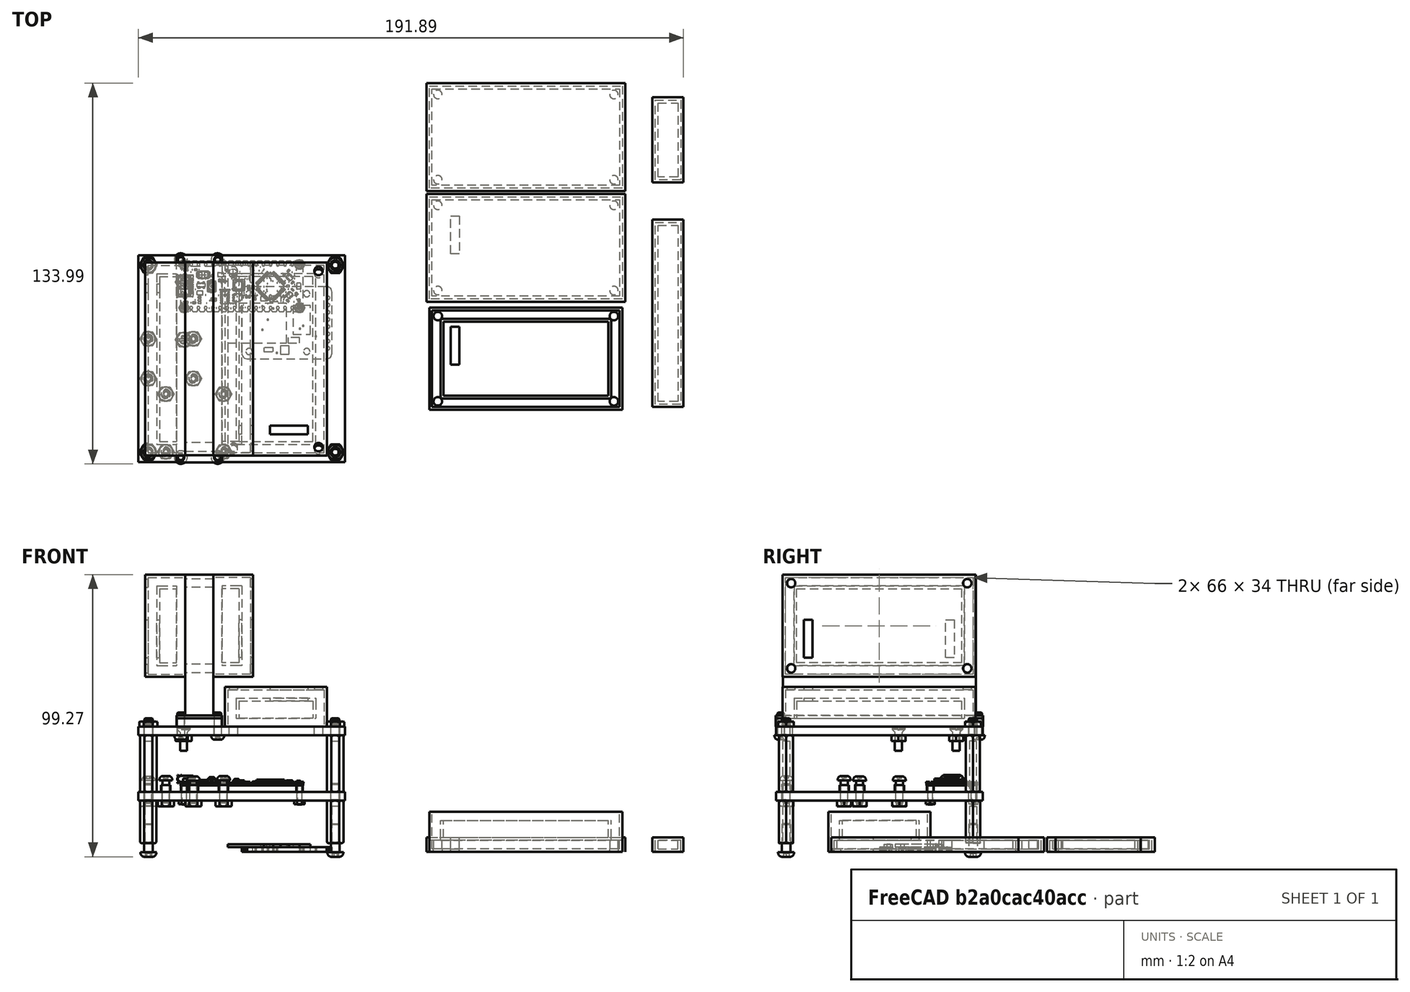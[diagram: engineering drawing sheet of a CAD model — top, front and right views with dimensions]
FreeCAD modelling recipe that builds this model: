
FCSTD DOCUMENT  (FreeCAD 0.20R29410 (Git))
Label: GeigerSat2
Comment: <copyright redacted>
License: All rights reserved
LicenseURL: http://en.wikipedia.org/wiki/All_rights_reserved
objects: Sketcher::SketchObject×62, Part::Feature×60, PartDesign::Pad×47, PartDesign::Body×22, App::DocumentObjectGroup×17, Part::Compound×17, PartDesign::Pocket×15, TechDraw::DrawViewAnnotation×6, Mesh::Feature×4, Part::Box×4, Part::Cut×4, TechDraw::DrawLeaderLine×4, Spreadsheet::Sheet×2, Part::Compound2×1, TechDraw::DrawSVGTemplate×1, TechDraw::DrawViewPart×1, TechDraw::DrawPage×1
note: 293 computed .brp shape members not serialized (recipe doc carries the construction recipe); baked Part::Feature solids carry a one-line shape summary decoded from their .brp

FEATURE [Mesh::Feature] Cubesat_Bottom_Frame
  Placement = pos=(0,0,98) rot=(0,1,0;3.14159rad)
FEATURE [Mesh::Feature] Cubesat_Side_Frame_Plain
  Placement = pos=(50.0625,-8.1e-15,49) rot=(-0.57735,0.57735,0.57735;4.18879rad)
FEATURE [Mesh::Feature] Cubesat_Side_Frame_Plain001
  Placement = pos=(-41.5,-6.6e-15,49) rot=(-0.57735,0.57735,0.57735;4.18879rad)
FEATURE [Mesh::Feature] Cubesat_Bottom_Frame001
FEATURE [App::DocumentObjectGroup] Group001  label="Frame"
  Group = -> [Cubesat_Bottom_Frame,Cubesat_Side_Frame_Plain,Cubesat_Side_Frame_Plain001,Cubesat_Bottom_Frame001]
FEATURE [Part::Feature] Solid018  label="M3x1.8mm Hex Nut"
  Placement = pos=(-32.9375,-32.875,-1.8125) rot=(0,0,1;0rad)
  shape: bbox 6.351 x 6.351 x 1.932 mm, 35 faces (baked)
FEATURE [Part::Feature] Solid019  label="M3x1.8mm Hex Nut001"
  Placement = pos=(32.9375,-32.875,-1.8125) rot=(0,0,1;0rad)
  shape: bbox 6.351 x 6.351 x 1.932 mm, 35 faces (baked)
FEATURE [Part::Feature] Solid020  label="M3x1.8mm Hex Nut002"
  Placement = pos=(32.9375,32.9375,-1.8125) rot=(0,0,1;0rad)
  shape: bbox 6.351 x 6.351 x 1.932 mm, 35 faces (baked)
FEATURE [Part::Feature] Solid021  label="M3x1.8mm Hex Nut003"
  Placement = pos=(-32.94,32.94,-1.81) rot=(0,0,1;0rad)
  shape: bbox 6.351 x 6.351 x 1.932 mm, 35 faces (baked)
FEATURE [Sketcher::SketchObject] Sketch
  FullyConstrained = true
  MapMode = 5
  Support = -> [XY_Plane]
  expr: Constraints[19] = 17.11 - 2.5 - 1
  sketch-geometry (10):
    g0: LineSegment StartX=-36.39 StartY=36.39 StartZ=0 EndX=36.39 EndY=36.39 EndZ=0
    g1: LineSegment StartX=36.39 StartY=36.39 StartZ=0 EndX=36.39 EndY=-36.39 EndZ=0
    g2: LineSegment StartX=36.39 StartY=-36.39 StartZ=0 EndX=-36.39 EndY=-36.39 EndZ=0
    g3: LineSegment StartX=-36.39 StartY=-36.39 StartZ=0 EndX=-36.39 EndY=36.39 EndZ=0
    g4: GeomPoint X=0 Y=0 Z=0
    g5: GeomPoint X=-50 Y=50 Z=0
    g6: GeomPoint X=50 Y=-50 Z=0
    g7: GeomPoint X=50 Y=50 Z=0
    g8: GeomPoint X=-50 Y=-50 Z=0
    g9: GeomPoint X=0 Y=0 Z=0
  constraints (20):
    c: Coincident(g0,g1)
    c: Coincident(g1,g2)
    c: Coincident(g2,g3)
    c: Coincident(g3,g0)
    c: Horizontal(g0)
    c: Horizontal(g2)
    c: Vertical(g1)
    c: Vertical(g3)
    c: Symmetric(g0,g1,g4)
    c: Coincident(g4,g-1)
    c: Equal(g0,g3)
    c: Symmetric(g5,g6,g9)
    c: Horizontal(g8,g6)
    c: Horizontal(g7,g5)
    c: Vertical(g5,g8)
    c: Vertical(g7,g6)
    c: Coincident(g9,g4)
    c: DistanceX(g5,g7) = 100
    c: DistanceY(g8,g5) = 100
    c: DistanceX(g5,g0) = 13.61
FEATURE [PartDesign::Pad] Pad
  Direction = (0,0,1)
  Length = 3
  Length2 = 10
  Profile = -> Sketch
  ReferenceAxis = -> Sketch [N_Axis]
  Type = 0
FEATURE [Part::Feature] Solid014  label="M3x10HexButtonHead"
  Placement = pos=(-32.93,-32.88,63.06) rot=(0,0,1;0rad)
  shape: bbox 5.7 x 5.7 x 11.65 mm, 13 faces (baked)
FEATURE [Part::Feature] Solid015  label="M3x10HexButtonHead003"
  Placement = pos=(-32.93,32.93,63.06) rot=(0,0,1;0rad)
  shape: bbox 5.7 x 5.7 x 11.65 mm, 13 faces (baked)
FEATURE [Part::Feature] Solid016  label="M3x10HexButtonHead002"
  Placement = pos=(32.88,32.93,63.06) rot=(0,0,1;0rad)
  shape: bbox 5.7 x 5.7 x 11.65 mm, 13 faces (baked)
FEATURE [Part::Feature] Solid017  label="M3x10HexButtonHead001"
  Placement = pos=(32.88,-32.88,63.06) rot=(0,0,1;0rad)
  shape: bbox 5.7 x 5.7 x 11.65 mm, 13 faces (baked)
FEATURE [Part::Compound] Compound  label="Stack Screws"
  Links = -> [Solid015,Solid016,Solid017,Solid014]
  Placement = pos=(-8e-15,0,62.9375) rot=(0,1,0;3.14159rad)
FEATURE [Part::Compound] Compound002  label="Stack Nuts"
  Links = -> [Solid021,Solid018,Solid019,Solid020]
  Placement = pos=(0,0,45.8125) rot=(0,0,1;0rad)
FEATURE [Sketcher::SketchObject] Sketch002
  FullyConstrained = true
  MapMode = 5
  Placement = pos=(0,0,3) rot=(0,0,1;0rad)
  Support = -> [Pad]
  expr: Constraints[31] = 17.11 - 2.5 - 1
  expr: Constraints[34] = 17.11 - 2.5 - 1
  expr: Constraints[35] = 2
  expr: Constraints[6] = 43.16
  expr: Constraints[7] = 17.76
  sketch-geometry (18):
    g0: GeomPoint X=-21.58 Y=34.39 Z=0
    g1: GeomPoint X=21.58 Y=34.39 Z=0
    g2: GeomPoint X=-21.58 Y=16.63 Z=0
    g3: GeomPoint X=21.58 Y=16.63 Z=0
    g4: GeomPoint X=0 Y=25.51 Z=0
    g5: Circle CenterX=-20.32 CenterY=33.13 CenterZ=0 NormalX=0 NormalY=0 NormalZ=1 AngleXU=0 Radius=0.825
    g6: Circle CenterX=20.32 CenterY=17.89 CenterZ=0 NormalX=0 NormalY=0 NormalZ=1 AngleXU=0 Radius=0.825
    g7: Circle CenterX=-20.32 CenterY=17.89 CenterZ=0 NormalX=0 NormalY=0 NormalZ=1 AngleXU=0 Radius=0.825
    g8: Circle CenterX=20.32 CenterY=33.13 CenterZ=0 NormalX=0 NormalY=0 NormalZ=1 AngleXU=0 Radius=0.825
    g9: GeomPoint X=-50 Y=50 Z=0
    g10: GeomPoint X=50 Y=50 Z=0
    g11: GeomPoint X=-50 Y=-50 Z=0
    g12: GeomPoint X=50 Y=-50 Z=0
    g13: GeomPoint X=0 Y=0 Z=0
    g14: GeomPoint X=36.39 Y=-36.39 Z=0
    g15: GeomPoint X=36.39 Y=36.39 Z=0
    g16: GeomPoint X=-36.39 Y=36.39 Z=0
    g17: GeomPoint X=-36.39 Y=-36.39 Z=0
  constraints (36):
    c: Symmetric(g0,g3,g4)
    c: Horizontal(g0,g1)
    c: Horizontal(g3,g2)
    c: Vertical(g2,g0)
    c: Vertical(g3,g1)
    c: Vertical(g4,g-1)
    c: DistanceX(g0,g1) = 43.16
    c: DistanceY(g3,g1) = 17.76
    c: DistanceX(g0,g5) = 1.26
    c: DistanceY(g5,g0) = 1.26
    c: DistanceX(g6,g3) = 1.26
    c: DistanceY(g3,g6) = 1.26
    c: Horizontal(g8,g5)
    c: Vertical(g8,g6)
    c: Vertical(g5,g7)
    c: Horizontal(g7,g6)
    c: Diameter(g7) = 1.65
    c: Diameter(g5) = 1.65
    c: Diameter(g8) = 1.65
    c: Diameter(g6) = 1.65
    c: Horizontal(g9,g10)
    c: Horizontal(g12,g11)
    c: Symmetric(g9,g12,g13)
    c: Horizontal(g17,g14)
    c: Horizontal(g15,g16)
    c: Vertical(g17,g16)
    c: Vertical(g15,g14)
    c: Symmetric(g15,g17,g13)
    c: Vertical(g9,g11)
    c: Vertical(g12,g10)
    c: DistanceX(g9,g10) = 100
    c: DistanceX(g9,g17) = 13.61
    c: Coincident(g13,g-1)
    c: DistanceY(g11,g9) = 100
    c: DistanceY(g16,g9) = 13.61
    c: DistanceY(g1,g15) = 2
FEATURE [Sketcher::SketchObject] Sketch004
  FullyConstrained = true
  MapMode = 5
  Placement = pos=(0,0,3) rot=(0,0,1;0rad)
  expr: Constraints[31] = 17.11 - 2.5 - 1
  expr: Constraints[34] = 17.11 - 2.5 - 1
  expr: Constraints[35] = 2
  expr: Constraints[37] = 1.65 + 0.75
  expr: Constraints[38] = 1.65 + 0.75
  expr: Constraints[39] = 1.65 + 0.75
  expr: Constraints[40] = 1.65 + 0.75
  expr: Constraints[6] = 43.16
  expr: Constraints[7] = 17.76
  sketch-geometry (22):
    g0: GeomPoint X=-21.58 Y=34.39 Z=0
    g1: GeomPoint X=21.58 Y=34.39 Z=0
    g2: GeomPoint X=-21.58 Y=16.63 Z=0
    g3: GeomPoint X=21.58 Y=16.63 Z=0
    g4: GeomPoint X=0 Y=25.51 Z=0
    g5: Circle CenterX=-20.32 CenterY=33.13 CenterZ=0 NormalX=0 NormalY=0 NormalZ=1 AngleXU=0 Radius=0.825
    g6: Circle CenterX=20.32 CenterY=17.89 CenterZ=0 NormalX=0 NormalY=0 NormalZ=1 AngleXU=0 Radius=0.825
    g7: Circle CenterX=-20.32 CenterY=17.89 CenterZ=0 NormalX=0 NormalY=0 NormalZ=1 AngleXU=0 Radius=0.825
    g8: Circle CenterX=20.32 CenterY=33.13 CenterZ=0 NormalX=0 NormalY=0 NormalZ=1 AngleXU=0 Radius=0.825
    g9: GeomPoint X=-50 Y=50 Z=0
    g10: GeomPoint X=50 Y=50 Z=0
    g11: GeomPoint X=-50 Y=-50 Z=0
    g12: GeomPoint X=50 Y=-50 Z=0
    g13: GeomPoint X=0 Y=0 Z=0
    g14: GeomPoint X=36.39 Y=-36.39 Z=0
    g15: GeomPoint X=36.39 Y=36.39 Z=0
    g16: GeomPoint X=-36.39 Y=36.39 Z=0
    g17: GeomPoint X=-36.39 Y=-36.39 Z=0
    g18: Circle CenterX=-20.32 CenterY=33.13 CenterZ=0 NormalX=0 NormalY=0 NormalZ=1 AngleXU=0 Radius=1.2
    g19: Circle CenterX=20.32 CenterY=17.89 CenterZ=0 NormalX=0 NormalY=0 NormalZ=1 AngleXU=0 Radius=1.2
    g20: Circle CenterX=20.32 CenterY=33.13 CenterZ=0 NormalX=0 NormalY=0 NormalZ=1 AngleXU=0 Radius=1.2
    g21: Circle CenterX=-20.32 CenterY=17.89 CenterZ=0 NormalX=0 NormalY=0 NormalZ=1 AngleXU=0 Radius=1.2
  constraints (44):
    c: Symmetric(g0,g3,g4)
    c: Horizontal(g0,g1)
    c: Horizontal(g3,g2)
    c: Vertical(g2,g0)
    c: Vertical(g3,g1)
    c: Vertical(g4,g-1)
    c: DistanceX(g0,g1) = 43.16
    c: DistanceY(g3,g1) = 17.76
    c: DistanceX(g0,g5) = 1.26
    c: DistanceY(g5,g0) = 1.26
    c: DistanceX(g6,g3) = 1.26
    c: DistanceY(g3,g6) = 1.26
    c: Horizontal(g8,g5)
    c: Vertical(g8,g6)
    c: Vertical(g5,g7)
    c: Horizontal(g7,g6)
    c: Diameter(g7) = 1.65
    c: Diameter(g5) = 1.65
    c: Diameter(g8) = 1.65
    c: Diameter(g6) = 1.65
    c: Horizontal(g9,g10)
    c: Horizontal(g12,g11)
    c: Symmetric(g9,g12,g13)
    c: Horizontal(g17,g14)
    c: Horizontal(g15,g16)
    c: Vertical(g17,g16)
    c: Vertical(g15,g14)
    c: Symmetric(g15,g17,g13)
    c: Vertical(g9,g11)
    c: Vertical(g12,g10)
    c: DistanceX(g9,g10) = 100
    c: DistanceX(g9,g17) = 13.61
    c: Coincident(g13,g-1)
    c: DistanceY(g11,g9) = 100
    c: DistanceY(g16,g9) = 13.61
    c: DistanceY(g1,g15) = 2
    c: Coincident(g18,g5)
    c: Diameter(g18) = 2.4
    c: Diameter(g19) = 2.4
    c: Diameter(g20) = 2.4
    c: Diameter(g21) = 2.4
    c: Coincident(g20,g8)
    c: Coincident(g19,g6)
    c: Coincident(g21,g7)
FEATURE [PartDesign::Pocket] Pocket
  BaseFeature = -> Pad
  Direction = (0,0,-1)
  Length = 5
  Length2 = 5
  Profile = -> Sketch002
  ReferenceAxis = -> Sketch002 [N_Axis]
  Type = 1
FEATURE [PartDesign::Pad] Pad003
  BaseFeature = -> Pocket
  Direction = (0,0,1)
  Length = 2.5
  Length2 = 10
  Profile = -> Sketch004
  ReferenceAxis = -> Sketch004 [N_Axis]
  Type = 0
FEATURE [Sketcher::SketchObject] Sketch005
  FullyConstrained = true
  MapMode = 5
  Placement = pos=(0,0,3) rot=(0,0,1;0rad)
  Support = -> [Pad003]
  expr: Constraints[10] = 0.55in
  expr: Constraints[5] = 0.8in
  expr: Constraints[6] = 0.75in
  sketch-geometry (11):
    g0: Circle CenterX=-32.9375 CenterY=6.985 CenterZ=0 NormalX=0 NormalY=0 NormalZ=1 AngleXU=0 Radius=1.27
    g1: GeomPoint X=-35.16 Y=9.525 Z=0
    g2: GeomPoint X=-14.84 Y=9.525 Z=0
    g3: GeomPoint X=-14.84 Y=-9.525 Z=0
    g4: GeomPoint X=-35.16 Y=-9.525 Z=0
    g5: GeomPoint X=-25 Y=0 Z=0
    g6: Circle CenterX=-32.9375 CenterY=-6.985 CenterZ=0 NormalX=0 NormalY=0 NormalZ=1 AngleXU=0 Radius=1.27
    g7: GeomPoint X=-32.9375 Y=0 Z=0
    g8: Circle CenterX=-17.0625 CenterY=6.985 CenterZ=0 NormalX=0 NormalY=0 NormalZ=1 AngleXU=0 Radius=1.27
    g9: Circle CenterX=-17.0625 CenterY=-6.985 CenterZ=0 NormalX=0 NormalY=0 NormalZ=1 AngleXU=0 Radius=1.27
    g10: GeomPoint X=-17.0625 Y=0 Z=0
  constraints (22):
    c: Symmetric(g1,g3,g5)
    c: Vertical(g1,g4)
    c: Vertical(g3,g2)
    c: Horizontal(g1,g2)
    c: Horizontal(g3,g4)
    c: DistanceX(g1,g2) = 20.32
    c: DistanceY(g3,g2) = 19.05
    c: Diameter(g0) = 2.54
    c: Vertical(g7,g0)
    c: Horizontal(g7,g5)
    c: DistanceY(g6,g0) = 13.97
    c: Diameter(g6) = 2.54
    c: Symmetric(g0,g6,g7)
    c: Horizontal(g5,g-1)
    c: Diameter(g9) = 2.54
    c: Diameter(g8) = 2.54
    c: Vertical(g8,g10)
    c: Symmetric(g9,g8,g10)
    c: Horizontal(g0,g8)
    c: DistanceX(g0,g8) = 15.875
    c: Symmetric(g7,g10,g5)
    c: DistanceX(g5,g-1) = 25
FEATURE [Part::Feature] Adafruit_Micro_Lipo_wMicroUSB_Jack___USB_LiIonLiPoly_charger
  shape: bbox 21 x 19 x 1.905 mm, 18 faces, 0 solids (baked)
FEATURE [Part::Feature] Adafruit_Micro_Lipo_wMicroUSB_Jack___USB_LiIonLiPoly_charger003
  Placement = pos=(10.1254,0.344843,1.5875) rot=(0.57735,0.57735,0.57735;2.0944rad)
  shape: bbox 8.6 x 7.9 x 4.803 mm, 126 faces, 0 solids (baked)
FEATURE [Sketcher::SketchObject] Sketch009
  FullyConstrained = true
  MapMode = 5
  Placement = pos=(0,0,3) rot=(0,0,1;0rad)
  expr: Constraints[10] = 0.55in
  expr: Constraints[19] = 0.625in
  expr: Constraints[26] = 2.54 + 0.75
  expr: Constraints[5] = 0.8in
  expr: Constraints[6] = 0.75in
  sketch-geometry (15):
    g0: Circle CenterX=-32.9375 CenterY=6.985 CenterZ=0 NormalX=0 NormalY=0 NormalZ=1 AngleXU=0 Radius=1.27
    g1: GeomPoint X=-35.16 Y=9.525 Z=0
    g2: GeomPoint X=-14.84 Y=9.525 Z=0
    g3: GeomPoint X=-14.84 Y=-9.525 Z=0
    g4: GeomPoint X=-35.16 Y=-9.525 Z=0
    g5: GeomPoint X=-25 Y=0 Z=0
    g6: Circle CenterX=-32.9375 CenterY=-6.985 CenterZ=0 NormalX=0 NormalY=0 NormalZ=1 AngleXU=0 Radius=1.27
    g7: GeomPoint X=-32.9375 Y=0 Z=0
    g8: Circle CenterX=-17.0625 CenterY=6.985 CenterZ=0 NormalX=0 NormalY=0 NormalZ=1 AngleXU=0 Radius=1.27
    g9: Circle CenterX=-17.0625 CenterY=-6.985 CenterZ=0 NormalX=0 NormalY=0 NormalZ=1 AngleXU=0 Radius=1.27
    g10: GeomPoint X=-17.0625 Y=0 Z=0
    g11: Circle CenterX=-32.9375 CenterY=-6.985 CenterZ=0 NormalX=0 NormalY=0 NormalZ=1 AngleXU=0 Radius=1.645
    g12: Circle CenterX=-17.0625 CenterY=-6.985 CenterZ=0 NormalX=0 NormalY=0 NormalZ=1 AngleXU=0 Radius=1.645
    g13: Circle CenterX=-17.0625 CenterY=6.985 CenterZ=0 NormalX=0 NormalY=0 NormalZ=1 AngleXU=0 Radius=1.645
    g14: Circle CenterX=-32.9375 CenterY=6.985 CenterZ=0 NormalX=0 NormalY=0 NormalZ=1 AngleXU=0 Radius=1.645
  constraints (30):
    c: Symmetric(g1,g3,g5)
    c: Vertical(g1,g4)
    c: Vertical(g3,g2)
    c: Horizontal(g1,g2)
    c: Horizontal(g3,g4)
    c: DistanceX(g1,g2) = 20.32
    c: DistanceY(g3,g2) = 19.05
    c: Diameter(g0) = 2.54
    c: Vertical(g7,g0)
    c: Horizontal(g7,g5)
    c: DistanceY(g6,g0) = 13.97
    c: Diameter(g6) = 2.54
    c: Symmetric(g0,g6,g7)
    c: Horizontal(g5,g-1)
    c: Diameter(g9) = 2.54
    c: Diameter(g8) = 2.54
    c: Vertical(g8,g10)
    c: Symmetric(g9,g8,g10)
    c: Horizontal(g0,g8)
    c: DistanceX(g0,g8) = 15.875
    c: Symmetric(g7,g10,g5)
    c: DistanceX(g5,g-1) = 25
    c: Coincident(g11,g6)
    c: Coincident(g12,g9)
    c: Coincident(g13,g8)
    c: Coincident(g14,g0)
    c: Diameter(g14) = 3.29
    c: Diameter(g11) = 3.29
    c: Diameter(g12) = 3.29
    c: Diameter(g13) = 3.29
FEATURE [PartDesign::Pocket] Pocket002
  BaseFeature = -> Pad003
  Direction = (0,0,-1)
  Length = 5
  Length2 = 5
  Profile = -> Sketch005
  ReferenceAxis = -> Sketch005 [N_Axis]
  Type = 1
FEATURE [PartDesign::Pad] Pad006
  BaseFeature = -> Pocket002
  Direction = (0,0,1)
  Length = 2.5
  Length2 = 10
  Profile = -> Sketch009
  ReferenceAxis = -> Sketch009 [N_Axis]
  Type = 0
FEATURE [Part::Feature] Solid  label="M2.5x08HexButttonHead"
  Placement = pos=(-17.0625,-7,24.3125) rot=(0,0,1;0rad)
  shape: bbox 4.6 x 4.6 x 9.5 mm, 13 faces (baked)
FEATURE [Part::Feature] Solid026  label="M2.5x08HexButttonHead001"
  Placement = pos=(-32.9375,7,24.3125) rot=(0,0,1;0rad)
  shape: bbox 4.6 x 4.6 x 9.5 mm, 13 faces (baked)
FEATURE [Part::Feature] Solid027  label="M2.5x08HexButttonHead002"
  Placement = pos=(-17.0625,7,24.3125) rot=(0,0,1;0rad)
  shape: bbox 4.6 x 4.6 x 9.5 mm, 13 faces (baked)
FEATURE [Part::Feature] Solid028  label="M2.5x08HexButttonHead003"
  Placement = pos=(-32.9375,-7,24.3125) rot=(0,0,1;0rad)
  shape: bbox 4.6 x 4.6 x 9.5 mm, 13 faces (baked)
FEATURE [Part::Compound] Compound005  label="Battery Charger Screws"
  Links = -> [Solid,Solid026,Solid027,Solid028]
  Placement = pos=(0,0,0.6875) rot=(0,0,1;0rad)
FEATURE [Part::Feature] Feature  label="Arduino Nano Every"
  Placement = pos=(-21.625,16.625,23.375) rot=(0,0,1;0rad)
  shape: bbox 44.3 x 17.79 x 3.633 mm, 4603 faces, 115 solids (baked)
FEATURE [Part::Feature] Part__Feature001  label="ISO2009-M1.6x8_"
  Placement = pos=(20.3125,17.875,23.9375) rot=(0,0,1;0rad)
  shape: bbox 2.8 x 2.8 x 8 mm, 12 faces (baked)
FEATURE [Part::Feature] Part__Feature002  label="ISO2009-M1.6x8_001"
  Placement = pos=(20.3125,33.125,23.9375) rot=(0,0,1;0rad)
  shape: bbox 2.8 x 2.8 x 8 mm, 12 faces (baked)
FEATURE [Part::Feature] Part__Feature003  label="ISO2009-M1.6x8_002"
  Placement = pos=(-20.3125,33.125,23.9375) rot=(0,0,1;0rad)
  shape: bbox 2.8 x 2.8 x 8 mm, 12 faces (baked)
FEATURE [Part::Feature] Part__Feature004  label="ISO2009-M1.6x8_003"
  Placement = pos=(-20.3125,17.875,23.9375) rot=(0,0,1;0rad)
  shape: bbox 2.8 x 2.8 x 8 mm, 12 faces (baked)
FEATURE [Part::Compound] Compound006  label="Arduino Screws"
  Links = -> [Part__Feature001,Part__Feature002,Part__Feature003,Part__Feature004]
  Placement = pos=(0,0,0.625) rot=(0,0,1;0rad)
FEATURE [Part::Feature] Solid029
  shape: bbox 31.75 x 25.4 x 1.6 mm, 74 faces (baked)
FEATURE [Part::Feature] Solid030
  shape: bbox 2.1 x 1.351 x 1 mm, 6 faces (baked)
FEATURE [Part::Feature] Solid031
  shape: bbox 3.2 x 1.276 x 1 mm, 6 faces (baked)
FEATURE [Part::Feature] Solid032
  shape: bbox 4 x 2 x 1 mm, 6 faces (baked)
FEATURE [Part::Feature] Solid033
  shape: bbox 6.198 x 10.16 x 1 mm, 6 faces (baked)
FEATURE [Part::Feature] Solid034
  shape: bbox 3 x 2.92 x 1 mm, 6 faces (baked)
FEATURE [Part::Feature] Solid035
  shape: bbox 3.946 x 1.966 x 1 mm, 6 faces (baked)
FEATURE [Part::Feature] Solid036
  shape: bbox 20.63 x 14.06 x 1 mm, 6 faces (baked)
FEATURE [Part::Compound2] Compound007  label="Adafruit SD Reader"
  Links = -> [Solid029,Solid030,Solid031,Solid032,Solid033,Solid034,Solid035,Solid036]
  Placement = pos=(-29.3125,-35.25,23.5) rot=(0,0,1;0rad)
FEATURE [Sketcher::SketchObject] Sketch010
  FullyConstrained = true
  MapMode = 5
  Placement = pos=(0,0,3) rot=(0,0,1;0rad)
  Support = -> [Pad006]
  expr: Constraints[5] = 0.1in
  sketch-geometry (9):
    g0: GeomPoint X=-29.305 Y=-9.87 Z=0
    g1: GeomPoint X=2.445 Y=-9.87 Z=0
    g2: GeomPoint X=2.445 Y=-35.27 Z=0
    g3: GeomPoint X=-29.305 Y=-35.27 Z=0
    g4: GeomPoint X=-13.43 Y=-22.57 Z=0
    g5: Circle CenterX=-26.765 CenterY=-12.41 CenterZ=0 NormalX=0 NormalY=0 NormalZ=1 AngleXU=0 Radius=1.225
    g6: Circle CenterX=-6.445 CenterY=-12.41 CenterZ=0 NormalX=0 NormalY=0 NormalZ=1 AngleXU=0 Radius=1.27
    g7: Circle CenterX=-6.445 CenterY=-32.73 CenterZ=0 NormalX=0 NormalY=0 NormalZ=1 AngleXU=0 Radius=1.27
    g8: Circle CenterX=-26.765 CenterY=-32.73 CenterZ=0 NormalX=0 NormalY=0 NormalZ=1 AngleXU=0 Radius=1.27
  constraints (21):
    c: Symmetric(g0,g2,g4)
    c: Horizontal(g3,g2)
    c: Horizontal(g0,g1)
    c: Vertical(g0,g3)
    c: Vertical(g1,g2)
    c: Diameter(g8) = 2.54
    c: Diameter(g7) = 2.54
    c: Diameter(g6) = 2.54
    c: Diameter(g5) = 2.45
    c: DistanceX(g0,g1) = 31.75
    c: DistanceY(g3,g0) = 25.4
    c: DistanceX(g5,g0) = -2.54
    c: DistanceY(g5,g0) = 2.54
    c: DistanceY(g3,g8) = 2.54
    c: DistanceX(g3,g8) = 2.54
    c: Horizontal(g8,g7)
    c: Horizontal(g6,g5)
    c: Vertical(g6,g7)
    c: DistanceX(g0,g6) = 22.86
    c: DistanceX(g4) = -13.43
    c: DistanceY(g4,g-1) = 22.57
FEATURE [Sketcher::SketchObject] Sketch016
  FullyConstrained = true
  MapMode = 5
  Placement = pos=(0,0,3) rot=(0,0,1;0rad)
  expr: Constraints[5] = 0.1in
  sketch-geometry (13):
    g0: GeomPoint X=-29.305 Y=-9.87 Z=0
    g1: GeomPoint X=2.445 Y=-9.87 Z=0
    g2: GeomPoint X=2.445 Y=-35.27 Z=0
    g3: GeomPoint X=-29.305 Y=-35.27 Z=0
    g4: GeomPoint X=-13.43 Y=-22.57 Z=0
    g5: Circle CenterX=-26.765 CenterY=-12.41 CenterZ=0 NormalX=0 NormalY=0 NormalZ=1 AngleXU=0 Radius=1.27
    g6: Circle CenterX=-6.445 CenterY=-12.41 CenterZ=0 NormalX=0 NormalY=0 NormalZ=1 AngleXU=0 Radius=1.27
    g7: Circle CenterX=-6.445 CenterY=-32.73 CenterZ=0 NormalX=0 NormalY=0 NormalZ=1 AngleXU=0 Radius=1.27
    g8: Circle CenterX=-26.765 CenterY=-32.73 CenterZ=0 NormalX=0 NormalY=0 NormalZ=1 AngleXU=0 Radius=1.27
    g9: Circle CenterX=-6.445 CenterY=-12.41 CenterZ=0 NormalX=0 NormalY=0 NormalZ=1 AngleXU=0 Radius=1.645
    g10: Circle CenterX=-26.765 CenterY=-12.41 CenterZ=0 NormalX=0 NormalY=0 NormalZ=1 AngleXU=0 Radius=1.645
    g11: Circle CenterX=-26.765 CenterY=-32.73 CenterZ=0 NormalX=0 NormalY=0 NormalZ=1 AngleXU=0 Radius=1.645
    g12: Circle CenterX=-6.445 CenterY=-32.73 CenterZ=0 NormalX=0 NormalY=0 NormalZ=1 AngleXU=0 Radius=1.645
  constraints (29):
    c: Symmetric(g0,g2,g4)
    c: Horizontal(g3,g2)
    c: Horizontal(g0,g1)
    c: Vertical(g0,g3)
    c: Vertical(g1,g2)
    c: Diameter(g8) = 2.54
    c: Diameter(g7) = 2.54
    c: Diameter(g6) = 2.54
    c: Diameter(g5) = 2.54
    c: DistanceX(g0,g1) = 31.75
    c: DistanceY(g3,g0) = 25.4
    c: DistanceX(g5,g0) = -2.54
    c: DistanceY(g5,g0) = 2.54
    c: DistanceY(g3,g8) = 2.54
    c: DistanceX(g3,g8) = 2.54
    c: Horizontal(g8,g7)
    c: Horizontal(g6,g5)
    c: Vertical(g6,g7)
    c: DistanceX(g0,g6) = 22.86
    c: DistanceX(g4) = -13.43
    c: DistanceY(g4,g-1) = 22.57
    c: Coincident(g9,g6)
    c: Coincident(g10,g5)
    c: Coincident(g11,g8)
    c: Coincident(g12,g7)
    c: Diameter(g12) = 3.29
    c: Diameter(g11) = 3.29
    c: Diameter(g9) = 3.29
    c: Diameter(g10) = 3.29
FEATURE [PartDesign::Pocket] Pocket003
  BaseFeature = -> Pad006
  Direction = (0,0,-1)
  Length = 5
  Length2 = 5
  Profile = -> Sketch010
  ReferenceAxis = -> Sketch010 [N_Axis]
  Type = 1
FEATURE [PartDesign::Pad] Pad007
  BaseFeature = -> Pocket003
  Direction = (0,0,1)
  Length = 2.5
  Length2 = 10
  Profile = -> Sketch016
  ReferenceAxis = -> Sketch016 [N_Axis]
  Type = 0
FEATURE [Part::Feature] Solid037  label="M2.5x08HexButttonHead004"
  Placement = pos=(-26.75,-32.75,24.3125) rot=(0,0,1;0rad)
  shape: bbox 4.6 x 4.6 x 9.5 mm, 13 faces (baked)
FEATURE [Part::Feature] Part__Feature  label="ISO4032-M2.5_"
  Placement = pos=(-26.75,-32.75,0) rot=(0,0,1;0rad)
  shape: bbox 5.774 x 5.774 x 2 mm, 25 faces (baked)
FEATURE [Part::Feature] Solid038  label="M2.5x08HexButttonHead005"
  Placement = pos=(-6.4375,-32.75,24.3125) rot=(0,0,1;0rad)
  shape: bbox 4.6 x 4.6 x 9.5 mm, 13 faces (baked)
FEATURE [Part::Feature] Part__Feature005  label="ISO4032-M2.5_001"
  Placement = pos=(-6.4375,-32.75,0) rot=(0,0,1;0rad)
  shape: bbox 5.774 x 5.774 x 2 mm, 25 faces (baked)
FEATURE [Part::Feature] Solid039  label="M2.5x08HexButttonHead006"
  Placement = pos=(-6.4375,-12.4375,24.3125) rot=(0,0,1;0rad)
  shape: bbox 4.6 x 4.6 x 9.5 mm, 13 faces (baked)
FEATURE [Part::Feature] Part__Feature006  label="ISO4032-M2.5_002"
  Placement = pos=(-6.4375,-12.4375,0) rot=(0,0,1;0rad)
  shape: bbox 5.774 x 5.774 x 2 mm, 25 faces (baked)
FEATURE [Part::Feature] Solid040  label="M2.5x08HexButttonHead007"
  Placement = pos=(-26.75,-12.4375,24.3125) rot=(0,0,1;0rad)
  shape: bbox 4.6 x 4.6 x 9.5 mm, 13 faces (baked)
FEATURE [Part::Feature] Part__Feature007  label="ISO4032-M2.5_003"
  Placement = pos=(-26.75,-12.4375,0) rot=(0,0,1;0rad)
  shape: bbox 5.774 x 5.774 x 2 mm, 25 faces (baked)
FEATURE [Part::Compound] Compound008  label="SD Reader Nuts"
  Links = -> [Part__Feature006,Part__Feature007,Part__Feature005,Part__Feature]
  Placement = pos=(0,0,16) rot=(0,0,1;0rad)
FEATURE [Part::Compound] Compound009  label="SD Reader Screws"
  Links = -> [Solid040,Solid037,Solid038,Solid039]
  Placement = pos=(0,0,0.8125) rot=(0,0,1;0rad)
FEATURE [Part::Feature] Part__Feature008  label="ISO4032-M2.5_004"
  Placement = pos=(-32.9375,-7,0) rot=(0,0,1;0rad)
  shape: bbox 5.774 x 5.774 x 2 mm, 25 faces (baked)
FEATURE [Part::Feature] Part__Feature009  label="ISO4032-M2.5_005"
  Placement = pos=(-17.0625,-7,0) rot=(0,0,1;0rad)
  shape: bbox 5.774 x 5.774 x 2 mm, 25 faces (baked)
FEATURE [Part::Feature] Part__Feature010  label="ISO4032-M2.5_006"
  Placement = pos=(-17.0625,7,0) rot=(0,0,1;0rad)
  shape: bbox 5.774 x 5.774 x 2 mm, 25 faces (baked)
FEATURE [Part::Feature] Part__Feature011  label="ISO4032-M2.5_007"
  Placement = pos=(-32.9375,7,0) rot=(0,0,1;0rad)
  shape: bbox 5.774 x 5.774 x 2 mm, 25 faces (baked)
FEATURE [Part::Compound] Compound010  label="Battery Charger Nuts"
  Links = -> [Part__Feature011,Part__Feature008,Part__Feature009,Part__Feature010]
  Placement = pos=(0,0,16) rot=(0,0,1;0rad)
FEATURE [Part::Feature] Part__Feature012  label="ISO4032-M1.6_"
  Placement = pos=(20.3125,17.875,16.6875) rot=(0,0,1;0rad)
  shape: bbox 3.695 x 3.695 x 1.3 mm, 25 faces (baked)
FEATURE [Part::Feature] Part__Feature013  label="ISO4032-M1.6_001"
  Placement = pos=(20.3125,33.125,16.6875) rot=(0,0,1;0rad)
  shape: bbox 3.695 x 3.695 x 1.3 mm, 25 faces (baked)
FEATURE [Part::Feature] Part__Feature014  label="ISO4032-M1.6_002"
  Placement = pos=(-20.3125,33.125,16.6875) rot=(0,0,1;0rad)
  shape: bbox 3.695 x 3.695 x 1.3 mm, 25 faces (baked)
FEATURE [Part::Feature] Part__Feature015  label="ISO4032-M1.6_003"
  Placement = pos=(-20.3125,17.875,16.6875) rot=(0,0,1;0rad)
  shape: bbox 3.695 x 3.695 x 1.3 mm, 25 faces (baked)
FEATURE [Part::Compound] Compound011  label="Arduino Nuts"
  Links = -> [Part__Feature012,Part__Feature013,Part__Feature014,Part__Feature015]
FEATURE [App::DocumentObjectGroup] Group015  label="Headers"
FEATURE [Sketcher::SketchObject] Sketch019
  FullyConstrained = true
  MapMode = 5
  Support = -> [XY_Plane002]
  expr: Constraints[19] = 17.11 - 2.5 - 1
  sketch-geometry (10):
    g0: LineSegment StartX=-36.39 StartY=36.39 StartZ=0 EndX=36.39 EndY=36.39 EndZ=0
    g1: LineSegment StartX=36.39 StartY=36.39 StartZ=0 EndX=36.39 EndY=-36.39 EndZ=0
    g2: LineSegment StartX=36.39 StartY=-36.39 StartZ=0 EndX=-36.39 EndY=-36.39 EndZ=0
    g3: LineSegment StartX=-36.39 StartY=-36.39 StartZ=0 EndX=-36.39 EndY=36.39 EndZ=0
    g4: GeomPoint X=0 Y=0 Z=0
    g5: GeomPoint X=-50 Y=50 Z=0
    g6: GeomPoint X=50 Y=-50 Z=0
    g7: GeomPoint X=50 Y=50 Z=0
    g8: GeomPoint X=-50 Y=-50 Z=0
    g9: GeomPoint X=0 Y=0 Z=0
  constraints (20):
    c: Coincident(g0,g1)
    c: Coincident(g1,g2)
    c: Coincident(g2,g3)
    c: Coincident(g3,g0)
    c: Horizontal(g0)
    c: Horizontal(g2)
    c: Vertical(g1)
    c: Vertical(g3)
    c: Symmetric(g0,g1,g4)
    c: Coincident(g4,g-1)
    c: Equal(g0,g3)
    c: Symmetric(g5,g6,g9)
    c: Horizontal(g8,g6)
    c: Horizontal(g7,g5)
    c: Vertical(g5,g8)
    c: Vertical(g7,g6)
    c: Coincident(g9,g4)
    c: DistanceX(g5,g7) = 100
    c: DistanceY(g8,g5) = 100
    c: DistanceX(g5,g0) = 13.61
FEATURE [PartDesign::Pad] Pad009
  Direction = (0,0,1)
  Length = 3
  Length2 = 10
  Profile = -> Sketch019
  ReferenceAxis = -> Sketch019 [N_Axis]
  Type = 0
FEATURE [Part::Feature] Solid004  label="M3_M_TO_F_15MM_STANDOFF002"
  Placement = pos=(32.875,-32.875,10.5) rot=(0,1,0;3.14159rad)
  shape: bbox 5.774 x 5.774 x 21 mm, 24 faces (baked)
FEATURE [Part::Feature] Solid011  label="M3_M_TO_F_15MM_STANDOFF009"
  Placement = pos=(-32.93,-32.88,10.5) rot=(0,1,0;3.14159rad)
  shape: bbox 5.774 x 5.774 x 21 mm, 24 faces (baked)
FEATURE [Part::Feature] Solid012  label="M3_M_TO_F_15MM_STANDOFF010"
  Placement = pos=(-32.93,32.93,10.5) rot=(0,1,0;3.14159rad)
  shape: bbox 5.774 x 5.774 x 21 mm, 24 faces (baked)
FEATURE [Part::Feature] Solid013  label="M3_M_TO_F_15MM_STANDOFF011"
  Placement = pos=(32.88,32.93,10.5) rot=(0,1,0;3.14159rad)
  shape: bbox 5.774 x 5.774 x 21 mm, 24 faces (baked)
FEATURE [Part::Compound] Compound001  label="Stack Layer 1 Standoffs"
  Links = -> [Solid004,Solid011,Solid012,Solid013]
FEATURE [Part::Feature] Part__Feature016  label="ISO2009-M2.5x8_"
  Placement = pos=(-20.5,6.6875,43.5) rot=(0,0,1;0rad)
  shape: bbox 4.5 x 4.5 x 8 mm, 12 faces (baked)
FEATURE [Part::Feature] Part__Feature017  label="ISO2009-M2.5x8_001"
  Placement = pos=(-20.5,27,43.5) rot=(0,0,1;0rad)
  shape: bbox 4.5 x 4.5 x 8 mm, 12 faces (baked)
FEATURE [Part::Feature] Part__Feature018  label="ISO4032-M2.5_008"
  Placement = pos=(-20.5,27,34) rot=(0,0,1;0rad)
  shape: bbox 5.774 x 5.774 x 2 mm, 25 faces (baked)
FEATURE [Part::Feature] Part__Feature019  label="ISO4032-M2.5_009"
  Placement = pos=(-20.5,6.69,34) rot=(0,0,1;0rad)
  shape: bbox 5.774 x 5.774 x 2 mm, 25 faces (baked)
FEATURE [Part::Compound] Compound014  label="BMP388 Nuts"
  Links = -> [Part__Feature019,Part__Feature018]
  Placement = pos=(0,0,4.9375) rot=(0,0,1;0rad)
FEATURE [App::DocumentObjectGroup] Group012  label="Nuts"
  Group = -> [Compound002,Compound008,Compound011,Compound010,Compound014]
FEATURE [Part::Feature] Solid048  label="M3_M_TO_F_20MM_STANDOFF"
  Placement = pos=(32.88,-32.88,31) rot=(1,0,0;3.14159rad)
  shape: bbox 5.774 x 5.774 x 26 mm, 24 faces (baked)
FEATURE [Part::Feature] Solid049  label="M3_M_TO_F_20MM_STANDOFF001"
  Placement = pos=(32.88,32.88,31) rot=(1,0,0;3.14159rad)
  shape: bbox 5.774 x 5.774 x 26 mm, 24 faces (baked)
FEATURE [Part::Feature] Solid050  label="M3_M_TO_F_20MM_STANDOFF002"
  Placement = pos=(-32.88,32.88,31) rot=(1,0,0;3.14159rad)
  shape: bbox 5.774 x 5.774 x 26 mm, 24 faces (baked)
FEATURE [Part::Feature] Solid051  label="M3_M_TO_F_20MM_STANDOFF003"
  Placement = pos=(-32.88,-32.88,31) rot=(1,0,0;3.14159rad)
  shape: bbox 5.774 x 5.774 x 26 mm, 24 faces (baked)
FEATURE [Part::Compound] Compound015  label="Stack Layer 2 Standoffs"
  Links = -> [Solid048,Solid049,Solid050,Solid051]
FEATURE [App::DocumentObjectGroup] Group007  label="Standoffs"
  Group = -> [Compound001,Compound015]
FEATURE [Sketcher::SketchObject] Sketch027
  FullyConstrained = true
  MapMode = 5
  Support = -> [XY_Plane005]
  sketch-geometry (12):
    g0: LineSegment StartX=-34 StartY=18 StartZ=0 EndX=34 EndY=18 EndZ=0
    g1: LineSegment StartX=34 StartY=18 StartZ=0 EndX=34 EndY=-18 EndZ=0
    g2: LineSegment StartX=34 StartY=-18 StartZ=0 EndX=-34 EndY=-18 EndZ=0
    g3: LineSegment StartX=-34 StartY=-18 StartZ=0 EndX=-34 EndY=18 EndZ=0
    g4: GeomPoint X=-34 Y=18 Z=0
    g5: GeomPoint X=-29 Y=13 Z=0
    g6: GeomPoint X=29 Y=13 Z=0
    g7: GeomPoint X=34 Y=18 Z=0
    g8: GeomPoint X=34 Y=-18 Z=0
    g9: GeomPoint X=29 Y=-13 Z=0
    g10: GeomPoint X=-29 Y=-13 Z=0
    g11: GeomPoint X=-34 Y=-18 Z=0
  constraints (25):
    c: Coincident(g0,g1)
    c: Coincident(g1,g2)
    c: Coincident(g2,g3)
    c: Coincident(g3,g0)
    c: Horizontal(g0)
    c: Horizontal(g2)
    c: Vertical(g1)
    c: Vertical(g3)
    c: Vertical(g4,g11)
    c: Vertical(g5,g10)
    c: Vertical(g9,g6)
    c: Vertical(g7,g8)
    c: Horizontal(g4,g7)
    c: Horizontal(g6,g5)
    c: Horizontal(g9,g10)
    c: Horizontal(g11,g8)
    c: DistanceX(g5,g6) = 58
    c: DistanceY(g10,g5) = 26
    c: Symmetric(g5,g9,g-1)
    c: Symmetric(g4,g8,g-1)
    c: DistanceY(g5,g4) = 5
    c: DistanceX(g10,g11) = -5
    c: Symmetric(g0,g1,g-1)
    c: DistanceX(g4,g0) = 0
    c: DistanceY(g0,g7) = 0
FEATURE [PartDesign::Pad] Pad015
  Direction = (0,0,1)
  Length = 1
  Length2 = 10
  Profile = -> Sketch027
  ReferenceAxis = -> Sketch027 [N_Axis]
  Type = 0
FEATURE [Sketcher::SketchObject] Sketch028
  FullyConstrained = true
  MapMode = 5
  Placement = pos=(0,0,1) rot=(0,0,1;0rad)
  Support = -> [Pad015]
  sketch-geometry (12):
    g0: GeomPoint X=-29 Y=13 Z=0
    g1: GeomPoint X=29 Y=13 Z=0
    g2: GeomPoint X=29 Y=-13 Z=0
    g3: GeomPoint X=-29 Y=-13 Z=0
    g4: LineSegment StartX=-34 StartY=18 StartZ=0 EndX=34 EndY=18 EndZ=0
    g5: LineSegment StartX=34 StartY=18 StartZ=0 EndX=34 EndY=-18 EndZ=0
    g6: LineSegment StartX=34 StartY=-18 StartZ=0 EndX=-34 EndY=-18 EndZ=0
    g7: LineSegment StartX=-34 StartY=-18 StartZ=0 EndX=-34 EndY=18 EndZ=0
    g8: LineSegment StartX=33 StartY=-17 StartZ=0 EndX=-33 EndY=-17 EndZ=0
    g9: LineSegment StartX=-33 StartY=-17 StartZ=0 EndX=-33 EndY=17 EndZ=0
    g10: LineSegment StartX=-33 StartY=17 StartZ=0 EndX=33 EndY=17 EndZ=0
    g11: LineSegment StartX=33 StartY=17 StartZ=0 EndX=33 EndY=-17 EndZ=0
  constraints (29):
    c: Symmetric(g2,g0,g-1)
    c: Vertical(g3,g0)
    c: Vertical(g2,g1)
    c: Horizontal(g0,g1)
    c: Horizontal(g2,g3)
    c: DistanceX(g0,g1) = 58
    c: DistanceY(g3,g0) = 26
    c: Coincident(g4,g5)
    c: Coincident(g5,g6)
    c: Coincident(g6,g7)
    c: Coincident(g7,g4)
    c: Horizontal(g4)
    c: Horizontal(g6)
    c: Vertical(g5)
    c: Vertical(g7)
    c: Coincident(g8,g9)
    c: Coincident(g9,g10)
    c: Coincident(g10,g11)
    c: Coincident(g11,g8)
    c: Horizontal(g8)
    c: Horizontal(g10)
    c: Vertical(g9)
    c: Vertical(g11)
    c: Symmetric(g9,g8,g-1)
    c: Symmetric(g4,g5,g-1)
    c: DistanceX(g4,g9) = 1
    c: DistanceY(g10,g4) = 1
    c: DistanceX(g4,g0) = 5
    c: DistanceY(g6,g3) = 5
FEATURE [PartDesign::Pad] Pad016
  BaseFeature = -> Pad015
  Direction = (0,0,1)
  Length = 3
  Length2 = 10
  Profile = -> Sketch028
  ReferenceAxis = -> Sketch028 [N_Axis]
  Type = 0
FEATURE [Sketcher::SketchObject] Sketch029
  FullyConstrained = true
  MapMode = 5
  Placement = pos=(0,0,1) rot=(0,0,1;0rad)
  Support = -> [Pad016]
  expr: Constraints[15] = Spreadsheet.C2
  expr: Constraints[16] = Spreadsheet.B2
  sketch-geometry (9):
    g0: GeomPoint X=-29 Y=13 Z=0
    g1: GeomPoint X=29 Y=13 Z=0
    g2: GeomPoint X=29 Y=-13 Z=0
    g3: GeomPoint X=-29 Y=-13 Z=0
    g4: LineSegment StartX=-26.46 StartY=11.23 StartZ=0 EndX=-23.42 EndY=11.23 EndZ=0
    g5: LineSegment StartX=-23.42 StartY=11.23 StartZ=0 EndX=-23.42 EndY=-2.105 EndZ=0
    g6: LineSegment StartX=-23.42 StartY=-2.105 StartZ=0 EndX=-26.46 EndY=-2.105 EndZ=0
    g7: LineSegment StartX=-26.46 StartY=-2.105 StartZ=0 EndX=-26.46 EndY=11.23 EndZ=0
    g8: GeomPoint X=-24.94 Y=-2.105 Z=0
  constraints (20):
    c: Symmetric(g0,g2,g-1)
    c: Horizontal(g0,g1)
    c: Horizontal(g2,g3)
    c: Vertical(g0,g3)
    c: Vertical(g2,g1)
    c: DistanceX(g0,g1) = 58
    c: DistanceY(g3,g0) = 26
    c: Coincident(g4,g5)
    c: Coincident(g5,g6)
    c: Coincident(g6,g7)
    c: Coincident(g7,g4)
    c: Horizontal(g4)
    c: Horizontal(g6)
    c: Vertical(g5)
    c: Vertical(g7)
    c: DistanceX(g4,g4) = 3.04
    c: DistanceY(g7,g7) = 13.335
    c: Symmetric(g6,g5,g8)
    c: DistanceY(g4,g0) = 1.77
    c: DistanceX(g3,g6) = 2.54
FEATURE [PartDesign::Pad] Pad017
  BaseFeature = -> Pad016
  Direction = (0,0,1)
  Length = 3
  Length2 = 10
  Profile = -> Sketch029
  ReferenceAxis = -> Sketch029 [N_Axis]
  Type = 0
FEATURE [Sketcher::SketchObject] Sketch032
  FullyConstrained = true
  MapMode = 5
  Placement = pos=(0,0,1) rot=(0,0,1;0rad)
  Support = -> [Pad017]
  sketch-geometry (12):
    g0: Circle CenterX=-31 CenterY=15 CenterZ=0 NormalX=0 NormalY=0 NormalZ=1 AngleXU=0 Radius=1.5
    g1: Circle CenterX=31 CenterY=15 CenterZ=0 NormalX=0 NormalY=0 NormalZ=1 AngleXU=0 Radius=1.5
    g2: Circle CenterX=-31 CenterY=-15 CenterZ=0 NormalX=0 NormalY=0 NormalZ=1 AngleXU=0 Radius=1.5
    g3: Circle CenterX=31 CenterY=-15 CenterZ=0 NormalX=0 NormalY=0 NormalZ=1 AngleXU=0 Radius=1.5
    g4: GeomPoint X=-29 Y=-13 Z=0
    g5: GeomPoint X=29 Y=-13 Z=0
    g6: GeomPoint X=29 Y=13 Z=0
    g7: GeomPoint X=-29 Y=13 Z=0
    g8: GeomPoint X=-33 Y=-17 Z=0
    g9: GeomPoint X=33 Y=-17 Z=0
    g10: GeomPoint X=33 Y=17 Z=0
    g11: GeomPoint X=-33 Y=17 Z=0
  constraints (24):
    c: Diameter(g0) = 3
    c: Diameter(g1) = 3
    c: Diameter(g2) = 3
    c: Diameter(g3) = 3
    c: Horizontal(g0,g1)
    c: Horizontal(g3,g2)
    c: Vertical(g0,g2)
    c: Vertical(g3,g1)
    c: Horizontal(g4,g5)
    c: Horizontal(g6,g7)
    c: Vertical(g4,g7)
    c: Vertical(g6,g5)
    c: Symmetric(g4,g6,g-1)
    c: Symmetric(g0,g3,g-1)
    c: DistanceX(g7,g6) = 58
    c: DistanceY(g4,g7) = 26
    c: Horizontal(g8,g9)
    c: Horizontal(g10,g11)
    c: Vertical(g8,g11)
    c: Vertical(g10,g9)
    c: Symmetric(g8,g10,g-1)
    c: DistanceX(g11,g7) = 4
    c: DistanceY(g6,g10) = 4
    c: Symmetric(g7,g11,g0)
FEATURE [PartDesign::Pad] Pad020
  BaseFeature = -> Pad017
  Direction = (0,0,1)
  Length = 3
  Length2 = 10
  Profile = -> Sketch032
  ReferenceAxis = -> Sketch032 [N_Axis]
  Type = 0
FEATURE [PartDesign::Body] Body005  label="TopMold"
  Group = -> [Sketch027,Pad015,Sketch028,Pad016,Sketch029,Pad017,Sketch032,Pad020]
  Origin = -> Origin005
  Placement = pos=(100,39,0) rot=(0,0,1;0rad)
  Tip = -> Pad020
FEATURE [Sketcher::SketchObject] Sketch033
  FullyConstrained = true
  MapMode = 5
  Support = -> [XY_Plane007]
  sketch-geometry (12):
    g0: LineSegment StartX=-34 StartY=18 StartZ=0 EndX=34 EndY=18 EndZ=0
    g1: LineSegment StartX=34 StartY=18 StartZ=0 EndX=34 EndY=-18 EndZ=0
    g2: LineSegment StartX=34 StartY=-18 StartZ=0 EndX=-34 EndY=-18 EndZ=0
    g3: LineSegment StartX=-34 StartY=-18 StartZ=0 EndX=-34 EndY=18 EndZ=0
    g4: GeomPoint X=-34 Y=18 Z=0
    g5: GeomPoint X=-29 Y=13 Z=0
    g6: GeomPoint X=29 Y=13 Z=0
    g7: GeomPoint X=34 Y=18 Z=0
    g8: GeomPoint X=34 Y=-18 Z=0
    g9: GeomPoint X=29 Y=-13 Z=0
    g10: GeomPoint X=-29 Y=-13 Z=0
    g11: GeomPoint X=-34 Y=-18 Z=0
  constraints (25):
    c: Coincident(g0,g1)
    c: Coincident(g1,g2)
    c: Coincident(g2,g3)
    c: Coincident(g3,g0)
    c: Horizontal(g0)
    c: Horizontal(g2)
    c: Vertical(g1)
    c: Vertical(g3)
    c: Vertical(g4,g11)
    c: Vertical(g5,g10)
    c: Vertical(g9,g6)
    c: Vertical(g7,g8)
    c: Horizontal(g4,g7)
    c: Horizontal(g6,g5)
    c: Horizontal(g9,g10)
    c: Horizontal(g11,g8)
    c: DistanceX(g5,g6) = 58
    c: DistanceY(g10,g5) = 26
    c: Symmetric(g5,g9,g-1)
    c: Symmetric(g4,g8,g-1)
    c: DistanceY(g5,g4) = 5
    c: DistanceX(g10,g11) = -5
    c: Symmetric(g0,g1,g-1)
    c: DistanceX(g4,g0) = 0
    c: DistanceY(g0,g7) = 0
FEATURE [PartDesign::Pad] Pad021
  Direction = (0,0,1)
  Length = 1
  Length2 = 10
  Profile = -> Sketch033
  ReferenceAxis = -> Sketch033 [N_Axis]
  Type = 0
FEATURE [Sketcher::SketchObject] Sketch034
  FullyConstrained = true
  MapMode = 5
  Placement = pos=(0,0,1) rot=(0,0,1;0rad)
  Support = -> [Pad021]
  sketch-geometry (12):
    g0: GeomPoint X=-29 Y=13 Z=0
    g1: GeomPoint X=29 Y=13 Z=0
    g2: GeomPoint X=29 Y=-13 Z=0
    g3: GeomPoint X=-29 Y=-13 Z=0
    g4: LineSegment StartX=-34 StartY=18 StartZ=0 EndX=34 EndY=18 EndZ=0
    g5: LineSegment StartX=34 StartY=18 StartZ=0 EndX=34 EndY=-18 EndZ=0
    g6: LineSegment StartX=34 StartY=-18 StartZ=0 EndX=-34 EndY=-18 EndZ=0
    g7: LineSegment StartX=-34 StartY=-18 StartZ=0 EndX=-34 EndY=18 EndZ=0
    g8: LineSegment StartX=33 StartY=-17 StartZ=0 EndX=-33 EndY=-17 EndZ=0
    g9: LineSegment StartX=-33 StartY=-17 StartZ=0 EndX=-33 EndY=17 EndZ=0
    g10: LineSegment StartX=-33 StartY=17 StartZ=0 EndX=33 EndY=17 EndZ=0
    g11: LineSegment StartX=33 StartY=17 StartZ=0 EndX=33 EndY=-17 EndZ=0
  constraints (29):
    c: Symmetric(g2,g0,g-1)
    c: Vertical(g3,g0)
    c: Vertical(g2,g1)
    c: Horizontal(g0,g1)
    c: Horizontal(g2,g3)
    c: DistanceX(g0,g1) = 58
    c: DistanceY(g3,g0) = 26
    c: Coincident(g4,g5)
    c: Coincident(g5,g6)
    c: Coincident(g6,g7)
    c: Coincident(g7,g4)
    c: Horizontal(g4)
    c: Horizontal(g6)
    c: Vertical(g5)
    c: Vertical(g7)
    c: Coincident(g8,g9)
    c: Coincident(g9,g10)
    c: Coincident(g10,g11)
    c: Coincident(g11,g8)
    c: Horizontal(g8)
    c: Horizontal(g10)
    c: Vertical(g9)
    c: Vertical(g11)
    c: Symmetric(g9,g8,g-1)
    c: Symmetric(g4,g5,g-1)
    c: DistanceX(g4,g9) = 1
    c: DistanceY(g10,g4) = 1
    c: DistanceX(g4,g0) = 5
    c: DistanceY(g6,g3) = 5
FEATURE [PartDesign::Pad] Pad022
  BaseFeature = -> Pad021
  Direction = (0,0,1)
  Length = 3
  Length2 = 10
  Profile = -> Sketch034
  ReferenceAxis = -> Sketch034 [N_Axis]
  Type = 0
FEATURE [Sketcher::SketchObject] Sketch036
  FullyConstrained = true
  MapMode = 5
  Placement = pos=(0,0,1) rot=(0,0,1;0rad)
  sketch-geometry (12):
    g0: Circle CenterX=-31 CenterY=15 CenterZ=0 NormalX=0 NormalY=0 NormalZ=1 AngleXU=0 Radius=1.5
    g1: Circle CenterX=31 CenterY=15 CenterZ=0 NormalX=0 NormalY=0 NormalZ=1 AngleXU=0 Radius=1.5
    g2: Circle CenterX=-31 CenterY=-15 CenterZ=0 NormalX=0 NormalY=0 NormalZ=1 AngleXU=0 Radius=1.5
    g3: Circle CenterX=31 CenterY=-15 CenterZ=0 NormalX=0 NormalY=0 NormalZ=1 AngleXU=0 Radius=1.5
    g4: GeomPoint X=-29 Y=-13 Z=0
    g5: GeomPoint X=29 Y=-13 Z=0
    g6: GeomPoint X=29 Y=13 Z=0
    g7: GeomPoint X=-29 Y=13 Z=0
    g8: GeomPoint X=-33 Y=-17 Z=0
    g9: GeomPoint X=33 Y=-17 Z=0
    g10: GeomPoint X=33 Y=17 Z=0
    g11: GeomPoint X=-33 Y=17 Z=0
  constraints (24):
    c: Diameter(g0) = 3
    c: Diameter(g1) = 3
    c: Diameter(g2) = 3
    c: Diameter(g3) = 3
    c: Horizontal(g0,g1)
    c: Horizontal(g3,g2)
    c: Vertical(g0,g2)
    c: Vertical(g3,g1)
    c: Horizontal(g4,g5)
    c: Horizontal(g6,g7)
    c: Vertical(g4,g7)
    c: Vertical(g6,g5)
    c: Symmetric(g4,g6,g-1)
    c: Symmetric(g0,g3,g-1)
    c: DistanceX(g7,g6) = 58
    c: DistanceY(g4,g7) = 26
    c: Horizontal(g8,g9)
    c: Horizontal(g10,g11)
    c: Vertical(g8,g11)
    c: Vertical(g10,g9)
    c: Symmetric(g8,g10,g-1)
    c: DistanceX(g11,g7) = 4
    c: DistanceY(g6,g10) = 4
    c: Symmetric(g7,g11,g0)
FEATURE [PartDesign::Pad] Pad024
  BaseFeature = -> Pad022
  Direction = (0,0,1)
  Length = 3
  Length2 = 10
  Profile = -> Sketch036
  ReferenceAxis = -> Sketch036 [N_Axis]
  Type = 0
FEATURE [PartDesign::Body] Body007  label="BottomMold"
  Group = -> [Sketch033,Pad021,Sketch034,Pad022,Sketch036,Pad024]
  Origin = -> Origin007
  Placement = pos=(100,78,0) rot=(0,0,1;0rad)
  Tip = -> Pad024
FEATURE [Sketcher::SketchObject] Sketch040
  FullyConstrained = true
  MapMode = 5
  Placement = pos=(0,0,3) rot=(0,0,1;0rad)
  expr: Constraints[16] = 17.11
  sketch-geometry (8):
    g0: Circle CenterX=-32.89 CenterY=32.89 CenterZ=0 NormalX=0 NormalY=0 NormalZ=1 AngleXU=0 Radius=1.5
    g1: Circle CenterX=32.89 CenterY=32.89 CenterZ=0 NormalX=0 NormalY=0 NormalZ=1 AngleXU=0 Radius=1.5
    g2: Circle CenterX=-32.89 CenterY=-32.89 CenterZ=0 NormalX=0 NormalY=0 NormalZ=1 AngleXU=0 Radius=1.5
    g3: Circle CenterX=32.89 CenterY=-32.89 CenterZ=0 NormalX=0 NormalY=0 NormalZ=1 AngleXU=0 Radius=1.5
    g4: GeomPoint X=-50 Y=50 Z=0
    g5: GeomPoint X=50 Y=50 Z=0
    g6: GeomPoint X=50 Y=-50 Z=0
    g7: GeomPoint X=-50 Y=-50 Z=0
  constraints (18):
    c: Diameter(g0) = 3
    c: Diameter(g1) = 3
    c: Horizontal(g0,g1)
    c: Diameter(g2) = 3
    c: Diameter(g3) = 3
    c: Vertical(g2,g0)
    c: Vertical(g3,g1)
    c: Horizontal(g2,g3)
    c: Symmetric(g0,g3,g-1)
    c: Horizontal(g5,g4)
    c: Horizontal(g7,g6)
    c: Vertical(g4,g7)
    c: Vertical(g6,g5)
    c: DistanceX(g4,g5) = 100
    c: DistanceY(g7,g4) = 100
    c: Symmetric(g4,g6,g-1)
    c: DistanceX(g4,g0) = 17.11
    c: DistanceY(g0,g4) = 17.11
FEATURE [Sketcher::SketchObject] Sketch041
  FullyConstrained = true
  MapMode = 5
  Placement = pos=(0,0,3) rot=(0,0,1;0rad)
  expr: Constraints[16] = 17.11
  sketch-geometry (8):
    g0: Circle CenterX=-32.89 CenterY=32.89 CenterZ=0 NormalX=0 NormalY=0 NormalZ=1 AngleXU=0 Radius=1.5
    g1: Circle CenterX=32.89 CenterY=32.89 CenterZ=0 NormalX=0 NormalY=0 NormalZ=1 AngleXU=0 Radius=1.5
    g2: Circle CenterX=-32.89 CenterY=-32.89 CenterZ=0 NormalX=0 NormalY=0 NormalZ=1 AngleXU=0 Radius=1.5
    g3: Circle CenterX=32.89 CenterY=-32.89 CenterZ=0 NormalX=0 NormalY=0 NormalZ=1 AngleXU=0 Radius=1.5
    g4: GeomPoint X=-50 Y=50 Z=0
    g5: GeomPoint X=50 Y=50 Z=0
    g6: GeomPoint X=50 Y=-50 Z=0
    g7: GeomPoint X=-50 Y=-50 Z=0
  constraints (18):
    c: Diameter(g0) = 3
    c: Diameter(g1) = 3
    c: Horizontal(g0,g1)
    c: Diameter(g2) = 3
    c: Diameter(g3) = 3
    c: Vertical(g2,g0)
    c: Vertical(g3,g1)
    c: Horizontal(g2,g3)
    c: Symmetric(g0,g3,g-1)
    c: Horizontal(g5,g4)
    c: Horizontal(g7,g6)
    c: Vertical(g4,g7)
    c: Vertical(g6,g5)
    c: DistanceX(g4,g5) = 100
    c: DistanceY(g7,g4) = 100
    c: Symmetric(g4,g6,g-1)
    c: DistanceX(g4,g0) = 17.11
    c: DistanceY(g0,g4) = 17.11
FEATURE [PartDesign::Pocket] Pocket006
  BaseFeature = -> Pad007
  Direction = (0,0,-1)
  Length = 5
  Length2 = 5
  Profile = -> Sketch041
  ReferenceAxis = -> Sketch041 [N_Axis]
  Type = 1
FEATURE [PartDesign::Body] Body  label="Microcontroller & Power Stack Plate"
  Group = -> [Sketch,Pad,Sketch002,Sketch004,Pocket,Pad003,Sketch005,Sketch009,Pocket002,Pad006,Sketch010,Sketch016,Pocket003,Pad007,Sketch041,Pocket006]
  Origin = -> Origin
  Placement = pos=(0,0,18) rot=(0,0,1;0rad)
  Tip = -> Pocket006
FEATURE [App::DocumentObjectGroup] Group013  label="Microcontroller & Power"
  Group = -> [Body]
FEATURE [PartDesign::Pocket] Pocket007
  BaseFeature = -> Pad009
  Direction = (0,0,-1)
  Length = 5
  Length2 = 5
  Profile = -> Sketch040
  ReferenceAxis = -> Sketch040 [N_Axis]
  Type = 1
FEATURE [Sketcher::SketchObject] Sketch023
  FullyConstrained = true
  MapMode = 5
  Support = -> [XY_Plane003]
  expr: Constraints[17] = <<GeigerVariables>>.C2
  expr: Constraints[18] = <<GeigerVariables>>.B2
  sketch-geometry (13):
    g0: LineSegment StartX=-34 StartY=18 StartZ=0 EndX=34 EndY=18 EndZ=0
    g1: LineSegment StartX=34 StartY=18 StartZ=0 EndX=34 EndY=-18 EndZ=0
    g2: LineSegment StartX=34 StartY=-18 StartZ=0 EndX=-34 EndY=-18 EndZ=0
    g3: LineSegment StartX=-34 StartY=-18 StartZ=0 EndX=-34 EndY=18 EndZ=0
    g4: LineSegment StartX=-26.46 StartY=11.23 StartZ=0 EndX=-23.42 EndY=11.23 EndZ=0
    g5: LineSegment StartX=-23.42 StartY=11.23 StartZ=0 EndX=-23.42 EndY=-2.105 EndZ=0
    g6: LineSegment StartX=-23.42 StartY=-2.105 StartZ=0 EndX=-26.46 EndY=-2.105 EndZ=0
    g7: LineSegment StartX=-26.46 StartY=-2.105 StartZ=0 EndX=-26.46 EndY=11.23 EndZ=0
    g8: GeomPoint X=-29 Y=13 Z=0
    g9: GeomPoint X=29 Y=13 Z=0
    g10: GeomPoint X=29 Y=-13 Z=0
    g11: GeomPoint X=-29 Y=-13 Z=0
    g12: GeomPoint X=-24.94 Y=-2.105 Z=0
  constraints (32):
    c: Coincident(g0,g1)
    c: Coincident(g1,g2)
    c: Coincident(g2,g3)
    c: Coincident(g3,g0)
    c: Horizontal(g0)
    c: Horizontal(g2)
    c: Vertical(g1)
    c: Vertical(g3)
    c: Symmetric(g0,g1,g-1)
    c: Coincident(g4,g5)
    c: Coincident(g5,g6)
    c: Coincident(g6,g7)
    c: Coincident(g7,g4)
    c: Horizontal(g4)
    c: Horizontal(g6)
    c: Vertical(g5)
    c: Vertical(g7)
    c: DistanceX(g4,g4) = 3.04
    c: DistanceY(g7,g7) = 13.335
    c: Horizontal(g8,g9)
    c: Horizontal(g10,g11)
    c: Vertical(g11,g8)
    c: Vertical(g10,g9)
    c: DistanceX(g8,g9) = 58
    c: DistanceY(g11,g8) = 26
    c: Symmetric(g5,g6,g12)
    c: DistanceX(g0,g8) = 5
    c: DistanceX(g0,g9) = -5
    c: DistanceY(g8,g0) = 5
    c: DistanceY(g1,g10) = 5
    c: DistanceY(g4,g8) = 1.77
    c: DistanceX(g11,g6) = 2.54
FEATURE [PartDesign::Pad] Pad011
  Direction = (0,0,1)
  Length = 1
  Length2 = 10
  Profile = -> Sketch023
  ReferenceAxis = -> Sketch023 [N_Axis]
  Type = 0
FEATURE [Sketcher::SketchObject] Sketch024
  FullyConstrained = true
  MapMode = 5
  Placement = pos=(0,0,1) rot=(0,0,1;0rad)
  Support = -> [Pad011]
  sketch-geometry (12):
    g0: GeomPoint X=-29 Y=13 Z=0
    g1: GeomPoint X=29 Y=13 Z=0
    g2: GeomPoint X=29 Y=-13 Z=0
    g3: GeomPoint X=-29 Y=-13 Z=0
    g4: LineSegment StartX=-34 StartY=18 StartZ=0 EndX=34 EndY=18 EndZ=0
    g5: LineSegment StartX=34 StartY=18 StartZ=0 EndX=34 EndY=-18 EndZ=0
    g6: LineSegment StartX=34 StartY=-18 StartZ=0 EndX=-34 EndY=-18 EndZ=0
    g7: LineSegment StartX=-34 StartY=-18 StartZ=0 EndX=-34 EndY=18 EndZ=0
    g8: LineSegment StartX=-33 StartY=17 StartZ=0 EndX=33 EndY=17 EndZ=0
    g9: LineSegment StartX=33 StartY=17 StartZ=0 EndX=33 EndY=-17 EndZ=0
    g10: LineSegment StartX=33 StartY=-17 StartZ=0 EndX=-33 EndY=-17 EndZ=0
    g11: LineSegment StartX=-33 StartY=-17 StartZ=0 EndX=-33 EndY=17 EndZ=0
  constraints (31):
    c: Horizontal(g0,g1)
    c: Horizontal(g2,g3)
    c: Vertical(g0,g3)
    c: Vertical(g2,g1)
    c: DistanceX(g0,g1) = 58
    c: DistanceY(g3,g0) = 26
    c: Symmetric(g0,g2,g-1)
    c: Coincident(g4,g5)
    c: Coincident(g5,g6)
    c: Coincident(g6,g7)
    c: Coincident(g7,g4)
    c: Horizontal(g4)
    c: Horizontal(g6)
    c: Vertical(g5)
    c: Vertical(g7)
    c: DistanceX(g4,g3) = 5
    c: DistanceX(g1,g4) = 5
    c: DistanceY(g1,g4) = 5
    c: DistanceY(g5,g2) = 5
    c: Coincident(g8,g9)
    c: Coincident(g9,g10)
    c: Coincident(g10,g11)
    c: Coincident(g11,g8)
    c: Horizontal(g8)
    c: Horizontal(g10)
    c: Vertical(g9)
    c: Vertical(g11)
    c: DistanceX(g8,g4) = 1
    c: DistanceX(g4,g8) = 1
    c: DistanceY(g8,g4) = 1
    c: DistanceY(g6,g10) = 1
FEATURE [PartDesign::Pad] Pad012
  BaseFeature = -> Pad011
  Direction = (0,0,1)
  Length = 13
  Length2 = 10
  Profile = -> Sketch024
  ReferenceAxis = -> Sketch024 [N_Axis]
  Type = 0
FEATURE [Sketcher::SketchObject] Sketch039
  FullyConstrained = true
  MapMode = 5
  Placement = pos=(0,0,1) rot=(0,0,1;0rad)
  Support = -> [Pad012]
  sketch-geometry (12):
    g0: Circle CenterX=-31 CenterY=15 CenterZ=0 NormalX=0 NormalY=0 NormalZ=1 AngleXU=0 Radius=1.5
    g1: Circle CenterX=31 CenterY=15 CenterZ=0 NormalX=0 NormalY=0 NormalZ=1 AngleXU=0 Radius=1.5
    g2: Circle CenterX=31 CenterY=-15 CenterZ=0 NormalX=0 NormalY=0 NormalZ=1 AngleXU=0 Radius=1.5
    g3: Circle CenterX=-31 CenterY=-15 CenterZ=0 NormalX=0 NormalY=0 NormalZ=1 AngleXU=0 Radius=1.5
    g4: GeomPoint X=-29 Y=13 Z=0
    g5: GeomPoint X=29 Y=13 Z=0
    g6: GeomPoint X=29 Y=-13 Z=0
    g7: GeomPoint X=-29 Y=-13 Z=0
    g8: GeomPoint X=-33 Y=17 Z=0
    g9: GeomPoint X=33 Y=17 Z=0
    g10: GeomPoint X=33 Y=-17 Z=0
    g11: GeomPoint X=-33 Y=-17 Z=0
  constraints (24):
    c: Symmetric(g0,g2,g-1)
    c: Horizontal(g0,g1)
    c: Horizontal(g2,g3)
    c: Vertical(g0,g3)
    c: Vertical(g2,g1)
    c: Symmetric(g4,g6,g-1)
    c: Horizontal(g4,g5)
    c: Horizontal(g6,g7)
    c: Vertical(g4,g7)
    c: Vertical(g6,g5)
    c: DistanceX(g4,g5) = 58
    c: DistanceY(g7,g4) = 26
    c: Symmetric(g8,g10,g-1)
    c: Vertical(g8,g11)
    c: Vertical(g10,g9)
    c: Horizontal(g8,g9)
    c: Horizontal(g10,g11)
    c: DistanceX(g8,g4) = 4
    c: Diameter(g0) = 3
    c: Diameter(g1) = 3
    c: Diameter(g2) = 3
    c: Diameter(g3) = 3
    c: DistanceY(g11,g7) = 4
    c: Symmetric(g4,g8,g0)
FEATURE [PartDesign::Pocket] Pocket005
  BaseFeature = -> Pad012
  Direction = (0,0,-1)
  Length = 5
  Length2 = 5
  Profile = -> Sketch039
  ReferenceAxis = -> Sketch039 [N_Axis]
  Type = 1
FEATURE [PartDesign::Body] Body003  label="Geiger Cover Outer"
  Group = -> [Sketch023,Pad011,Sketch024,Pad012,Sketch039,Pocket005]
  Origin = -> Origin003
  Placement = pos=(100,0,0) rot=(0,0,1;0rad)
  Tip = -> Pocket005
FEATURE [Sketcher::SketchObject] Sketch025
  FullyConstrained = true
  MapMode = 5
  Support = -> [XY_Plane004]
  expr: Constraints[26] = Spreadsheet.B2
  expr: Constraints[27] = Spreadsheet.C2
  sketch-geometry (13):
    g0: GeomPoint X=-29 Y=13 Z=0
    g1: GeomPoint X=29 Y=13 Z=0
    g2: GeomPoint X=29 Y=-13 Z=0
    g3: GeomPoint X=-29 Y=-13 Z=0
    g4: LineSegment StartX=-30 StartY=14 StartZ=0 EndX=30 EndY=14 EndZ=0
    g5: LineSegment StartX=30 StartY=14 StartZ=0 EndX=30 EndY=-14 EndZ=0
    g6: LineSegment StartX=30 StartY=-14 StartZ=0 EndX=-30 EndY=-14 EndZ=0
    g7: LineSegment StartX=-30 StartY=-14 StartZ=0 EndX=-30 EndY=14 EndZ=0
    g8: LineSegment StartX=-26.46 StartY=11.23 StartZ=0 EndX=-23.42 EndY=11.23 EndZ=0
    g9: LineSegment StartX=-23.42 StartY=11.23 StartZ=0 EndX=-23.42 EndY=-2.105 EndZ=0
    g10: LineSegment StartX=-23.42 StartY=-2.105 StartZ=0 EndX=-26.46 EndY=-2.105 EndZ=0
    g11: LineSegment StartX=-26.46 StartY=-2.105 StartZ=0 EndX=-26.46 EndY=11.23 EndZ=0
    g12: GeomPoint X=-24.94 Y=-2.105 Z=0
  constraints (31):
    c: Horizontal(g0,g1)
    c: Horizontal(g2,g3)
    c: Vertical(g0,g3)
    c: Vertical(g2,g1)
    c: DistanceX(g0,g1) = 58
    c: DistanceY(g3,g0) = 26
    c: Symmetric(g0,g2,g-1)
    c: Coincident(g4,g5)
    c: Coincident(g5,g6)
    c: Coincident(g6,g7)
    c: Coincident(g7,g4)
    c: Horizontal(g4)
    c: Horizontal(g6)
    c: Vertical(g5)
    c: Vertical(g7)
    c: Symmetric(g4,g5,g-1)
    c: DistanceX(g4,g0) = 1
    c: DistanceY(g1,g4) = 1
    c: Coincident(g8,g9)
    c: Coincident(g9,g10)
    c: Coincident(g10,g11)
    c: Coincident(g11,g8)
    c: Horizontal(g8)
    c: Horizontal(g10)
    c: Vertical(g9)
    c: Vertical(g11)
    c: DistanceY(g11,g11) = 13.335
    c: DistanceX(g8,g8) = 3.04
    c: Symmetric(g10,g9,g12)
    c: DistanceY(g8,g0) = 1.77
    c: DistanceX(g3,g10) = 2.54
FEATURE [PartDesign::Pad] Pad013
  Direction = (0,0,1)
  Length = 1
  Length2 = 10
  Profile = -> Sketch025
  ReferenceAxis = -> Sketch025 [N_Axis]
  Type = 0
FEATURE [Sketcher::SketchObject] Sketch026
  FullyConstrained = true
  MapMode = 5
  Placement = pos=(0,0,1) rot=(0,0,1;0rad)
  Support = -> [Pad013]
  sketch-geometry (8):
    g0: LineSegment StartX=-29 StartY=13 StartZ=0 EndX=29 EndY=13 EndZ=0
    g1: LineSegment StartX=29 StartY=13 StartZ=0 EndX=29 EndY=-13 EndZ=0
    g2: LineSegment StartX=29 StartY=-13 StartZ=0 EndX=-29 EndY=-13 EndZ=0
    g3: LineSegment StartX=-29 StartY=-13 StartZ=0 EndX=-29 EndY=13 EndZ=0
    g4: LineSegment StartX=-30 StartY=14 StartZ=0 EndX=30 EndY=14 EndZ=0
    g5: LineSegment StartX=30 StartY=14 StartZ=0 EndX=30 EndY=-14 EndZ=0
    g6: LineSegment StartX=30 StartY=-14 StartZ=0 EndX=-30 EndY=-14 EndZ=0
    g7: LineSegment StartX=-30 StartY=-14 StartZ=0 EndX=-30 EndY=14 EndZ=0
  constraints (22):
    c: Coincident(g0,g1)
    c: Coincident(g1,g2)
    c: Coincident(g2,g3)
    c: Coincident(g3,g0)
    c: Horizontal(g0)
    c: Horizontal(g2)
    c: Vertical(g1)
    c: Vertical(g3)
    c: Symmetric(g0,g1,g-1)
    c: DistanceX(g0,g0) = 58
    c: DistanceY(g3,g3) = 26
    c: Coincident(g4,g5)
    c: Coincident(g5,g6)
    c: Coincident(g6,g7)
    c: Coincident(g7,g4)
    c: Horizontal(g4)
    c: Horizontal(g6)
    c: Vertical(g5)
    c: Vertical(g7)
    c: DistanceX(g1,g5) = 1
    c: DistanceY(g0,g4) = 1
    c: Symmetric(g4,g5,g-1)
FEATURE [PartDesign::Pad] Pad014
  BaseFeature = -> Pad013
  Direction = (0,0,1)
  Length = 6
  Length2 = 10
  Profile = -> Sketch026
  ReferenceAxis = -> Sketch026 [N_Axis]
  Type = 0
FEATURE [PartDesign::Body] Body004  label="Geiger Cover Inner"
  Group = -> [Sketch025,Pad013,Sketch026,Pad014]
  Origin = -> Origin004
  Placement = pos=(100,0,4) rot=(0,0,1;0rad)
  Tip = -> Pad014
FEATURE [Spreadsheet::Sheet] Spreadsheet  label="GeigerVariables"
  cells = B1=Length; C1=Width; A2=Header Hole; B2=13.335; C2=3.04
FEATURE [Sketcher::SketchObject] Sketch042
  FullyConstrained = true
  MapMode = 5
  Support = -> [XY_Plane009]
  sketch-geometry (8):
    g0: LineSegment StartX=-4.5 StartY=14 StartZ=0 EndX=4.5 EndY=14 EndZ=0
    g1: LineSegment StartX=4.5 StartY=14 StartZ=0 EndX=4.5 EndY=-14 EndZ=0
    g2: LineSegment StartX=4.5 StartY=-14 StartZ=0 EndX=-4.5 EndY=-14 EndZ=0
    g3: LineSegment StartX=-4.5 StartY=-14 StartZ=0 EndX=-4.5 EndY=14 EndZ=0
    g4: GeomPoint X=-3.5 Y=13 Z=0
    g5: GeomPoint X=3.5 Y=13 Z=0
    g6: GeomPoint X=3.5 Y=-13 Z=0
    g7: GeomPoint X=-3.5 Y=-13 Z=0
  constraints (18):
    c: Coincident(g0,g1)
    c: Coincident(g1,g2)
    c: Coincident(g2,g3)
    c: Coincident(g3,g0)
    c: Horizontal(g0)
    c: Horizontal(g2)
    c: Vertical(g1)
    c: Vertical(g3)
    c: Symmetric(g0,g1,g-1)
    c: Horizontal(g7,g6)
    c: Horizontal(g5,g4)
    c: Vertical(g4,g7)
    c: Vertical(g6,g5)
    c: DistanceX(g4,g5) = 7
    c: DistanceY(g7,g4) = 26
    c: Symmetric(g4,g6,g-1)
    c: DistanceX(g0,g4) = 1
    c: DistanceY(g4,g0) = 1
FEATURE [PartDesign::Pad] Pad027
  Direction = (0,0,1)
  Length = 1
  Length2 = 10
  Profile = -> Sketch042
  ReferenceAxis = -> Sketch042 [N_Axis]
  Type = 0
FEATURE [Sketcher::SketchObject] Sketch043
  FullyConstrained = true
  MapMode = 5
  Placement = pos=(0,0,1) rot=(0,0,1;0rad)
  Support = -> [Pad027]
  sketch-geometry (8):
    g0: LineSegment StartX=-4.5 StartY=14 StartZ=0 EndX=4.5 EndY=14 EndZ=0
    g1: LineSegment StartX=4.5 StartY=14 StartZ=0 EndX=4.5 EndY=-14 EndZ=0
    g2: LineSegment StartX=4.5 StartY=-14 StartZ=0 EndX=-4.5 EndY=-14 EndZ=0
    g3: LineSegment StartX=-4.5 StartY=-14 StartZ=0 EndX=-4.5 EndY=14 EndZ=0
    g4: LineSegment StartX=-3.5 StartY=13 StartZ=0 EndX=3.5 EndY=13 EndZ=0
    g5: LineSegment StartX=3.5 StartY=13 StartZ=0 EndX=3.5 EndY=-13 EndZ=0
    g6: LineSegment StartX=3.5 StartY=-13 StartZ=0 EndX=-3.5 EndY=-13 EndZ=0
    g7: LineSegment StartX=-3.5 StartY=-13 StartZ=0 EndX=-3.5 EndY=13 EndZ=0
  constraints (22):
    c: Coincident(g0,g1)
    c: Coincident(g1,g2)
    c: Coincident(g2,g3)
    c: Coincident(g3,g0)
    c: Horizontal(g0)
    c: Horizontal(g2)
    c: Vertical(g1)
    c: Vertical(g3)
    c: Symmetric(g0,g1,g-1)
    c: Coincident(g4,g5)
    c: Coincident(g5,g6)
    c: Coincident(g6,g7)
    c: Coincident(g7,g4)
    c: Horizontal(g4)
    c: Horizontal(g6)
    c: Vertical(g5)
    c: Vertical(g7)
    c: DistanceX(g0,g4) = 1
    c: DistanceY(g4,g0) = 1
    c: Symmetric(g4,g5,g-1)
    c: DistanceX(g4,g4) = 7
    c: DistanceY(g7,g7) = 26
FEATURE [PartDesign::Pad] Pad028
  BaseFeature = -> Pad027
  Direction = (0,0,1)
  Length = 3
  Length2 = 10
  Profile = -> Sketch043
  ReferenceAxis = -> Sketch043 [N_Axis]
  Type = 0
FEATURE [PartDesign::Body] Body009  label="SideMold"
  Group = -> [Sketch042,Pad027,Sketch043,Pad028]
  Origin = -> Origin009
  Placement = pos=(150,35,0) rot=(0,0,1;0rad)
  Tip = -> Pad028
FEATURE [Sketcher::SketchObject] Sketch046
  FullyConstrained = true
  MapMode = 5
  Placement = pos=(0,0,3) rot=(0,0,1;0rad)
  Support = -> [Pocket007]
  sketch-geometry (13):
    g0: GeomPoint X=-1 Y=28 Z=0
    g1: GeomPoint X=25 Y=28 Z=0
    g2: GeomPoint X=25 Y=-30 Z=0
    g3: GeomPoint X=-1 Y=-30 Z=0
    g4: GeomPoint X=-5 Y=32 Z=0
    g5: GeomPoint X=29 Y=32 Z=0
    g6: GeomPoint X=29 Y=-34 Z=0
    g7: GeomPoint X=-5 Y=-34 Z=0
    g8: GeomPoint X=-1 Y=-1 Z=0
    g9: Circle CenterX=-3 CenterY=30 CenterZ=0 NormalX=0 NormalY=0 NormalZ=1 AngleXU=0 Radius=1.5
    g10: Circle CenterX=27 CenterY=30 CenterZ=0 NormalX=0 NormalY=0 NormalZ=1 AngleXU=0 Radius=1.5
    g11: Circle CenterX=-3 CenterY=-32 CenterZ=0 NormalX=0 NormalY=0 NormalZ=1 AngleXU=0 Radius=1.5
    g12: Circle CenterX=27 CenterY=-32 CenterZ=0 NormalX=0 NormalY=0 NormalZ=1 AngleXU=0 Radius=1.5
  constraints (25):
    c: Horizontal(g0,g1)
    c: Horizontal(g3,g2)
    c: Horizontal(g6,g7)
    c: Horizontal(g5,g4)
    c: Vertical(g4,g7)
    c: Vertical(g6,g5)
    c: Vertical(g1,g2)
    c: Vertical(g3,g0)
    c: DistanceX(g4,g0) = 4
    c: DistanceY(g1,g5) = 4
    c: DistanceY(g6,g2) = 4
    c: DistanceX(g2,g6) = 4
    c: DistanceX(g0,g1) = 26
    c: DistanceY(g3,g0) = 58
    c: Diameter(g9) = 3
    c: Symmetric(g3,g7,g11)
    c: Symmetric(g2,g6,g12)
    c: Symmetric(g5,g1,g10)
    c: Symmetric(g4,g0,g9)
    c: Diameter(g12) = 3
    c: Diameter(g11) = 3
    c: Diameter(g10) = 3
    c: DistanceX(g8,g-1) = 1
    c: DistanceY(g8,g-1) = 1
    c: Symmetric(g0,g3,g8)
FEATURE [PartDesign::Pocket] Pocket008
  BaseFeature = -> Pocket007
  Direction = (0,0,-1)
  Length = 5
  Length2 = 5
  Profile = -> Sketch046
  ReferenceAxis = -> Sketch046 [N_Axis]
  Type = 1
FEATURE [Sketcher::SketchObject] Sketch049
  FullyConstrained = true
  MapMode = 5
  Support = -> [XY_Plane013]
  expr: Constraints[17] = <<GeigerVariables001>>.C2
  expr: Constraints[18] = <<GeigerVariables001>>.B2
  sketch-geometry (13):
    g0: LineSegment StartX=-34 StartY=18 StartZ=0 EndX=34 EndY=18 EndZ=0
    g1: LineSegment StartX=34 StartY=18 StartZ=0 EndX=34 EndY=-18 EndZ=0
    g2: LineSegment StartX=34 StartY=-18 StartZ=0 EndX=-34 EndY=-18 EndZ=0
    g3: LineSegment StartX=-34 StartY=-18 StartZ=0 EndX=-34 EndY=18 EndZ=0
    g4: LineSegment StartX=-26.46 StartY=11.23 StartZ=0 EndX=-23.42 EndY=11.23 EndZ=0
    g5: LineSegment StartX=-23.42 StartY=11.23 StartZ=0 EndX=-23.42 EndY=-2.105 EndZ=0
    g6: LineSegment StartX=-23.42 StartY=-2.105 StartZ=0 EndX=-26.46 EndY=-2.105 EndZ=0
    g7: LineSegment StartX=-26.46 StartY=-2.105 StartZ=0 EndX=-26.46 EndY=11.23 EndZ=0
    g8: GeomPoint X=-29 Y=13 Z=0
    g9: GeomPoint X=29 Y=13 Z=0
    g10: GeomPoint X=29 Y=-13 Z=0
    g11: GeomPoint X=-29 Y=-13 Z=0
    g12: GeomPoint X=-24.94 Y=-2.105 Z=0
  constraints (32):
    c: Coincident(g0,g1)
    c: Coincident(g1,g2)
    c: Coincident(g2,g3)
    c: Coincident(g3,g0)
    c: Horizontal(g0)
    c: Horizontal(g2)
    c: Vertical(g1)
    c: Vertical(g3)
    c: Symmetric(g0,g1,g-1)
    c: Coincident(g4,g5)
    c: Coincident(g5,g6)
    c: Coincident(g6,g7)
    c: Coincident(g7,g4)
    c: Horizontal(g4)
    c: Horizontal(g6)
    c: Vertical(g5)
    c: Vertical(g7)
    c: DistanceX(g4,g4) = 3.04
    c: DistanceY(g7,g7) = 13.335
    c: Horizontal(g8,g9)
    c: Horizontal(g10,g11)
    c: Vertical(g11,g8)
    c: Vertical(g10,g9)
    c: DistanceX(g8,g9) = 58
    c: DistanceY(g11,g8) = 26
    c: Symmetric(g5,g6,g12)
    c: DistanceX(g0,g8) = 5
    c: DistanceX(g0,g9) = -5
    c: DistanceY(g8,g0) = 5
    c: DistanceY(g1,g10) = 5
    c: DistanceY(g4,g8) = 1.77
    c: DistanceX(g11,g6) = 2.54
FEATURE [PartDesign::Pad] Pad032
  Direction = (0,0,1)
  Length = 1
  Length2 = 10
  Profile = -> Sketch049
  ReferenceAxis = -> Sketch049 [N_Axis]
  Type = 0
FEATURE [Sketcher::SketchObject] Sketch050
  FullyConstrained = true
  MapMode = 5
  Placement = pos=(0,0,1) rot=(0,0,1;0rad)
  Support = -> [Pad032]
  sketch-geometry (12):
    g0: GeomPoint X=-29 Y=13 Z=0
    g1: GeomPoint X=29 Y=13 Z=0
    g2: GeomPoint X=29 Y=-13 Z=0
    g3: GeomPoint X=-29 Y=-13 Z=0
    g4: LineSegment StartX=-34 StartY=18 StartZ=0 EndX=34 EndY=18 EndZ=0
    g5: LineSegment StartX=34 StartY=18 StartZ=0 EndX=34 EndY=-18 EndZ=0
    g6: LineSegment StartX=34 StartY=-18 StartZ=0 EndX=-34 EndY=-18 EndZ=0
    g7: LineSegment StartX=-34 StartY=-18 StartZ=0 EndX=-34 EndY=18 EndZ=0
    g8: LineSegment StartX=-33 StartY=17 StartZ=0 EndX=33 EndY=17 EndZ=0
    g9: LineSegment StartX=33 StartY=17 StartZ=0 EndX=33 EndY=-17 EndZ=0
    g10: LineSegment StartX=33 StartY=-17 StartZ=0 EndX=-33 EndY=-17 EndZ=0
    g11: LineSegment StartX=-33 StartY=-17 StartZ=0 EndX=-33 EndY=17 EndZ=0
  constraints (31):
    c: Horizontal(g0,g1)
    c: Horizontal(g2,g3)
    c: Vertical(g0,g3)
    c: Vertical(g2,g1)
    c: DistanceX(g0,g1) = 58
    c: DistanceY(g3,g0) = 26
    c: Symmetric(g0,g2,g-1)
    c: Coincident(g4,g5)
    c: Coincident(g5,g6)
    c: Coincident(g6,g7)
    c: Coincident(g7,g4)
    c: Horizontal(g4)
    c: Horizontal(g6)
    c: Vertical(g5)
    c: Vertical(g7)
    c: DistanceX(g4,g3) = 5
    c: DistanceX(g1,g4) = 5
    c: DistanceY(g1,g4) = 5
    c: DistanceY(g5,g2) = 5
    c: Coincident(g8,g9)
    c: Coincident(g9,g10)
    c: Coincident(g10,g11)
    c: Coincident(g11,g8)
    c: Horizontal(g8)
    c: Horizontal(g10)
    c: Vertical(g9)
    c: Vertical(g11)
    c: DistanceX(g8,g4) = 1
    c: DistanceX(g4,g8) = 1
    c: DistanceY(g8,g4) = 1
    c: DistanceY(g6,g10) = 1
FEATURE [PartDesign::Pad] Pad033
  BaseFeature = -> Pad032
  Direction = (0,0,1)
  Length = 13
  Length2 = 10
  Profile = -> Sketch050
  ReferenceAxis = -> Sketch050 [N_Axis]
  Type = 0
FEATURE [Sketcher::SketchObject] Sketch051
  FullyConstrained = true
  MapMode = 5
  Support = -> [XY_Plane014]
  expr: Constraints[26] = Spreadsheet001.B2
  expr: Constraints[27] = Spreadsheet001.C2
  sketch-geometry (13):
    g0: GeomPoint X=-29 Y=13 Z=0
    g1: GeomPoint X=29 Y=13 Z=0
    g2: GeomPoint X=29 Y=-13 Z=0
    g3: GeomPoint X=-29 Y=-13 Z=0
    g4: LineSegment StartX=-30 StartY=14 StartZ=0 EndX=30 EndY=14 EndZ=0
    g5: LineSegment StartX=30 StartY=14 StartZ=0 EndX=30 EndY=-14 EndZ=0
    g6: LineSegment StartX=30 StartY=-14 StartZ=0 EndX=-30 EndY=-14 EndZ=0
    g7: LineSegment StartX=-30 StartY=-14 StartZ=0 EndX=-30 EndY=14 EndZ=0
    g8: LineSegment StartX=-26.46 StartY=11.23 StartZ=0 EndX=-23.42 EndY=11.23 EndZ=0
    g9: LineSegment StartX=-23.42 StartY=11.23 StartZ=0 EndX=-23.42 EndY=-2.105 EndZ=0
    g10: LineSegment StartX=-23.42 StartY=-2.105 StartZ=0 EndX=-26.46 EndY=-2.105 EndZ=0
    g11: LineSegment StartX=-26.46 StartY=-2.105 StartZ=0 EndX=-26.46 EndY=11.23 EndZ=0
    g12: GeomPoint X=-24.94 Y=-2.105 Z=0
  constraints (31):
    c: Horizontal(g0,g1)
    c: Horizontal(g2,g3)
    c: Vertical(g0,g3)
    c: Vertical(g2,g1)
    c: DistanceX(g0,g1) = 58
    c: DistanceY(g3,g0) = 26
    c: Symmetric(g0,g2,g-1)
    c: Coincident(g4,g5)
    c: Coincident(g5,g6)
    c: Coincident(g6,g7)
    c: Coincident(g7,g4)
    c: Horizontal(g4)
    c: Horizontal(g6)
    c: Vertical(g5)
    c: Vertical(g7)
    c: Symmetric(g4,g5,g-1)
    c: DistanceX(g4,g0) = 1
    c: DistanceY(g1,g4) = 1
    c: Coincident(g8,g9)
    c: Coincident(g9,g10)
    c: Coincident(g10,g11)
    c: Coincident(g11,g8)
    c: Horizontal(g8)
    c: Horizontal(g10)
    c: Vertical(g9)
    c: Vertical(g11)
    c: DistanceY(g11,g11) = 13.335
    c: DistanceX(g8,g8) = 3.04
    c: Symmetric(g10,g9,g12)
    c: DistanceY(g8,g0) = 1.77
    c: DistanceX(g3,g10) = 2.54
FEATURE [PartDesign::Pad] Pad034
  Direction = (0,0,1)
  Length = 1
  Length2 = 10
  Profile = -> Sketch051
  ReferenceAxis = -> Sketch051 [N_Axis]
  Type = 0
FEATURE [Sketcher::SketchObject] Sketch052
  FullyConstrained = true
  MapMode = 5
  Placement = pos=(0,0,1) rot=(0,0,1;0rad)
  Support = -> [Pad034]
  sketch-geometry (8):
    g0: LineSegment StartX=-29 StartY=13 StartZ=0 EndX=29 EndY=13 EndZ=0
    g1: LineSegment StartX=29 StartY=13 StartZ=0 EndX=29 EndY=-13 EndZ=0
    g2: LineSegment StartX=29 StartY=-13 StartZ=0 EndX=-29 EndY=-13 EndZ=0
    g3: LineSegment StartX=-29 StartY=-13 StartZ=0 EndX=-29 EndY=13 EndZ=0
    g4: LineSegment StartX=-30 StartY=14 StartZ=0 EndX=30 EndY=14 EndZ=0
    g5: LineSegment StartX=30 StartY=14 StartZ=0 EndX=30 EndY=-14 EndZ=0
    g6: LineSegment StartX=30 StartY=-14 StartZ=0 EndX=-30 EndY=-14 EndZ=0
    g7: LineSegment StartX=-30 StartY=-14 StartZ=0 EndX=-30 EndY=14 EndZ=0
  constraints (22):
    c: Coincident(g0,g1)
    c: Coincident(g1,g2)
    c: Coincident(g2,g3)
    c: Coincident(g3,g0)
    c: Horizontal(g0)
    c: Horizontal(g2)
    c: Vertical(g1)
    c: Vertical(g3)
    c: Symmetric(g0,g1,g-1)
    c: DistanceX(g0,g0) = 58
    c: DistanceY(g3,g3) = 26
    c: Coincident(g4,g5)
    c: Coincident(g5,g6)
    c: Coincident(g6,g7)
    c: Coincident(g7,g4)
    c: Horizontal(g4)
    c: Horizontal(g6)
    c: Vertical(g5)
    c: Vertical(g7)
    c: DistanceX(g1,g5) = 1
    c: DistanceY(g0,g4) = 1
    c: Symmetric(g4,g5,g-1)
FEATURE [PartDesign::Pad] Pad035
  BaseFeature = -> Pad034
  Direction = (0,0,1)
  Length = 6
  Length2 = 10
  Profile = -> Sketch052
  ReferenceAxis = -> Sketch052 [N_Axis]
  Type = 0
FEATURE [PartDesign::Body] Body014  label="Geiger Cover Inner001"
  Group = -> [Sketch051,Pad034,Sketch052,Pad035]
  Origin = -> Origin014
  Placement = pos=(0,0,4) rot=(0,0,1;0rad)
  Tip = -> Pad035
FEATURE [Sketcher::SketchObject] Sketch053
  FullyConstrained = true
  MapMode = 5
  Placement = pos=(0,0,1) rot=(0,0,1;0rad)
  Support = -> [Pad033]
  sketch-geometry (12):
    g0: Circle CenterX=-31 CenterY=15 CenterZ=0 NormalX=0 NormalY=0 NormalZ=1 AngleXU=0 Radius=1.5
    g1: Circle CenterX=31 CenterY=15 CenterZ=0 NormalX=0 NormalY=0 NormalZ=1 AngleXU=0 Radius=1.5
    g2: Circle CenterX=31 CenterY=-15 CenterZ=0 NormalX=0 NormalY=0 NormalZ=1 AngleXU=0 Radius=1.5
    g3: Circle CenterX=-31 CenterY=-15 CenterZ=0 NormalX=0 NormalY=0 NormalZ=1 AngleXU=0 Radius=1.5
    g4: GeomPoint X=-29 Y=13 Z=0
    g5: GeomPoint X=29 Y=13 Z=0
    g6: GeomPoint X=29 Y=-13 Z=0
    g7: GeomPoint X=-29 Y=-13 Z=0
    g8: GeomPoint X=-33 Y=17 Z=0
    g9: GeomPoint X=33 Y=17 Z=0
    g10: GeomPoint X=33 Y=-17 Z=0
    g11: GeomPoint X=-33 Y=-17 Z=0
  constraints (24):
    c: Symmetric(g0,g2,g-1)
    c: Horizontal(g0,g1)
    c: Horizontal(g2,g3)
    c: Vertical(g0,g3)
    c: Vertical(g2,g1)
    c: Symmetric(g4,g6,g-1)
    c: Horizontal(g4,g5)
    c: Horizontal(g6,g7)
    c: Vertical(g4,g7)
    c: Vertical(g6,g5)
    c: DistanceX(g4,g5) = 58
    c: DistanceY(g7,g4) = 26
    c: Symmetric(g8,g10,g-1)
    c: Vertical(g8,g11)
    c: Vertical(g10,g9)
    c: Horizontal(g8,g9)
    c: Horizontal(g10,g11)
    c: DistanceX(g8,g4) = 4
    c: Diameter(g0) = 3
    c: Diameter(g1) = 3
    c: Diameter(g2) = 3
    c: Diameter(g3) = 3
    c: DistanceY(g11,g7) = 4
    c: Symmetric(g4,g8,g0)
FEATURE [PartDesign::Pocket] Pocket009
  BaseFeature = -> Pad033
  Direction = (0,0,-1)
  Length = 5
  Length2 = 5
  Profile = -> Sketch053
  ReferenceAxis = -> Sketch053 [N_Axis]
  Type = 1
FEATURE [PartDesign::Body] Body013  label="Geiger Cover Outer001"
  Group = -> [Sketch049,Pad032,Sketch050,Pad033,Sketch053,Pocket009]
  Origin = -> Origin013
  Tip = -> Pocket009
FEATURE [Spreadsheet::Sheet] Spreadsheet001  label="GeigerVariables001"
  cells = B1=Length; C1=Width; A2=Header Hole; B2=13.335; C2=3.04
FEATURE [TechDraw::DrawSVGTemplate] Template
  Height = 210
  Orientation = 1
  Width = 297
FEATURE [TechDraw::DrawViewAnnotation] Annotation
  Font = osifont
  LineSpace = 80
  LockPosition = false
  MaxWidth = -1
  Rotation = 0
  ScaleType = 0
  Text = Top Mold
  TextSize = 5
  TextStyle = 0
  X = 21.1982
  Y = 168.829
FEATURE [TechDraw::DrawViewAnnotation] Annotation001
  Font = osifont
  LineSpace = 80
  LockPosition = false
  MaxWidth = -1
  Rotation = 0
  ScaleType = 0
  Text = Bottom Mold
  TextSize = 5
  TextStyle = 0
  X = 62.6592
  Y = 183.25
FEATURE [TechDraw::DrawViewAnnotation] Annotation002
  Font = osifont
  LineSpace = 80
  LockPosition = false
  MaxWidth = -1
  Rotation = 0
  ScaleType = 0
  Text = Short Side Mold
  TextSize = 5
  TextStyle = 0
  X = 146.848
  Y = 118.622
FEATURE [Part::Box] Box  label="Cube"
  AttacherType = Attacher::AttachEngine3D
  Height = 5
  Length = 70
  Placement = pos=(65,20,0) rot=(0,0,1;0rad)
  Width = 38
FEATURE [Part::Cut] Cut  label="Top Mold"
  Base = -> Box
  Tool = -> Body005
FEATURE [App::DocumentObjectGroup] Group020  label="Top"
  Group = -> [Cut]
FEATURE [Part::Box] Box001  label="Cube001"
  AttacherType = Attacher::AttachEngine3D
  Height = 5
  Length = 70
  Placement = pos=(65,59,0) rot=(0,0,1;0rad)
  Width = 38
FEATURE [Part::Cut] Cut001  label="Bottom Mold"
  Base = -> Box001
  Tool = -> Body007
FEATURE [App::DocumentObjectGroup] Group021  label="Bottom"
  Group = -> [Cut001]
FEATURE [Part::Box] Box002  label="Cube002"
  AttacherType = Attacher::AttachEngine3D
  Height = 5
  Length = 11
  Placement = pos=(144.5,20,0) rot=(0,0,1;0rad)
  Width = 30
FEATURE [Part::Cut] Cut002  label="Short Side Mold"
  Base = -> Box002
  Placement = pos=(0,42,0) rot=(0,0,1;0rad)
  Tool = -> Body009
FEATURE [TechDraw::DrawViewAnnotation] Annotation003
  Font = osifont
  LineSpace = 80
  LockPosition = false
  MaxWidth = -1
  Rotation = 0
  ScaleType = 0
  Text = These molds will be used to cast | the silicone, and the resulted cast | will be used as a mold for the | epoxy. | Epoxy does not stick to | silicone, and we cannot use the | silicone directly as the sulphur in the  | barium sulfate shielding additive | (BaSO4) causes cure inhibition in | platinum-cured silicone. However, | barium sulfate does not affect epoxy | resin.
  TextSize = 5
  TextStyle = 0
  X = 235.197
  Y = 131.642
FEATURE [TechDraw::DrawViewAnnotation] Annotation004
  Font = osifont
  LineSpace = 80
  LockPosition = false
  MaxWidth = -1
  Rotation = 0
  ScaleType = 0
  Text = Once the epoxy has been cured, the resulting casts can be "sandwiched." One top | mold will go on the top cavity, in-between the inner and outer cover. You can then | place the two short side casts in the short cavities, in-between the screw holes.  | The two long side casts will be placed in the long cavities, in-between the screw  | holes. The bottom cast will be placed in the bottom cavity, in-between the geiger | counter/inner cover and the top face of the stack plate. You can then insert M3x20 | screws into the 4 screw holes, and add M3 nuts if required.
  TextSize = 5
  TextStyle = 0
  X = 184.714
  Y = 42.9053
FEATURE [Sketcher::SketchObject] Sketch054
  FullyConstrained = true
  MapMode = 5
  Support = -> [XY_Plane015]
  expr: Constraints[17] = <<GeigerVariables001>>.C2
  expr: Constraints[18] = <<GeigerVariables001>>.B2
  sketch-geometry (13):
    g0: LineSegment StartX=-34 StartY=18 StartZ=0 EndX=34 EndY=18 EndZ=0
    g1: LineSegment StartX=34 StartY=18 StartZ=0 EndX=34 EndY=-18 EndZ=0
    g2: LineSegment StartX=34 StartY=-18 StartZ=0 EndX=-34 EndY=-18 EndZ=0
    g3: LineSegment StartX=-34 StartY=-18 StartZ=0 EndX=-34 EndY=18 EndZ=0
    g4: LineSegment StartX=-26.46 StartY=11.23 StartZ=0 EndX=-23.42 EndY=11.23 EndZ=0
    g5: LineSegment StartX=-23.42 StartY=11.23 StartZ=0 EndX=-23.42 EndY=-2.105 EndZ=0
    g6: LineSegment StartX=-23.42 StartY=-2.105 StartZ=0 EndX=-26.46 EndY=-2.105 EndZ=0
    g7: LineSegment StartX=-26.46 StartY=-2.105 StartZ=0 EndX=-26.46 EndY=11.23 EndZ=0
    g8: GeomPoint X=-29 Y=13 Z=0
    g9: GeomPoint X=29 Y=13 Z=0
    g10: GeomPoint X=29 Y=-13 Z=0
    g11: GeomPoint X=-29 Y=-13 Z=0
    g12: GeomPoint X=-24.94 Y=-2.105 Z=0
  constraints (32):
    c: Coincident(g0,g1)
    c: Coincident(g1,g2)
    c: Coincident(g2,g3)
    c: Coincident(g3,g0)
    c: Horizontal(g0)
    c: Horizontal(g2)
    c: Vertical(g1)
    c: Vertical(g3)
    c: Symmetric(g0,g1,g-1)
    c: Coincident(g4,g5)
    c: Coincident(g5,g6)
    c: Coincident(g6,g7)
    c: Coincident(g7,g4)
    c: Horizontal(g4)
    c: Horizontal(g6)
    c: Vertical(g5)
    c: Vertical(g7)
    c: DistanceX(g4,g4) = 3.04
    c: DistanceY(g7,g7) = 13.335
    c: Horizontal(g8,g9)
    c: Horizontal(g10,g11)
    c: Vertical(g11,g8)
    c: Vertical(g10,g9)
    c: DistanceX(g8,g9) = 58
    c: DistanceY(g11,g8) = 26
    c: Symmetric(g5,g6,g12)
    c: DistanceX(g0,g8) = 5
    c: DistanceX(g0,g9) = -5
    c: DistanceY(g8,g0) = 5
    c: DistanceY(g1,g10) = 5
    c: DistanceY(g4,g8) = 1.77
    c: DistanceX(g11,g6) = 2.54
FEATURE [PartDesign::Pad] Pad036
  Direction = (0,0,1)
  Length = 1
  Length2 = 10
  Profile = -> Sketch054
  ReferenceAxis = -> Sketch054 [N_Axis]
  Type = 0
FEATURE [Sketcher::SketchObject] Sketch055
  FullyConstrained = true
  MapMode = 5
  Placement = pos=(0,0,1) rot=(0,0,1;0rad)
  Support = -> [Pad036]
  sketch-geometry (12):
    g0: GeomPoint X=-29 Y=13 Z=0
    g1: GeomPoint X=29 Y=13 Z=0
    g2: GeomPoint X=29 Y=-13 Z=0
    g3: GeomPoint X=-29 Y=-13 Z=0
    g4: LineSegment StartX=-34 StartY=18 StartZ=0 EndX=34 EndY=18 EndZ=0
    g5: LineSegment StartX=34 StartY=18 StartZ=0 EndX=34 EndY=-18 EndZ=0
    g6: LineSegment StartX=34 StartY=-18 StartZ=0 EndX=-34 EndY=-18 EndZ=0
    g7: LineSegment StartX=-34 StartY=-18 StartZ=0 EndX=-34 EndY=18 EndZ=0
    g8: LineSegment StartX=-33 StartY=17 StartZ=0 EndX=33 EndY=17 EndZ=0
    g9: LineSegment StartX=33 StartY=17 StartZ=0 EndX=33 EndY=-17 EndZ=0
    g10: LineSegment StartX=33 StartY=-17 StartZ=0 EndX=-33 EndY=-17 EndZ=0
    g11: LineSegment StartX=-33 StartY=-17 StartZ=0 EndX=-33 EndY=17 EndZ=0
  constraints (31):
    c: Horizontal(g0,g1)
    c: Horizontal(g2,g3)
    c: Vertical(g0,g3)
    c: Vertical(g2,g1)
    c: DistanceX(g0,g1) = 58
    c: DistanceY(g3,g0) = 26
    c: Symmetric(g0,g2,g-1)
    c: Coincident(g4,g5)
    c: Coincident(g5,g6)
    c: Coincident(g6,g7)
    c: Coincident(g7,g4)
    c: Horizontal(g4)
    c: Horizontal(g6)
    c: Vertical(g5)
    c: Vertical(g7)
    c: DistanceX(g4,g3) = 5
    c: DistanceX(g1,g4) = 5
    c: DistanceY(g1,g4) = 5
    c: DistanceY(g5,g2) = 5
    c: Coincident(g8,g9)
    c: Coincident(g9,g10)
    c: Coincident(g10,g11)
    c: Coincident(g11,g8)
    c: Horizontal(g8)
    c: Horizontal(g10)
    c: Vertical(g9)
    c: Vertical(g11)
    c: DistanceX(g8,g4) = 1
    c: DistanceX(g4,g8) = 1
    c: DistanceY(g8,g4) = 1
    c: DistanceY(g6,g10) = 1
FEATURE [PartDesign::Pad] Pad037
  BaseFeature = -> Pad036
  Direction = (0,0,1)
  Length = 13
  Length2 = 10
  Profile = -> Sketch055
  ReferenceAxis = -> Sketch055 [N_Axis]
  Type = 0
FEATURE [Sketcher::SketchObject] Sketch056
  FullyConstrained = true
  MapMode = 5
  Support = -> [XY_Plane016]
  expr: Constraints[26] = Spreadsheet001.B2
  expr: Constraints[27] = Spreadsheet001.C2
  sketch-geometry (13):
    g0: GeomPoint X=-29 Y=13 Z=0
    g1: GeomPoint X=29 Y=13 Z=0
    g2: GeomPoint X=29 Y=-13 Z=0
    g3: GeomPoint X=-29 Y=-13 Z=0
    g4: LineSegment StartX=-30 StartY=14 StartZ=0 EndX=30 EndY=14 EndZ=0
    g5: LineSegment StartX=30 StartY=14 StartZ=0 EndX=30 EndY=-14 EndZ=0
    g6: LineSegment StartX=30 StartY=-14 StartZ=0 EndX=-30 EndY=-14 EndZ=0
    g7: LineSegment StartX=-30 StartY=-14 StartZ=0 EndX=-30 EndY=14 EndZ=0
    g8: LineSegment StartX=-26.46 StartY=11.23 StartZ=0 EndX=-23.42 EndY=11.23 EndZ=0
    g9: LineSegment StartX=-23.42 StartY=11.23 StartZ=0 EndX=-23.42 EndY=-2.105 EndZ=0
    g10: LineSegment StartX=-23.42 StartY=-2.105 StartZ=0 EndX=-26.46 EndY=-2.105 EndZ=0
    g11: LineSegment StartX=-26.46 StartY=-2.105 StartZ=0 EndX=-26.46 EndY=11.23 EndZ=0
    g12: GeomPoint X=-24.94 Y=-2.105 Z=0
  constraints (31):
    c: Horizontal(g0,g1)
    c: Horizontal(g2,g3)
    c: Vertical(g0,g3)
    c: Vertical(g2,g1)
    c: DistanceX(g0,g1) = 58
    c: DistanceY(g3,g0) = 26
    c: Symmetric(g0,g2,g-1)
    c: Coincident(g4,g5)
    c: Coincident(g5,g6)
    c: Coincident(g6,g7)
    c: Coincident(g7,g4)
    c: Horizontal(g4)
    c: Horizontal(g6)
    c: Vertical(g5)
    c: Vertical(g7)
    c: Symmetric(g4,g5,g-1)
    c: DistanceX(g4,g0) = 1
    c: DistanceY(g1,g4) = 1
    c: Coincident(g8,g9)
    c: Coincident(g9,g10)
    c: Coincident(g10,g11)
    c: Coincident(g11,g8)
    c: Horizontal(g8)
    c: Horizontal(g10)
    c: Vertical(g9)
    c: Vertical(g11)
    c: DistanceY(g11,g11) = 13.335
    c: DistanceX(g8,g8) = 3.04
    c: Symmetric(g10,g9,g12)
    c: DistanceY(g8,g0) = 1.77
    c: DistanceX(g3,g10) = 2.54
FEATURE [PartDesign::Pad] Pad038
  Direction = (0,0,1)
  Length = 1
  Length2 = 10
  Profile = -> Sketch056
  ReferenceAxis = -> Sketch056 [N_Axis]
  Type = 0
FEATURE [Sketcher::SketchObject] Sketch057
  FullyConstrained = true
  MapMode = 5
  Placement = pos=(0,0,1) rot=(0,0,1;0rad)
  Support = -> [Pad038]
  sketch-geometry (8):
    g0: LineSegment StartX=-29 StartY=13 StartZ=0 EndX=29 EndY=13 EndZ=0
    g1: LineSegment StartX=29 StartY=13 StartZ=0 EndX=29 EndY=-13 EndZ=0
    g2: LineSegment StartX=29 StartY=-13 StartZ=0 EndX=-29 EndY=-13 EndZ=0
    g3: LineSegment StartX=-29 StartY=-13 StartZ=0 EndX=-29 EndY=13 EndZ=0
    g4: LineSegment StartX=-30 StartY=14 StartZ=0 EndX=30 EndY=14 EndZ=0
    g5: LineSegment StartX=30 StartY=14 StartZ=0 EndX=30 EndY=-14 EndZ=0
    g6: LineSegment StartX=30 StartY=-14 StartZ=0 EndX=-30 EndY=-14 EndZ=0
    g7: LineSegment StartX=-30 StartY=-14 StartZ=0 EndX=-30 EndY=14 EndZ=0
  constraints (22):
    c: Coincident(g0,g1)
    c: Coincident(g1,g2)
    c: Coincident(g2,g3)
    c: Coincident(g3,g0)
    c: Horizontal(g0)
    c: Horizontal(g2)
    c: Vertical(g1)
    c: Vertical(g3)
    c: Symmetric(g0,g1,g-1)
    c: DistanceX(g0,g0) = 58
    c: DistanceY(g3,g3) = 26
    c: Coincident(g4,g5)
    c: Coincident(g5,g6)
    c: Coincident(g6,g7)
    c: Coincident(g7,g4)
    c: Horizontal(g4)
    c: Horizontal(g6)
    c: Vertical(g5)
    c: Vertical(g7)
    c: DistanceX(g1,g5) = 1
    c: DistanceY(g0,g4) = 1
    c: Symmetric(g4,g5,g-1)
FEATURE [PartDesign::Pad] Pad039
  BaseFeature = -> Pad038
  Direction = (0,0,1)
  Length = 6
  Length2 = 10
  Profile = -> Sketch057
  ReferenceAxis = -> Sketch057 [N_Axis]
  Type = 0
FEATURE [PartDesign::Body] Body016  label="Geiger Cover Inner002"
  Group = -> [Sketch056,Pad038,Sketch057,Pad039]
  Origin = -> Origin016
  Placement = pos=(0,0,4) rot=(0,0,1;0rad)
  Tip = -> Pad039
FEATURE [Sketcher::SketchObject] Sketch058
  FullyConstrained = true
  MapMode = 5
  Placement = pos=(0,0,1) rot=(0,0,1;0rad)
  Support = -> [Pad037]
  sketch-geometry (12):
    g0: Circle CenterX=-31 CenterY=15 CenterZ=0 NormalX=0 NormalY=0 NormalZ=1 AngleXU=0 Radius=1.5
    g1: Circle CenterX=31 CenterY=15 CenterZ=0 NormalX=0 NormalY=0 NormalZ=1 AngleXU=0 Radius=1.5
    g2: Circle CenterX=31 CenterY=-15 CenterZ=0 NormalX=0 NormalY=0 NormalZ=1 AngleXU=0 Radius=1.5
    g3: Circle CenterX=-31 CenterY=-15 CenterZ=0 NormalX=0 NormalY=0 NormalZ=1 AngleXU=0 Radius=1.5
    g4: GeomPoint X=-29 Y=13 Z=0
    g5: GeomPoint X=29 Y=13 Z=0
    g6: GeomPoint X=29 Y=-13 Z=0
    g7: GeomPoint X=-29 Y=-13 Z=0
    g8: GeomPoint X=-33 Y=17 Z=0
    g9: GeomPoint X=33 Y=17 Z=0
    g10: GeomPoint X=33 Y=-17 Z=0
    g11: GeomPoint X=-33 Y=-17 Z=0
  constraints (24):
    c: Symmetric(g0,g2,g-1)
    c: Horizontal(g0,g1)
    c: Horizontal(g2,g3)
    c: Vertical(g0,g3)
    c: Vertical(g2,g1)
    c: Symmetric(g4,g6,g-1)
    c: Horizontal(g4,g5)
    c: Horizontal(g6,g7)
    c: Vertical(g4,g7)
    c: Vertical(g6,g5)
    c: DistanceX(g4,g5) = 58
    c: DistanceY(g7,g4) = 26
    c: Symmetric(g8,g10,g-1)
    c: Vertical(g8,g11)
    c: Vertical(g10,g9)
    c: Horizontal(g8,g9)
    c: Horizontal(g10,g11)
    c: DistanceX(g8,g4) = 4
    c: Diameter(g0) = 3
    c: Diameter(g1) = 3
    c: Diameter(g2) = 3
    c: Diameter(g3) = 3
    c: DistanceY(g11,g7) = 4
    c: Symmetric(g4,g8,g0)
FEATURE [PartDesign::Pocket] Pocket010
  BaseFeature = -> Pad037
  Direction = (0,0,-1)
  Length = 5
  Length2 = 5
  Profile = -> Sketch058
  ReferenceAxis = -> Sketch058 [N_Axis]
  Type = 1
FEATURE [PartDesign::Body] Body015  label="Geiger Cover Outer002"
  Group = -> [Sketch054,Pad036,Sketch055,Pad037,Sketch058,Pocket010]
  Origin = -> Origin015
  Tip = -> Pocket010
FEATURE [Part::Compound] Compound016  label="Control Geiger Cover"
  Links = -> [Body014,Body013,Body015,Body016]
  Placement = pos=(12,-0.1,58) rot=(0.707107,0.707107,0;3.14159rad)
FEATURE [Sketcher::SketchObject] Sketch059
  FullyConstrained = true
  MapMode = 5
  Support = -> [XY_Plane017]
  expr: Constraints[17] = <<GeigerVariables001>>.C2
  expr: Constraints[18] = <<GeigerVariables001>>.B2
  sketch-geometry (13):
    g0: LineSegment StartX=-34 StartY=18 StartZ=0 EndX=34 EndY=18 EndZ=0
    g1: LineSegment StartX=34 StartY=18 StartZ=0 EndX=34 EndY=-18 EndZ=0
    g2: LineSegment StartX=34 StartY=-18 StartZ=0 EndX=-34 EndY=-18 EndZ=0
    g3: LineSegment StartX=-34 StartY=-18 StartZ=0 EndX=-34 EndY=18 EndZ=0
    g4: LineSegment StartX=-26.46 StartY=11.23 StartZ=0 EndX=-23.42 EndY=11.23 EndZ=0
    g5: LineSegment StartX=-23.42 StartY=11.23 StartZ=0 EndX=-23.42 EndY=-2.105 EndZ=0
    g6: LineSegment StartX=-23.42 StartY=-2.105 StartZ=0 EndX=-26.46 EndY=-2.105 EndZ=0
    g7: LineSegment StartX=-26.46 StartY=-2.105 StartZ=0 EndX=-26.46 EndY=11.23 EndZ=0
    g8: GeomPoint X=-29 Y=13 Z=0
    g9: GeomPoint X=29 Y=13 Z=0
    g10: GeomPoint X=29 Y=-13 Z=0
    g11: GeomPoint X=-29 Y=-13 Z=0
    g12: GeomPoint X=-24.94 Y=-2.105 Z=0
  constraints (32):
    c: Coincident(g0,g1)
    c: Coincident(g1,g2)
    c: Coincident(g2,g3)
    c: Coincident(g3,g0)
    c: Horizontal(g0)
    c: Horizontal(g2)
    c: Vertical(g1)
    c: Vertical(g3)
    c: Symmetric(g0,g1,g-1)
    c: Coincident(g4,g5)
    c: Coincident(g5,g6)
    c: Coincident(g6,g7)
    c: Coincident(g7,g4)
    c: Horizontal(g4)
    c: Horizontal(g6)
    c: Vertical(g5)
    c: Vertical(g7)
    c: DistanceX(g4,g4) = 3.04
    c: DistanceY(g7,g7) = 13.335
    c: Horizontal(g8,g9)
    c: Horizontal(g10,g11)
    c: Vertical(g11,g8)
    c: Vertical(g10,g9)
    c: DistanceX(g8,g9) = 58
    c: DistanceY(g11,g8) = 26
    c: Symmetric(g5,g6,g12)
    c: DistanceX(g0,g8) = 5
    c: DistanceX(g0,g9) = -5
    c: DistanceY(g8,g0) = 5
    c: DistanceY(g1,g10) = 5
    c: DistanceY(g4,g8) = 1.77
    c: DistanceX(g11,g6) = 2.54
FEATURE [PartDesign::Pad] Pad040
  Direction = (0,0,1)
  Length = 1
  Length2 = 10
  Profile = -> Sketch059
  ReferenceAxis = -> Sketch059 [N_Axis]
  Type = 0
FEATURE [Sketcher::SketchObject] Sketch060
  FullyConstrained = true
  MapMode = 5
  Placement = pos=(0,0,1) rot=(0,0,1;0rad)
  Support = -> [Pad040]
  sketch-geometry (12):
    g0: GeomPoint X=-29 Y=13 Z=0
    g1: GeomPoint X=29 Y=13 Z=0
    g2: GeomPoint X=29 Y=-13 Z=0
    g3: GeomPoint X=-29 Y=-13 Z=0
    g4: LineSegment StartX=-34 StartY=18 StartZ=0 EndX=34 EndY=18 EndZ=0
    g5: LineSegment StartX=34 StartY=18 StartZ=0 EndX=34 EndY=-18 EndZ=0
    g6: LineSegment StartX=34 StartY=-18 StartZ=0 EndX=-34 EndY=-18 EndZ=0
    g7: LineSegment StartX=-34 StartY=-18 StartZ=0 EndX=-34 EndY=18 EndZ=0
    g8: LineSegment StartX=-33 StartY=17 StartZ=0 EndX=33 EndY=17 EndZ=0
    g9: LineSegment StartX=33 StartY=17 StartZ=0 EndX=33 EndY=-17 EndZ=0
    g10: LineSegment StartX=33 StartY=-17 StartZ=0 EndX=-33 EndY=-17 EndZ=0
    g11: LineSegment StartX=-33 StartY=-17 StartZ=0 EndX=-33 EndY=17 EndZ=0
  constraints (31):
    c: Horizontal(g0,g1)
    c: Horizontal(g2,g3)
    c: Vertical(g0,g3)
    c: Vertical(g2,g1)
    c: DistanceX(g0,g1) = 58
    c: DistanceY(g3,g0) = 26
    c: Symmetric(g0,g2,g-1)
    c: Coincident(g4,g5)
    c: Coincident(g5,g6)
    c: Coincident(g6,g7)
    c: Coincident(g7,g4)
    c: Horizontal(g4)
    c: Horizontal(g6)
    c: Vertical(g5)
    c: Vertical(g7)
    c: DistanceX(g4,g3) = 5
    c: DistanceX(g1,g4) = 5
    c: DistanceY(g1,g4) = 5
    c: DistanceY(g5,g2) = 5
    c: Coincident(g8,g9)
    c: Coincident(g9,g10)
    c: Coincident(g10,g11)
    c: Coincident(g11,g8)
    c: Horizontal(g8)
    c: Horizontal(g10)
    c: Vertical(g9)
    c: Vertical(g11)
    c: DistanceX(g8,g4) = 1
    c: DistanceX(g4,g8) = 1
    c: DistanceY(g8,g4) = 1
    c: DistanceY(g6,g10) = 1
FEATURE [PartDesign::Pad] Pad041
  BaseFeature = -> Pad040
  Direction = (0,0,1)
  Length = 13
  Length2 = 10
  Profile = -> Sketch060
  ReferenceAxis = -> Sketch060 [N_Axis]
  Type = 0
FEATURE [Sketcher::SketchObject] Sketch061
  FullyConstrained = true
  MapMode = 5
  Support = -> [XY_Plane018]
  expr: Constraints[26] = Spreadsheet001.B2
  expr: Constraints[27] = Spreadsheet001.C2
  sketch-geometry (13):
    g0: GeomPoint X=-29 Y=13 Z=0
    g1: GeomPoint X=29 Y=13 Z=0
    g2: GeomPoint X=29 Y=-13 Z=0
    g3: GeomPoint X=-29 Y=-13 Z=0
    g4: LineSegment StartX=-30 StartY=14 StartZ=0 EndX=30 EndY=14 EndZ=0
    g5: LineSegment StartX=30 StartY=14 StartZ=0 EndX=30 EndY=-14 EndZ=0
    g6: LineSegment StartX=30 StartY=-14 StartZ=0 EndX=-30 EndY=-14 EndZ=0
    g7: LineSegment StartX=-30 StartY=-14 StartZ=0 EndX=-30 EndY=14 EndZ=0
    g8: LineSegment StartX=-26.46 StartY=11.23 StartZ=0 EndX=-23.42 EndY=11.23 EndZ=0
    g9: LineSegment StartX=-23.42 StartY=11.23 StartZ=0 EndX=-23.42 EndY=-2.105 EndZ=0
    g10: LineSegment StartX=-23.42 StartY=-2.105 StartZ=0 EndX=-26.46 EndY=-2.105 EndZ=0
    g11: LineSegment StartX=-26.46 StartY=-2.105 StartZ=0 EndX=-26.46 EndY=11.23 EndZ=0
    g12: GeomPoint X=-24.94 Y=-2.105 Z=0
  constraints (31):
    c: Horizontal(g0,g1)
    c: Horizontal(g2,g3)
    c: Vertical(g0,g3)
    c: Vertical(g2,g1)
    c: DistanceX(g0,g1) = 58
    c: DistanceY(g3,g0) = 26
    c: Symmetric(g0,g2,g-1)
    c: Coincident(g4,g5)
    c: Coincident(g5,g6)
    c: Coincident(g6,g7)
    c: Coincident(g7,g4)
    c: Horizontal(g4)
    c: Horizontal(g6)
    c: Vertical(g5)
    c: Vertical(g7)
    c: Symmetric(g4,g5,g-1)
    c: DistanceX(g4,g0) = 1
    c: DistanceY(g1,g4) = 1
    c: Coincident(g8,g9)
    c: Coincident(g9,g10)
    c: Coincident(g10,g11)
    c: Coincident(g11,g8)
    c: Horizontal(g8)
    c: Horizontal(g10)
    c: Vertical(g9)
    c: Vertical(g11)
    c: DistanceY(g11,g11) = 13.335
    c: DistanceX(g8,g8) = 3.04
    c: Symmetric(g10,g9,g12)
    c: DistanceY(g8,g0) = 1.77
    c: DistanceX(g3,g10) = 2.54
FEATURE [PartDesign::Pad] Pad042
  Direction = (0,0,1)
  Length = 1
  Length2 = 10
  Profile = -> Sketch061
  ReferenceAxis = -> Sketch061 [N_Axis]
  Type = 0
FEATURE [Sketcher::SketchObject] Sketch062
  FullyConstrained = true
  MapMode = 5
  Placement = pos=(0,0,1) rot=(0,0,1;0rad)
  Support = -> [Pad042]
  sketch-geometry (8):
    g0: LineSegment StartX=-29 StartY=13 StartZ=0 EndX=29 EndY=13 EndZ=0
    g1: LineSegment StartX=29 StartY=13 StartZ=0 EndX=29 EndY=-13 EndZ=0
    g2: LineSegment StartX=29 StartY=-13 StartZ=0 EndX=-29 EndY=-13 EndZ=0
    g3: LineSegment StartX=-29 StartY=-13 StartZ=0 EndX=-29 EndY=13 EndZ=0
    g4: LineSegment StartX=-30 StartY=14 StartZ=0 EndX=30 EndY=14 EndZ=0
    g5: LineSegment StartX=30 StartY=14 StartZ=0 EndX=30 EndY=-14 EndZ=0
    g6: LineSegment StartX=30 StartY=-14 StartZ=0 EndX=-30 EndY=-14 EndZ=0
    g7: LineSegment StartX=-30 StartY=-14 StartZ=0 EndX=-30 EndY=14 EndZ=0
  constraints (22):
    c: Coincident(g0,g1)
    c: Coincident(g1,g2)
    c: Coincident(g2,g3)
    c: Coincident(g3,g0)
    c: Horizontal(g0)
    c: Horizontal(g2)
    c: Vertical(g1)
    c: Vertical(g3)
    c: Symmetric(g0,g1,g-1)
    c: DistanceX(g0,g0) = 58
    c: DistanceY(g3,g3) = 26
    c: Coincident(g4,g5)
    c: Coincident(g5,g6)
    c: Coincident(g6,g7)
    c: Coincident(g7,g4)
    c: Horizontal(g4)
    c: Horizontal(g6)
    c: Vertical(g5)
    c: Vertical(g7)
    c: DistanceX(g1,g5) = 1
    c: DistanceY(g0,g4) = 1
    c: Symmetric(g4,g5,g-1)
FEATURE [PartDesign::Pad] Pad043
  BaseFeature = -> Pad042
  Direction = (0,0,1)
  Length = 6
  Length2 = 10
  Profile = -> Sketch062
  ReferenceAxis = -> Sketch062 [N_Axis]
  Type = 0
FEATURE [PartDesign::Body] Body018  label="Geiger Cover Inner003"
  Group = -> [Sketch061,Pad042,Sketch062,Pad043]
  Origin = -> Origin018
  Placement = pos=(0,0,4) rot=(0,0,1;0rad)
  Tip = -> Pad043
FEATURE [Sketcher::SketchObject] Sketch063
  FullyConstrained = true
  MapMode = 5
  Placement = pos=(0,0,1) rot=(0,0,1;0rad)
  Support = -> [Pad041]
  sketch-geometry (12):
    g0: Circle CenterX=-31 CenterY=15 CenterZ=0 NormalX=0 NormalY=0 NormalZ=1 AngleXU=0 Radius=1.5
    g1: Circle CenterX=31 CenterY=15 CenterZ=0 NormalX=0 NormalY=0 NormalZ=1 AngleXU=0 Radius=1.5
    g2: Circle CenterX=31 CenterY=-15 CenterZ=0 NormalX=0 NormalY=0 NormalZ=1 AngleXU=0 Radius=1.5
    g3: Circle CenterX=-31 CenterY=-15 CenterZ=0 NormalX=0 NormalY=0 NormalZ=1 AngleXU=0 Radius=1.5
    g4: GeomPoint X=-29 Y=13 Z=0
    g5: GeomPoint X=29 Y=13 Z=0
    g6: GeomPoint X=29 Y=-13 Z=0
    g7: GeomPoint X=-29 Y=-13 Z=0
    g8: GeomPoint X=-33 Y=17 Z=0
    g9: GeomPoint X=33 Y=17 Z=0
    g10: GeomPoint X=33 Y=-17 Z=0
    g11: GeomPoint X=-33 Y=-17 Z=0
  constraints (24):
    c: Symmetric(g0,g2,g-1)
    c: Horizontal(g0,g1)
    c: Horizontal(g2,g3)
    c: Vertical(g0,g3)
    c: Vertical(g2,g1)
    c: Symmetric(g4,g6,g-1)
    c: Horizontal(g4,g5)
    c: Horizontal(g6,g7)
    c: Vertical(g4,g7)
    c: Vertical(g6,g5)
    c: DistanceX(g4,g5) = 58
    c: DistanceY(g7,g4) = 26
    c: Symmetric(g8,g10,g-1)
    c: Vertical(g8,g11)
    c: Vertical(g10,g9)
    c: Horizontal(g8,g9)
    c: Horizontal(g10,g11)
    c: DistanceX(g8,g4) = 4
    c: Diameter(g0) = 3
    c: Diameter(g1) = 3
    c: Diameter(g2) = 3
    c: Diameter(g3) = 3
    c: DistanceY(g11,g7) = 4
    c: Symmetric(g4,g8,g0)
FEATURE [PartDesign::Pocket] Pocket011
  BaseFeature = -> Pad041
  Direction = (0,0,-1)
  Length = 5
  Length2 = 5
  Profile = -> Sketch063
  ReferenceAxis = -> Sketch063 [N_Axis]
  Type = 1
FEATURE [PartDesign::Body] Body017  label="Geiger Cover Outer003"
  Group = -> [Sketch059,Pad040,Sketch060,Pad041,Sketch063,Pocket011]
  Origin = -> Origin017
  Tip = -> Pocket011
FEATURE [Sketcher::SketchObject] Sketch064
  FullyConstrained = true
  MapMode = 5
  Support = -> [XY_Plane019]
  expr: Constraints[17] = <<GeigerVariables001>>.C2
  expr: Constraints[18] = <<GeigerVariables001>>.B2
  sketch-geometry (13):
    g0: LineSegment StartX=-34 StartY=18 StartZ=0 EndX=34 EndY=18 EndZ=0
    g1: LineSegment StartX=34 StartY=18 StartZ=0 EndX=34 EndY=-18 EndZ=0
    g2: LineSegment StartX=34 StartY=-18 StartZ=0 EndX=-34 EndY=-18 EndZ=0
    g3: LineSegment StartX=-34 StartY=-18 StartZ=0 EndX=-34 EndY=18 EndZ=0
    g4: LineSegment StartX=-26.46 StartY=11.23 StartZ=0 EndX=-23.42 EndY=11.23 EndZ=0
    g5: LineSegment StartX=-23.42 StartY=11.23 StartZ=0 EndX=-23.42 EndY=-2.105 EndZ=0
    g6: LineSegment StartX=-23.42 StartY=-2.105 StartZ=0 EndX=-26.46 EndY=-2.105 EndZ=0
    g7: LineSegment StartX=-26.46 StartY=-2.105 StartZ=0 EndX=-26.46 EndY=11.23 EndZ=0
    g8: GeomPoint X=-29 Y=13 Z=0
    g9: GeomPoint X=29 Y=13 Z=0
    g10: GeomPoint X=29 Y=-13 Z=0
    g11: GeomPoint X=-29 Y=-13 Z=0
    g12: GeomPoint X=-24.94 Y=-2.105 Z=0
  constraints (32):
    c: Coincident(g0,g1)
    c: Coincident(g1,g2)
    c: Coincident(g2,g3)
    c: Coincident(g3,g0)
    c: Horizontal(g0)
    c: Horizontal(g2)
    c: Vertical(g1)
    c: Vertical(g3)
    c: Symmetric(g0,g1,g-1)
    c: Coincident(g4,g5)
    c: Coincident(g5,g6)
    c: Coincident(g6,g7)
    c: Coincident(g7,g4)
    c: Horizontal(g4)
    c: Horizontal(g6)
    c: Vertical(g5)
    c: Vertical(g7)
    c: DistanceX(g4,g4) = 3.04
    c: DistanceY(g7,g7) = 13.335
    c: Horizontal(g8,g9)
    c: Horizontal(g10,g11)
    c: Vertical(g11,g8)
    c: Vertical(g10,g9)
    c: DistanceX(g8,g9) = 58
    c: DistanceY(g11,g8) = 26
    c: Symmetric(g5,g6,g12)
    c: DistanceX(g0,g8) = 5
    c: DistanceX(g0,g9) = -5
    c: DistanceY(g8,g0) = 5
    c: DistanceY(g1,g10) = 5
    c: DistanceY(g4,g8) = 1.77
    c: DistanceX(g11,g6) = 2.54
FEATURE [PartDesign::Pad] Pad044
  Direction = (0,0,1)
  Length = 1
  Length2 = 10
  Profile = -> Sketch064
  ReferenceAxis = -> Sketch064 [N_Axis]
  Type = 0
FEATURE [Sketcher::SketchObject] Sketch065
  FullyConstrained = true
  MapMode = 5
  Placement = pos=(0,0,1) rot=(0,0,1;0rad)
  Support = -> [Pad044]
  sketch-geometry (12):
    g0: GeomPoint X=-29 Y=13 Z=0
    g1: GeomPoint X=29 Y=13 Z=0
    g2: GeomPoint X=29 Y=-13 Z=0
    g3: GeomPoint X=-29 Y=-13 Z=0
    g4: LineSegment StartX=-34 StartY=18 StartZ=0 EndX=34 EndY=18 EndZ=0
    g5: LineSegment StartX=34 StartY=18 StartZ=0 EndX=34 EndY=-18 EndZ=0
    g6: LineSegment StartX=34 StartY=-18 StartZ=0 EndX=-34 EndY=-18 EndZ=0
    g7: LineSegment StartX=-34 StartY=-18 StartZ=0 EndX=-34 EndY=18 EndZ=0
    g8: LineSegment StartX=-33 StartY=17 StartZ=0 EndX=33 EndY=17 EndZ=0
    g9: LineSegment StartX=33 StartY=17 StartZ=0 EndX=33 EndY=-17 EndZ=0
    g10: LineSegment StartX=33 StartY=-17 StartZ=0 EndX=-33 EndY=-17 EndZ=0
    g11: LineSegment StartX=-33 StartY=-17 StartZ=0 EndX=-33 EndY=17 EndZ=0
  constraints (31):
    c: Horizontal(g0,g1)
    c: Horizontal(g2,g3)
    c: Vertical(g0,g3)
    c: Vertical(g2,g1)
    c: DistanceX(g0,g1) = 58
    c: DistanceY(g3,g0) = 26
    c: Symmetric(g0,g2,g-1)
    c: Coincident(g4,g5)
    c: Coincident(g5,g6)
    c: Coincident(g6,g7)
    c: Coincident(g7,g4)
    c: Horizontal(g4)
    c: Horizontal(g6)
    c: Vertical(g5)
    c: Vertical(g7)
    c: DistanceX(g4,g3) = 5
    c: DistanceX(g1,g4) = 5
    c: DistanceY(g1,g4) = 5
    c: DistanceY(g5,g2) = 5
    c: Coincident(g8,g9)
    c: Coincident(g9,g10)
    c: Coincident(g10,g11)
    c: Coincident(g11,g8)
    c: Horizontal(g8)
    c: Horizontal(g10)
    c: Vertical(g9)
    c: Vertical(g11)
    c: DistanceX(g8,g4) = 1
    c: DistanceX(g4,g8) = 1
    c: DistanceY(g8,g4) = 1
    c: DistanceY(g6,g10) = 1
FEATURE [PartDesign::Pad] Pad045
  BaseFeature = -> Pad044
  Direction = (0,0,1)
  Length = 13
  Length2 = 10
  Profile = -> Sketch065
  ReferenceAxis = -> Sketch065 [N_Axis]
  Type = 0
FEATURE [Sketcher::SketchObject] Sketch066
  FullyConstrained = true
  MapMode = 5
  Support = -> [XY_Plane020]
  expr: Constraints[26] = Spreadsheet001.B2
  expr: Constraints[27] = Spreadsheet001.C2
  sketch-geometry (13):
    g0: GeomPoint X=-29 Y=13 Z=0
    g1: GeomPoint X=29 Y=13 Z=0
    g2: GeomPoint X=29 Y=-13 Z=0
    g3: GeomPoint X=-29 Y=-13 Z=0
    g4: LineSegment StartX=-30 StartY=14 StartZ=0 EndX=30 EndY=14 EndZ=0
    g5: LineSegment StartX=30 StartY=14 StartZ=0 EndX=30 EndY=-14 EndZ=0
    g6: LineSegment StartX=30 StartY=-14 StartZ=0 EndX=-30 EndY=-14 EndZ=0
    g7: LineSegment StartX=-30 StartY=-14 StartZ=0 EndX=-30 EndY=14 EndZ=0
    g8: LineSegment StartX=-26.46 StartY=11.23 StartZ=0 EndX=-23.42 EndY=11.23 EndZ=0
    g9: LineSegment StartX=-23.42 StartY=11.23 StartZ=0 EndX=-23.42 EndY=-2.105 EndZ=0
    g10: LineSegment StartX=-23.42 StartY=-2.105 StartZ=0 EndX=-26.46 EndY=-2.105 EndZ=0
    g11: LineSegment StartX=-26.46 StartY=-2.105 StartZ=0 EndX=-26.46 EndY=11.23 EndZ=0
    g12: GeomPoint X=-24.94 Y=-2.105 Z=0
  constraints (31):
    c: Horizontal(g0,g1)
    c: Horizontal(g2,g3)
    c: Vertical(g0,g3)
    c: Vertical(g2,g1)
    c: DistanceX(g0,g1) = 58
    c: DistanceY(g3,g0) = 26
    c: Symmetric(g0,g2,g-1)
    c: Coincident(g4,g5)
    c: Coincident(g5,g6)
    c: Coincident(g6,g7)
    c: Coincident(g7,g4)
    c: Horizontal(g4)
    c: Horizontal(g6)
    c: Vertical(g5)
    c: Vertical(g7)
    c: Symmetric(g4,g5,g-1)
    c: DistanceX(g4,g0) = 1
    c: DistanceY(g1,g4) = 1
    c: Coincident(g8,g9)
    c: Coincident(g9,g10)
    c: Coincident(g10,g11)
    c: Coincident(g11,g8)
    c: Horizontal(g8)
    c: Horizontal(g10)
    c: Vertical(g9)
    c: Vertical(g11)
    c: DistanceY(g11,g11) = 13.335
    c: DistanceX(g8,g8) = 3.04
    c: Symmetric(g10,g9,g12)
    c: DistanceY(g8,g0) = 1.77
    c: DistanceX(g3,g10) = 2.54
FEATURE [PartDesign::Pad] Pad046
  Direction = (0,0,1)
  Length = 1
  Length2 = 10
  Profile = -> Sketch066
  ReferenceAxis = -> Sketch066 [N_Axis]
  Type = 0
FEATURE [Sketcher::SketchObject] Sketch067
  FullyConstrained = true
  MapMode = 5
  Placement = pos=(0,0,1) rot=(0,0,1;0rad)
  Support = -> [Pad046]
  sketch-geometry (8):
    g0: LineSegment StartX=-29 StartY=13 StartZ=0 EndX=29 EndY=13 EndZ=0
    g1: LineSegment StartX=29 StartY=13 StartZ=0 EndX=29 EndY=-13 EndZ=0
    g2: LineSegment StartX=29 StartY=-13 StartZ=0 EndX=-29 EndY=-13 EndZ=0
    g3: LineSegment StartX=-29 StartY=-13 StartZ=0 EndX=-29 EndY=13 EndZ=0
    g4: LineSegment StartX=-30 StartY=14 StartZ=0 EndX=30 EndY=14 EndZ=0
    g5: LineSegment StartX=30 StartY=14 StartZ=0 EndX=30 EndY=-14 EndZ=0
    g6: LineSegment StartX=30 StartY=-14 StartZ=0 EndX=-30 EndY=-14 EndZ=0
    g7: LineSegment StartX=-30 StartY=-14 StartZ=0 EndX=-30 EndY=14 EndZ=0
  constraints (22):
    c: Coincident(g0,g1)
    c: Coincident(g1,g2)
    c: Coincident(g2,g3)
    c: Coincident(g3,g0)
    c: Horizontal(g0)
    c: Horizontal(g2)
    c: Vertical(g1)
    c: Vertical(g3)
    c: Symmetric(g0,g1,g-1)
    c: DistanceX(g0,g0) = 58
    c: DistanceY(g3,g3) = 26
    c: Coincident(g4,g5)
    c: Coincident(g5,g6)
    c: Coincident(g6,g7)
    c: Coincident(g7,g4)
    c: Horizontal(g4)
    c: Horizontal(g6)
    c: Vertical(g5)
    c: Vertical(g7)
    c: DistanceX(g1,g5) = 1
    c: DistanceY(g0,g4) = 1
    c: Symmetric(g4,g5,g-1)
FEATURE [PartDesign::Pad] Pad047
  BaseFeature = -> Pad046
  Direction = (0,0,1)
  Length = 6
  Length2 = 10
  Profile = -> Sketch067
  ReferenceAxis = -> Sketch067 [N_Axis]
  Type = 0
FEATURE [PartDesign::Body] Body020  label="Geiger Cover Inner004"
  Group = -> [Sketch066,Pad046,Sketch067,Pad047]
  Origin = -> Origin020
  Placement = pos=(0,0,4) rot=(0,0,1;0rad)
  Tip = -> Pad047
FEATURE [Sketcher::SketchObject] Sketch068
  FullyConstrained = true
  MapMode = 5
  Placement = pos=(0,0,1) rot=(0,0,1;0rad)
  Support = -> [Pad045]
  sketch-geometry (12):
    g0: Circle CenterX=-31 CenterY=15 CenterZ=0 NormalX=0 NormalY=0 NormalZ=1 AngleXU=0 Radius=1.5
    g1: Circle CenterX=31 CenterY=15 CenterZ=0 NormalX=0 NormalY=0 NormalZ=1 AngleXU=0 Radius=1.5
    g2: Circle CenterX=31 CenterY=-15 CenterZ=0 NormalX=0 NormalY=0 NormalZ=1 AngleXU=0 Radius=1.5
    g3: Circle CenterX=-31 CenterY=-15 CenterZ=0 NormalX=0 NormalY=0 NormalZ=1 AngleXU=0 Radius=1.5
    g4: GeomPoint X=-29 Y=13 Z=0
    g5: GeomPoint X=29 Y=13 Z=0
    g6: GeomPoint X=29 Y=-13 Z=0
    g7: GeomPoint X=-29 Y=-13 Z=0
    g8: GeomPoint X=-33 Y=17 Z=0
    g9: GeomPoint X=33 Y=17 Z=0
    g10: GeomPoint X=33 Y=-17 Z=0
    g11: GeomPoint X=-33 Y=-17 Z=0
  constraints (24):
    c: Symmetric(g0,g2,g-1)
    c: Horizontal(g0,g1)
    c: Horizontal(g2,g3)
    c: Vertical(g0,g3)
    c: Vertical(g2,g1)
    c: Symmetric(g4,g6,g-1)
    c: Horizontal(g4,g5)
    c: Horizontal(g6,g7)
    c: Vertical(g4,g7)
    c: Vertical(g6,g5)
    c: DistanceX(g4,g5) = 58
    c: DistanceY(g7,g4) = 26
    c: Symmetric(g8,g10,g-1)
    c: Vertical(g8,g11)
    c: Vertical(g10,g9)
    c: Horizontal(g8,g9)
    c: Horizontal(g10,g11)
    c: DistanceX(g8,g4) = 4
    c: Diameter(g0) = 3
    c: Diameter(g1) = 3
    c: Diameter(g2) = 3
    c: Diameter(g3) = 3
    c: DistanceY(g11,g7) = 4
    c: Symmetric(g4,g8,g0)
FEATURE [PartDesign::Pocket] Pocket012
  BaseFeature = -> Pad045
  Direction = (0,0,-1)
  Length = 5
  Length2 = 5
  Profile = -> Sketch068
  ReferenceAxis = -> Sketch068 [N_Axis]
  Type = 1
FEATURE [PartDesign::Body] Body019  label="Geiger Cover Outer004"
  Group = -> [Sketch064,Pad044,Sketch065,Pad045,Sketch068,Pocket012]
  Origin = -> Origin019
  Tip = -> Pocket012
FEATURE [Sketcher::SketchObject] Sketch069
  FullyConstrained = true
  MapMode = 5
  Support = -> [XY_Plane021]
  expr: Constraints[17] = <<GeigerVariables001>>.C2
  expr: Constraints[18] = <<GeigerVariables001>>.B2
  sketch-geometry (13):
    g0: LineSegment StartX=-34 StartY=18 StartZ=0 EndX=34 EndY=18 EndZ=0
    g1: LineSegment StartX=34 StartY=18 StartZ=0 EndX=34 EndY=-18 EndZ=0
    g2: LineSegment StartX=34 StartY=-18 StartZ=0 EndX=-34 EndY=-18 EndZ=0
    g3: LineSegment StartX=-34 StartY=-18 StartZ=0 EndX=-34 EndY=18 EndZ=0
    g4: LineSegment StartX=-26.46 StartY=11.23 StartZ=0 EndX=-23.42 EndY=11.23 EndZ=0
    g5: LineSegment StartX=-23.42 StartY=11.23 StartZ=0 EndX=-23.42 EndY=-2.105 EndZ=0
    g6: LineSegment StartX=-23.42 StartY=-2.105 StartZ=0 EndX=-26.46 EndY=-2.105 EndZ=0
    g7: LineSegment StartX=-26.46 StartY=-2.105 StartZ=0 EndX=-26.46 EndY=11.23 EndZ=0
    g8: GeomPoint X=-29 Y=13 Z=0
    g9: GeomPoint X=29 Y=13 Z=0
    g10: GeomPoint X=29 Y=-13 Z=0
    g11: GeomPoint X=-29 Y=-13 Z=0
    g12: GeomPoint X=-24.94 Y=-2.105 Z=0
  constraints (32):
    c: Coincident(g0,g1)
    c: Coincident(g1,g2)
    c: Coincident(g2,g3)
    c: Coincident(g3,g0)
    c: Horizontal(g0)
    c: Horizontal(g2)
    c: Vertical(g1)
    c: Vertical(g3)
    c: Symmetric(g0,g1,g-1)
    c: Coincident(g4,g5)
    c: Coincident(g5,g6)
    c: Coincident(g6,g7)
    c: Coincident(g7,g4)
    c: Horizontal(g4)
    c: Horizontal(g6)
    c: Vertical(g5)
    c: Vertical(g7)
    c: DistanceX(g4,g4) = 3.04
    c: DistanceY(g7,g7) = 13.335
    c: Horizontal(g8,g9)
    c: Horizontal(g10,g11)
    c: Vertical(g11,g8)
    c: Vertical(g10,g9)
    c: DistanceX(g8,g9) = 58
    c: DistanceY(g11,g8) = 26
    c: Symmetric(g5,g6,g12)
    c: DistanceX(g0,g8) = 5
    c: DistanceX(g0,g9) = -5
    c: DistanceY(g8,g0) = 5
    c: DistanceY(g1,g10) = 5
    c: DistanceY(g4,g8) = 1.77
    c: DistanceX(g11,g6) = 2.54
FEATURE [PartDesign::Pad] Pad048
  Direction = (0,0,1)
  Length = 1
  Length2 = 10
  Profile = -> Sketch069
  ReferenceAxis = -> Sketch069 [N_Axis]
  Type = 0
FEATURE [Sketcher::SketchObject] Sketch070
  FullyConstrained = true
  MapMode = 5
  Placement = pos=(0,0,1) rot=(0,0,1;0rad)
  Support = -> [Pad048]
  sketch-geometry (12):
    g0: GeomPoint X=-29 Y=13 Z=0
    g1: GeomPoint X=29 Y=13 Z=0
    g2: GeomPoint X=29 Y=-13 Z=0
    g3: GeomPoint X=-29 Y=-13 Z=0
    g4: LineSegment StartX=-34 StartY=18 StartZ=0 EndX=34 EndY=18 EndZ=0
    g5: LineSegment StartX=34 StartY=18 StartZ=0 EndX=34 EndY=-18 EndZ=0
    g6: LineSegment StartX=34 StartY=-18 StartZ=0 EndX=-34 EndY=-18 EndZ=0
    g7: LineSegment StartX=-34 StartY=-18 StartZ=0 EndX=-34 EndY=18 EndZ=0
    g8: LineSegment StartX=-33 StartY=17 StartZ=0 EndX=33 EndY=17 EndZ=0
    g9: LineSegment StartX=33 StartY=17 StartZ=0 EndX=33 EndY=-17 EndZ=0
    g10: LineSegment StartX=33 StartY=-17 StartZ=0 EndX=-33 EndY=-17 EndZ=0
    g11: LineSegment StartX=-33 StartY=-17 StartZ=0 EndX=-33 EndY=17 EndZ=0
  constraints (31):
    c: Horizontal(g0,g1)
    c: Horizontal(g2,g3)
    c: Vertical(g0,g3)
    c: Vertical(g2,g1)
    c: DistanceX(g0,g1) = 58
    c: DistanceY(g3,g0) = 26
    c: Symmetric(g0,g2,g-1)
    c: Coincident(g4,g5)
    c: Coincident(g5,g6)
    c: Coincident(g6,g7)
    c: Coincident(g7,g4)
    c: Horizontal(g4)
    c: Horizontal(g6)
    c: Vertical(g5)
    c: Vertical(g7)
    c: DistanceX(g4,g3) = 5
    c: DistanceX(g1,g4) = 5
    c: DistanceY(g1,g4) = 5
    c: DistanceY(g5,g2) = 5
    c: Coincident(g8,g9)
    c: Coincident(g9,g10)
    c: Coincident(g10,g11)
    c: Coincident(g11,g8)
    c: Horizontal(g8)
    c: Horizontal(g10)
    c: Vertical(g9)
    c: Vertical(g11)
    c: DistanceX(g8,g4) = 1
    c: DistanceX(g4,g8) = 1
    c: DistanceY(g8,g4) = 1
    c: DistanceY(g6,g10) = 1
FEATURE [PartDesign::Pad] Pad049
  BaseFeature = -> Pad048
  Direction = (0,0,1)
  Length = 13
  Length2 = 10
  Profile = -> Sketch070
  ReferenceAxis = -> Sketch070 [N_Axis]
  Type = 0
FEATURE [Sketcher::SketchObject] Sketch071
  FullyConstrained = true
  MapMode = 5
  Support = -> [XY_Plane022]
  expr: Constraints[26] = Spreadsheet001.B2
  expr: Constraints[27] = Spreadsheet001.C2
  sketch-geometry (13):
    g0: GeomPoint X=-29 Y=13 Z=0
    g1: GeomPoint X=29 Y=13 Z=0
    g2: GeomPoint X=29 Y=-13 Z=0
    g3: GeomPoint X=-29 Y=-13 Z=0
    g4: LineSegment StartX=-30 StartY=14 StartZ=0 EndX=30 EndY=14 EndZ=0
    g5: LineSegment StartX=30 StartY=14 StartZ=0 EndX=30 EndY=-14 EndZ=0
    g6: LineSegment StartX=30 StartY=-14 StartZ=0 EndX=-30 EndY=-14 EndZ=0
    g7: LineSegment StartX=-30 StartY=-14 StartZ=0 EndX=-30 EndY=14 EndZ=0
    g8: LineSegment StartX=-26.46 StartY=11.23 StartZ=0 EndX=-23.42 EndY=11.23 EndZ=0
    g9: LineSegment StartX=-23.42 StartY=11.23 StartZ=0 EndX=-23.42 EndY=-2.105 EndZ=0
    g10: LineSegment StartX=-23.42 StartY=-2.105 StartZ=0 EndX=-26.46 EndY=-2.105 EndZ=0
    g11: LineSegment StartX=-26.46 StartY=-2.105 StartZ=0 EndX=-26.46 EndY=11.23 EndZ=0
    g12: GeomPoint X=-24.94 Y=-2.105 Z=0
  constraints (31):
    c: Horizontal(g0,g1)
    c: Horizontal(g2,g3)
    c: Vertical(g0,g3)
    c: Vertical(g2,g1)
    c: DistanceX(g0,g1) = 58
    c: DistanceY(g3,g0) = 26
    c: Symmetric(g0,g2,g-1)
    c: Coincident(g4,g5)
    c: Coincident(g5,g6)
    c: Coincident(g6,g7)
    c: Coincident(g7,g4)
    c: Horizontal(g4)
    c: Horizontal(g6)
    c: Vertical(g5)
    c: Vertical(g7)
    c: Symmetric(g4,g5,g-1)
    c: DistanceX(g4,g0) = 1
    c: DistanceY(g1,g4) = 1
    c: Coincident(g8,g9)
    c: Coincident(g9,g10)
    c: Coincident(g10,g11)
    c: Coincident(g11,g8)
    c: Horizontal(g8)
    c: Horizontal(g10)
    c: Vertical(g9)
    c: Vertical(g11)
    c: DistanceY(g11,g11) = 13.335
    c: DistanceX(g8,g8) = 3.04
    c: Symmetric(g10,g9,g12)
    c: DistanceY(g8,g0) = 1.77
    c: DistanceX(g3,g10) = 2.54
FEATURE [PartDesign::Pad] Pad050
  Direction = (0,0,1)
  Length = 1
  Length2 = 10
  Profile = -> Sketch071
  ReferenceAxis = -> Sketch071 [N_Axis]
  Type = 0
FEATURE [Sketcher::SketchObject] Sketch072
  FullyConstrained = true
  MapMode = 5
  Placement = pos=(0,0,1) rot=(0,0,1;0rad)
  Support = -> [Pad050]
  sketch-geometry (8):
    g0: LineSegment StartX=-29 StartY=13 StartZ=0 EndX=29 EndY=13 EndZ=0
    g1: LineSegment StartX=29 StartY=13 StartZ=0 EndX=29 EndY=-13 EndZ=0
    g2: LineSegment StartX=29 StartY=-13 StartZ=0 EndX=-29 EndY=-13 EndZ=0
    g3: LineSegment StartX=-29 StartY=-13 StartZ=0 EndX=-29 EndY=13 EndZ=0
    g4: LineSegment StartX=-30 StartY=14 StartZ=0 EndX=30 EndY=14 EndZ=0
    g5: LineSegment StartX=30 StartY=14 StartZ=0 EndX=30 EndY=-14 EndZ=0
    g6: LineSegment StartX=30 StartY=-14 StartZ=0 EndX=-30 EndY=-14 EndZ=0
    g7: LineSegment StartX=-30 StartY=-14 StartZ=0 EndX=-30 EndY=14 EndZ=0
  constraints (22):
    c: Coincident(g0,g1)
    c: Coincident(g1,g2)
    c: Coincident(g2,g3)
    c: Coincident(g3,g0)
    c: Horizontal(g0)
    c: Horizontal(g2)
    c: Vertical(g1)
    c: Vertical(g3)
    c: Symmetric(g0,g1,g-1)
    c: DistanceX(g0,g0) = 58
    c: DistanceY(g3,g3) = 26
    c: Coincident(g4,g5)
    c: Coincident(g5,g6)
    c: Coincident(g6,g7)
    c: Coincident(g7,g4)
    c: Horizontal(g4)
    c: Horizontal(g6)
    c: Vertical(g5)
    c: Vertical(g7)
    c: DistanceX(g1,g5) = 1
    c: DistanceY(g0,g4) = 1
    c: Symmetric(g4,g5,g-1)
FEATURE [PartDesign::Pad] Pad051
  BaseFeature = -> Pad050
  Direction = (0,0,1)
  Length = 6
  Length2 = 10
  Profile = -> Sketch072
  ReferenceAxis = -> Sketch072 [N_Axis]
  Type = 0
FEATURE [PartDesign::Body] Body022  label="Geiger Cover Inner005"
  Group = -> [Sketch071,Pad050,Sketch072,Pad051]
  Origin = -> Origin022
  Placement = pos=(0,0,4) rot=(0,0,1;0rad)
  Tip = -> Pad051
FEATURE [Sketcher::SketchObject] Sketch073
  FullyConstrained = true
  MapMode = 5
  Placement = pos=(0,0,1) rot=(0,0,1;0rad)
  Support = -> [Pad049]
  sketch-geometry (12):
    g0: Circle CenterX=-31 CenterY=15 CenterZ=0 NormalX=0 NormalY=0 NormalZ=1 AngleXU=0 Radius=1.5
    g1: Circle CenterX=31 CenterY=15 CenterZ=0 NormalX=0 NormalY=0 NormalZ=1 AngleXU=0 Radius=1.5
    g2: Circle CenterX=31 CenterY=-15 CenterZ=0 NormalX=0 NormalY=0 NormalZ=1 AngleXU=0 Radius=1.5
    g3: Circle CenterX=-31 CenterY=-15 CenterZ=0 NormalX=0 NormalY=0 NormalZ=1 AngleXU=0 Radius=1.5
    g4: GeomPoint X=-29 Y=13 Z=0
    g5: GeomPoint X=29 Y=13 Z=0
    g6: GeomPoint X=29 Y=-13 Z=0
    g7: GeomPoint X=-29 Y=-13 Z=0
    g8: GeomPoint X=-33 Y=17 Z=0
    g9: GeomPoint X=33 Y=17 Z=0
    g10: GeomPoint X=33 Y=-17 Z=0
    g11: GeomPoint X=-33 Y=-17 Z=0
  constraints (24):
    c: Symmetric(g0,g2,g-1)
    c: Horizontal(g0,g1)
    c: Horizontal(g2,g3)
    c: Vertical(g0,g3)
    c: Vertical(g2,g1)
    c: Symmetric(g4,g6,g-1)
    c: Horizontal(g4,g5)
    c: Horizontal(g6,g7)
    c: Vertical(g4,g7)
    c: Vertical(g6,g5)
    c: DistanceX(g4,g5) = 58
    c: DistanceY(g7,g4) = 26
    c: Symmetric(g8,g10,g-1)
    c: Vertical(g8,g11)
    c: Vertical(g10,g9)
    c: Horizontal(g8,g9)
    c: Horizontal(g10,g11)
    c: DistanceX(g8,g4) = 4
    c: Diameter(g0) = 3
    c: Diameter(g1) = 3
    c: Diameter(g2) = 3
    c: Diameter(g3) = 3
    c: DistanceY(g11,g7) = 4
    c: Symmetric(g4,g8,g0)
FEATURE [PartDesign::Pocket] Pocket013
  BaseFeature = -> Pad049
  Direction = (0,0,-1)
  Length = 5
  Length2 = 5
  Profile = -> Sketch073
  ReferenceAxis = -> Sketch073 [N_Axis]
  Type = 1
FEATURE [PartDesign::Body] Body021  label="Geiger Cover Outer005"
  Group = -> [Sketch069,Pad048,Sketch070,Pad049,Sketch073,Pocket013]
  Origin = -> Origin021
  Tip = -> Pocket013
FEATURE [Part::Compound] Compound017  label="BaSO4 Geiger Cover"
  Links = -> [Body022,Body021,Body017,Body018]
  Placement = pos=(4,-0.1,79.5) rot=(0.57735,0.57735,-0.57735;4.18879rad)
FEATURE [Sketcher::SketchObject] Sketch074
  FullyConstrained = true
  MapMode = 5
  Support = -> [XY_Plane023]
  expr: Constraints[17] = <<GeigerVariables001>>.C2
  expr: Constraints[18] = <<GeigerVariables001>>.B2
  sketch-geometry (13):
    g0: LineSegment StartX=-34 StartY=18 StartZ=0 EndX=34 EndY=18 EndZ=0
    g1: LineSegment StartX=34 StartY=18 StartZ=0 EndX=34 EndY=-18 EndZ=0
    g2: LineSegment StartX=34 StartY=-18 StartZ=0 EndX=-34 EndY=-18 EndZ=0
    g3: LineSegment StartX=-34 StartY=-18 StartZ=0 EndX=-34 EndY=18 EndZ=0
    g4: LineSegment StartX=-26.46 StartY=11.23 StartZ=0 EndX=-23.42 EndY=11.23 EndZ=0
    g5: LineSegment StartX=-23.42 StartY=11.23 StartZ=0 EndX=-23.42 EndY=-2.105 EndZ=0
    g6: LineSegment StartX=-23.42 StartY=-2.105 StartZ=0 EndX=-26.46 EndY=-2.105 EndZ=0
    g7: LineSegment StartX=-26.46 StartY=-2.105 StartZ=0 EndX=-26.46 EndY=11.23 EndZ=0
    g8: GeomPoint X=-29 Y=13 Z=0
    g9: GeomPoint X=29 Y=13 Z=0
    g10: GeomPoint X=29 Y=-13 Z=0
    g11: GeomPoint X=-29 Y=-13 Z=0
    g12: GeomPoint X=-24.94 Y=-2.105 Z=0
  constraints (32):
    c: Coincident(g0,g1)
    c: Coincident(g1,g2)
    c: Coincident(g2,g3)
    c: Coincident(g3,g0)
    c: Horizontal(g0)
    c: Horizontal(g2)
    c: Vertical(g1)
    c: Vertical(g3)
    c: Symmetric(g0,g1,g-1)
    c: Coincident(g4,g5)
    c: Coincident(g5,g6)
    c: Coincident(g6,g7)
    c: Coincident(g7,g4)
    c: Horizontal(g4)
    c: Horizontal(g6)
    c: Vertical(g5)
    c: Vertical(g7)
    c: DistanceX(g4,g4) = 3.04
    c: DistanceY(g7,g7) = 13.335
    c: Horizontal(g8,g9)
    c: Horizontal(g10,g11)
    c: Vertical(g11,g8)
    c: Vertical(g10,g9)
    c: DistanceX(g8,g9) = 58
    c: DistanceY(g11,g8) = 26
    c: Symmetric(g5,g6,g12)
    c: DistanceX(g0,g8) = 5
    c: DistanceX(g0,g9) = -5
    c: DistanceY(g8,g0) = 5
    c: DistanceY(g1,g10) = 5
    c: DistanceY(g4,g8) = 1.77
    c: DistanceX(g11,g6) = 2.54
FEATURE [PartDesign::Pad] Pad052
  Direction = (0,0,1)
  Length = 1
  Length2 = 10
  Profile = -> Sketch074
  ReferenceAxis = -> Sketch074 [N_Axis]
  Type = 0
FEATURE [Sketcher::SketchObject] Sketch075
  FullyConstrained = true
  MapMode = 5
  Placement = pos=(0,0,1) rot=(0,0,1;0rad)
  Support = -> [Pad052]
  sketch-geometry (12):
    g0: GeomPoint X=-29 Y=13 Z=0
    g1: GeomPoint X=29 Y=13 Z=0
    g2: GeomPoint X=29 Y=-13 Z=0
    g3: GeomPoint X=-29 Y=-13 Z=0
    g4: LineSegment StartX=-34 StartY=18 StartZ=0 EndX=34 EndY=18 EndZ=0
    g5: LineSegment StartX=34 StartY=18 StartZ=0 EndX=34 EndY=-18 EndZ=0
    g6: LineSegment StartX=34 StartY=-18 StartZ=0 EndX=-34 EndY=-18 EndZ=0
    g7: LineSegment StartX=-34 StartY=-18 StartZ=0 EndX=-34 EndY=18 EndZ=0
    g8: LineSegment StartX=-33 StartY=17 StartZ=0 EndX=33 EndY=17 EndZ=0
    g9: LineSegment StartX=33 StartY=17 StartZ=0 EndX=33 EndY=-17 EndZ=0
    g10: LineSegment StartX=33 StartY=-17 StartZ=0 EndX=-33 EndY=-17 EndZ=0
    g11: LineSegment StartX=-33 StartY=-17 StartZ=0 EndX=-33 EndY=17 EndZ=0
  constraints (31):
    c: Horizontal(g0,g1)
    c: Horizontal(g2,g3)
    c: Vertical(g0,g3)
    c: Vertical(g2,g1)
    c: DistanceX(g0,g1) = 58
    c: DistanceY(g3,g0) = 26
    c: Symmetric(g0,g2,g-1)
    c: Coincident(g4,g5)
    c: Coincident(g5,g6)
    c: Coincident(g6,g7)
    c: Coincident(g7,g4)
    c: Horizontal(g4)
    c: Horizontal(g6)
    c: Vertical(g5)
    c: Vertical(g7)
    c: DistanceX(g4,g3) = 5
    c: DistanceX(g1,g4) = 5
    c: DistanceY(g1,g4) = 5
    c: DistanceY(g5,g2) = 5
    c: Coincident(g8,g9)
    c: Coincident(g9,g10)
    c: Coincident(g10,g11)
    c: Coincident(g11,g8)
    c: Horizontal(g8)
    c: Horizontal(g10)
    c: Vertical(g9)
    c: Vertical(g11)
    c: DistanceX(g8,g4) = 1
    c: DistanceX(g4,g8) = 1
    c: DistanceY(g8,g4) = 1
    c: DistanceY(g6,g10) = 1
FEATURE [PartDesign::Pad] Pad053
  BaseFeature = -> Pad052
  Direction = (0,0,1)
  Length = 13
  Length2 = 10
  Profile = -> Sketch075
  ReferenceAxis = -> Sketch075 [N_Axis]
  Type = 0
FEATURE [Sketcher::SketchObject] Sketch076
  FullyConstrained = true
  MapMode = 5
  Support = -> [XY_Plane024]
  expr: Constraints[26] = Spreadsheet001.B2
  expr: Constraints[27] = Spreadsheet001.C2
  sketch-geometry (13):
    g0: GeomPoint X=-29 Y=13 Z=0
    g1: GeomPoint X=29 Y=13 Z=0
    g2: GeomPoint X=29 Y=-13 Z=0
    g3: GeomPoint X=-29 Y=-13 Z=0
    g4: LineSegment StartX=-30 StartY=14 StartZ=0 EndX=30 EndY=14 EndZ=0
    g5: LineSegment StartX=30 StartY=14 StartZ=0 EndX=30 EndY=-14 EndZ=0
    g6: LineSegment StartX=30 StartY=-14 StartZ=0 EndX=-30 EndY=-14 EndZ=0
    g7: LineSegment StartX=-30 StartY=-14 StartZ=0 EndX=-30 EndY=14 EndZ=0
    g8: LineSegment StartX=-26.46 StartY=11.23 StartZ=0 EndX=-23.42 EndY=11.23 EndZ=0
    g9: LineSegment StartX=-23.42 StartY=11.23 StartZ=0 EndX=-23.42 EndY=-2.105 EndZ=0
    g10: LineSegment StartX=-23.42 StartY=-2.105 StartZ=0 EndX=-26.46 EndY=-2.105 EndZ=0
    g11: LineSegment StartX=-26.46 StartY=-2.105 StartZ=0 EndX=-26.46 EndY=11.23 EndZ=0
    g12: GeomPoint X=-24.94 Y=-2.105 Z=0
  constraints (31):
    c: Horizontal(g0,g1)
    c: Horizontal(g2,g3)
    c: Vertical(g0,g3)
    c: Vertical(g2,g1)
    c: DistanceX(g0,g1) = 58
    c: DistanceY(g3,g0) = 26
    c: Symmetric(g0,g2,g-1)
    c: Coincident(g4,g5)
    c: Coincident(g5,g6)
    c: Coincident(g6,g7)
    c: Coincident(g7,g4)
    c: Horizontal(g4)
    c: Horizontal(g6)
    c: Vertical(g5)
    c: Vertical(g7)
    c: Symmetric(g4,g5,g-1)
    c: DistanceX(g4,g0) = 1
    c: DistanceY(g1,g4) = 1
    c: Coincident(g8,g9)
    c: Coincident(g9,g10)
    c: Coincident(g10,g11)
    c: Coincident(g11,g8)
    c: Horizontal(g8)
    c: Horizontal(g10)
    c: Vertical(g9)
    c: Vertical(g11)
    c: DistanceY(g11,g11) = 13.335
    c: DistanceX(g8,g8) = 3.04
    c: Symmetric(g10,g9,g12)
    c: DistanceY(g8,g0) = 1.77
    c: DistanceX(g3,g10) = 2.54
FEATURE [PartDesign::Pad] Pad054
  Direction = (0,0,1)
  Length = 1
  Length2 = 10
  Profile = -> Sketch076
  ReferenceAxis = -> Sketch076 [N_Axis]
  Type = 0
FEATURE [Sketcher::SketchObject] Sketch077
  FullyConstrained = true
  MapMode = 5
  Placement = pos=(0,0,1) rot=(0,0,1;0rad)
  Support = -> [Pad054]
  sketch-geometry (8):
    g0: LineSegment StartX=-29 StartY=13 StartZ=0 EndX=29 EndY=13 EndZ=0
    g1: LineSegment StartX=29 StartY=13 StartZ=0 EndX=29 EndY=-13 EndZ=0
    g2: LineSegment StartX=29 StartY=-13 StartZ=0 EndX=-29 EndY=-13 EndZ=0
    g3: LineSegment StartX=-29 StartY=-13 StartZ=0 EndX=-29 EndY=13 EndZ=0
    g4: LineSegment StartX=-30 StartY=14 StartZ=0 EndX=30 EndY=14 EndZ=0
    g5: LineSegment StartX=30 StartY=14 StartZ=0 EndX=30 EndY=-14 EndZ=0
    g6: LineSegment StartX=30 StartY=-14 StartZ=0 EndX=-30 EndY=-14 EndZ=0
    g7: LineSegment StartX=-30 StartY=-14 StartZ=0 EndX=-30 EndY=14 EndZ=0
  constraints (22):
    c: Coincident(g0,g1)
    c: Coincident(g1,g2)
    c: Coincident(g2,g3)
    c: Coincident(g3,g0)
    c: Horizontal(g0)
    c: Horizontal(g2)
    c: Vertical(g1)
    c: Vertical(g3)
    c: Symmetric(g0,g1,g-1)
    c: DistanceX(g0,g0) = 58
    c: DistanceY(g3,g3) = 26
    c: Coincident(g4,g5)
    c: Coincident(g5,g6)
    c: Coincident(g6,g7)
    c: Coincident(g7,g4)
    c: Horizontal(g4)
    c: Horizontal(g6)
    c: Vertical(g5)
    c: Vertical(g7)
    c: DistanceX(g1,g5) = 1
    c: DistanceY(g0,g4) = 1
    c: Symmetric(g4,g5,g-1)
FEATURE [PartDesign::Pad] Pad055
  BaseFeature = -> Pad054
  Direction = (0,0,1)
  Length = 6
  Length2 = 10
  Profile = -> Sketch077
  ReferenceAxis = -> Sketch077 [N_Axis]
  Type = 0
FEATURE [PartDesign::Body] Body024  label="Geiger Cover Inner006"
  Group = -> [Sketch076,Pad054,Sketch077,Pad055]
  Origin = -> Origin024
  Placement = pos=(0,0,4) rot=(0,0,1;0rad)
  Tip = -> Pad055
FEATURE [Sketcher::SketchObject] Sketch078
  FullyConstrained = true
  MapMode = 5
  Placement = pos=(0,0,1) rot=(0,0,1;0rad)
  Support = -> [Pad053]
  sketch-geometry (12):
    g0: Circle CenterX=-31 CenterY=15 CenterZ=0 NormalX=0 NormalY=0 NormalZ=1 AngleXU=0 Radius=1.5
    g1: Circle CenterX=31 CenterY=15 CenterZ=0 NormalX=0 NormalY=0 NormalZ=1 AngleXU=0 Radius=1.5
    g2: Circle CenterX=31 CenterY=-15 CenterZ=0 NormalX=0 NormalY=0 NormalZ=1 AngleXU=0 Radius=1.5
    g3: Circle CenterX=-31 CenterY=-15 CenterZ=0 NormalX=0 NormalY=0 NormalZ=1 AngleXU=0 Radius=1.5
    g4: GeomPoint X=-29 Y=13 Z=0
    g5: GeomPoint X=29 Y=13 Z=0
    g6: GeomPoint X=29 Y=-13 Z=0
    g7: GeomPoint X=-29 Y=-13 Z=0
    g8: GeomPoint X=-33 Y=17 Z=0
    g9: GeomPoint X=33 Y=17 Z=0
    g10: GeomPoint X=33 Y=-17 Z=0
    g11: GeomPoint X=-33 Y=-17 Z=0
  constraints (24):
    c: Symmetric(g0,g2,g-1)
    c: Horizontal(g0,g1)
    c: Horizontal(g2,g3)
    c: Vertical(g0,g3)
    c: Vertical(g2,g1)
    c: Symmetric(g4,g6,g-1)
    c: Horizontal(g4,g5)
    c: Horizontal(g6,g7)
    c: Vertical(g4,g7)
    c: Vertical(g6,g5)
    c: DistanceX(g4,g5) = 58
    c: DistanceY(g7,g4) = 26
    c: Symmetric(g8,g10,g-1)
    c: Vertical(g8,g11)
    c: Vertical(g10,g9)
    c: Horizontal(g8,g9)
    c: Horizontal(g10,g11)
    c: DistanceX(g8,g4) = 4
    c: Diameter(g0) = 3
    c: Diameter(g1) = 3
    c: Diameter(g2) = 3
    c: Diameter(g3) = 3
    c: DistanceY(g11,g7) = 4
    c: Symmetric(g4,g8,g0)
FEATURE [PartDesign::Pocket] Pocket014
  BaseFeature = -> Pad053
  Direction = (0,0,-1)
  Length = 5
  Length2 = 5
  Profile = -> Sketch078
  ReferenceAxis = -> Sketch078 [N_Axis]
  Type = 1
FEATURE [PartDesign::Body] Body023  label="Geiger Cover Outer006"
  Group = -> [Sketch074,Pad052,Sketch075,Pad053,Sketch078,Pocket014]
  Origin = -> Origin023
  Tip = -> Pocket014
FEATURE [Part::Compound] Compound018  label="Bi2O3 Geiger Cover"
  Links = -> [Body024,Body023,Body019,Body020]
  Placement = pos=(-34,-0.1,79.5) rot=(0.57735,-0.57735,0.57735;4.18879rad)
FEATURE [Sketcher::SketchObject] Sketch079
  FullyConstrained = true
  MapMode = 5
  Placement = pos=(0,0,3) rot=(0,0,1;0rad)
  Support = -> [Pocket008]
  sketch-geometry (16):
    g0: GeomPoint X=-23 Y=36.5 Z=0
    g1: GeomPoint X=-7 Y=36.5 Z=0
    g2: GeomPoint X=-7 Y=-36.5 Z=0
    g3: GeomPoint X=-23 Y=-36.5 Z=0
    g4: GeomPoint X=-15 Y=36.5 Z=0
    g5: GeomPoint X=-7 Y=0 Z=0
    g6: GeomPoint X=-10 Y=33 Z=0
    g7: GeomPoint X=-20 Y=33 Z=0
    g8: Circle CenterX=-21.5 CenterY=34.75 CenterZ=0 NormalX=0 NormalY=0 NormalZ=1 AngleXU=0 Radius=1.25
    g9: Circle CenterX=-8.5 CenterY=34.75 CenterZ=0 NormalX=0 NormalY=0 NormalZ=1 AngleXU=0 Radius=1.25
    g10: GeomPoint X=-15 Y=33 Z=0
    g11: GeomPoint X=-20 Y=-33 Z=0
    g12: GeomPoint X=-10 Y=-33 Z=0
    g13: GeomPoint X=-15 Y=-33 Z=0
    g14: Circle CenterX=-21.5 CenterY=-34.75 CenterZ=0 NormalX=0 NormalY=0 NormalZ=1 AngleXU=0 Radius=1.25
    g15: Circle CenterX=-8.5 CenterY=-34.75 CenterZ=0 NormalX=0 NormalY=0 NormalZ=1 AngleXU=0 Radius=1.25
  constraints (28):
    c: Horizontal(g0,g1)
    c: Horizontal(g2,g3)
    c: Vertical(g1,g2)
    c: Vertical(g0,g3)
    c: Symmetric(g0,g1,g4)
    c: DistanceX(g0,g1) = 16
    c: DistanceY(g2,g1) = 73
    c: Symmetric(g1,g2,g5)
    c: DistanceX(g5) = -7
    c: Horizontal(g5,g-1)
    c: DistanceY(g7,g0) = 3.5
    c: Horizontal(g7,g6)
    c: DistanceX(g7,g6) = 10
    c: Diameter(g8) = 2.5
    c: Symmetric(g0,g7,g8)
    c: Diameter(g9) = 2.5
    c: Symmetric(g6,g1,g9)
    c: Symmetric(g6,g7,g10)
    c: Vertical(g4,g10)
    c: Horizontal(g11,g12)
    c: DistanceY(g3,g11) = 3.5
    c: DistanceX(g11,g12) = 10
    c: Symmetric(g11,g12,g13)
    c: Vertical(g13,g10)
    c: Diameter(g15) = 2.5
    c: Diameter(g14) = 2.5
    c: Symmetric(g3,g11,g14)
    c: Symmetric(g2,g12,g15)
FEATURE [Sketcher::SketchObject] Sketch080
  FullyConstrained = true
  MapMode = 5
  Support = -> [XY_Plane025]
  sketch-geometry (19):
    g0: LineSegment StartX=-8 StartY=36.5 StartZ=0 EndX=8 EndY=36.5 EndZ=0
    g1: LineSegment StartX=8 StartY=-36.5 StartZ=0 EndX=-8 EndY=-36.5 EndZ=0
    g2: GeomPoint X=-8e-16 Y=36.5 Z=0
    g3: LineSegment StartX=8 StartY=-36.5 StartZ=0 EndX=8 EndY=-33 EndZ=0
    g4: LineSegment StartX=8 StartY=36.5 StartZ=0 EndX=8 EndY=33 EndZ=0
    g5: LineSegment StartX=-8 StartY=-36.5 StartZ=0 EndX=-8 EndY=-33 EndZ=0
    g6: LineSegment StartX=-8 StartY=33 StartZ=0 EndX=-8 EndY=36.5 EndZ=0
    g7: Circle CenterX=-6.5 CenterY=34.75 CenterZ=0 NormalX=0 NormalY=0 NormalZ=1 AngleXU=0 Radius=1.25
    g8: Circle CenterX=6.5 CenterY=34.75 CenterZ=0 NormalX=0 NormalY=0 NormalZ=1 AngleXU=0 Radius=1.25
    g9: Circle CenterX=-6.5 CenterY=-34.75 CenterZ=0 NormalX=0 NormalY=0 NormalZ=1 AngleXU=0 Radius=1.25
    g10: Circle CenterX=6.5 CenterY=-34.75 CenterZ=0 NormalX=0 NormalY=0 NormalZ=1 AngleXU=0 Radius=1.25
    g11: LineSegment StartX=8 StartY=33 StartZ=0 EndX=8 EndY=-33 EndZ=0
    g12: LineSegment StartX=-8 StartY=-33 StartZ=0 EndX=-8 EndY=33 EndZ=0
    g13: GeomPoint X=-5 Y=33 Z=0
    g14: GeomPoint X=5 Y=33 Z=0
    g15: GeomPoint X=0 Y=33 Z=0
    g16: GeomPoint X=-5 Y=-33 Z=0
    g17: GeomPoint X=5 Y=-33 Z=0
    g18: GeomPoint X=0 Y=-33 Z=0
  constraints (42):
    c: Horizontal(g0)
    c: Horizontal(g1)
    c: DistanceY(g1,g0) = 73
    c: DistanceX(g0,g0) = 16
    c: Symmetric(g0,g0,g2)
    c: Symmetric(g0,g1,g-1)
    c: Coincident(g1,g3)
    c: Vertical(g3)
    c: Coincident(g0,g4)
    c: Vertical(g4)
    c: Coincident(g1,g5)
    c: Vertical(g5)
    c: Coincident(g6,g0)
    c: Vertical(g6)
    c: Vertical(g4,g3)
    c: Vertical(g6,g5)
    c: DistanceY(g4,g4) = 3.5
    c: Diameter(g7) = 2.5
    c: Diameter(g8) = 2.5
    c: Diameter(g9) = 2.5
    c: Diameter(g10) = 2.5
    c: Coincident(g11,g4)
    c: Coincident(g11,g3)
    c: Coincident(g12,g5)
    c: Coincident(g12,g6)
    c: Horizontal(g4,g6)
    c: Horizontal(g5,g3)
    c: DistanceY(g1,g3) = 3.5
    c: Horizontal(g14,g13)
    c: Horizontal(g13,g6)
    c: Symmetric(g13,g0,g7)
    c: Symmetric(g0,g14,g8)
    c: DistanceX(g13,g14) = 10
    c: PointOnObject(g15,g-2)
    c: Symmetric(g14,g13,g15)
    c: PointOnObject(g18,g-2)
    c: Symmetric(g17,g16,g18)
    c: DistanceX(g16,g17) = 10
    c: Horizontal(g17,g3)
    c: Horizontal(g17,g16)
    c: Symmetric(g16,g1,g9)
    c: Symmetric(g17,g1,g10)
FEATURE [PartDesign::Pad] Pad056
  Direction = (0,0,1)
  Length = 1
  Length2 = 10
  Profile = -> Sketch080
  ReferenceAxis = -> Sketch080 [N_Axis]
  Type = 0
FEATURE [Sketcher::SketchObject] Sketch081
  FullyConstrained = true
  MapMode = 5
  Placement = pos=(0,0,1) rot=(0,0,1;0rad)
  Support = -> [Pad056]
  sketch-geometry (4):
    g0: LineSegment StartX=-5 StartY=34 StartZ=0 EndX=5 EndY=34 EndZ=0
    g1: LineSegment StartX=5 StartY=34 StartZ=0 EndX=5 EndY=-34 EndZ=0
    g2: LineSegment StartX=5 StartY=-34 StartZ=0 EndX=-5 EndY=-34 EndZ=0
    g3: LineSegment StartX=-5 StartY=-34 StartZ=0 EndX=-5 EndY=34 EndZ=0
  constraints (11):
    c: Coincident(g0,g1)
    c: Coincident(g1,g2)
    c: Coincident(g2,g3)
    c: Coincident(g3,g0)
    c: Horizontal(g0)
    c: Horizontal(g2)
    c: Vertical(g1)
    c: Vertical(g3)
    c: DistanceX(g0,g0) = 10
    c: DistanceY(g3,g3) = 68
    c: Symmetric(g1,g0,g-1)
FEATURE [PartDesign::Pad] Pad057
  BaseFeature = -> Pad056
  Direction = (0,0,1)
  Length = 49.5
  Length2 = 10
  Profile = -> Sketch081
  ReferenceAxis = -> Sketch081 [N_Axis]
  Type = 0
FEATURE [Sketcher::SketchObject] Sketch082
  FullyConstrained = true
  MapMode = 5
  Placement = pos=(-5,0,0) rot=(0.57735,-0.57735,-0.57735;2.0944rad)
  Support = -> [Pad057]
  sketch-geometry (13):
    g0: Circle CenterX=31 CenterY=47.5 CenterZ=0 NormalX=0 NormalY=0 NormalZ=1 AngleXU=0 Radius=1.5
    g1: Circle CenterX=-31 CenterY=47.5 CenterZ=0 NormalX=0 NormalY=0 NormalZ=1 AngleXU=0 Radius=1.5
    g2: Circle CenterX=-31 CenterY=17.5 CenterZ=0 NormalX=0 NormalY=0 NormalZ=1 AngleXU=0 Radius=1.5
    g3: Circle CenterX=31 CenterY=17.5 CenterZ=0 NormalX=0 NormalY=0 NormalZ=1 AngleXU=0 Radius=1.5
    g4: GeomPoint X=0 Y=32.5 Z=0
    g5: GeomPoint X=-34 Y=50.5 Z=0
    g6: GeomPoint X=34 Y=50.5 Z=0
    g7: GeomPoint X=34 Y=14.5 Z=0
    g8: GeomPoint X=-34 Y=14.5 Z=0
    g9: GeomPoint X=-28 Y=20.5 Z=0
    g10: GeomPoint X=28 Y=20.5 Z=0
    g11: GeomPoint X=28 Y=44.5 Z=0
    g12: GeomPoint X=-28 Y=44.5 Z=0
  constraints (26):
    c: Diameter(g0) = 3
    c: Diameter(g1) = 3
    c: Diameter(g2) = 3
    c: Diameter(g3) = 3
    c: Vertical(g1,g2)
    c: Vertical(g3,g0)
    c: Horizontal(g1,g0)
    c: Horizontal(g3,g2)
    c: Symmetric(g1,g3,g4)
    c: Horizontal(g12,g11)
    c: Horizontal(g10,g9)
    c: Symmetric(g12,g10,g4)
    c: Vertical(g10,g11)
    c: Vertical(g12,g9)
    c: Vertical(g5,g8)
    c: Vertical(g7,g6)
    c: Horizontal(g5,g6)
    c: Horizontal(g7,g8)
    c: Symmetric(g8,g6,g4)
    c: DistanceX(g5,g12) = 6
    c: DistanceY(g7,g10) = 6
    c: Symmetric(g5,g12,g1)
    c: DistanceX(g5,g6) = 68
    c: DistanceY(g7,g6) = 36
    c: Vertical(g4,g-1)
    c: DistanceY(g-1,g5) = 50.5
FEATURE [PartDesign::Pocket] Pocket015
  BaseFeature = -> Pad057
  Direction = (1,0,0)
  Length = 5
  Length2 = 5
  Profile = -> Sketch082
  ReferenceAxis = -> Sketch082 [N_Axis]
  Type = 1
FEATURE [PartDesign::Body] Body025  label="Double Geiger Holder"
  Group = -> [Sketch080,Pad056,Sketch081,Pad057,Sketch082,Pocket015]
  Origin = -> Origin025
  Placement = pos=(-15,0,47) rot=(0,0,1;0rad)
  Tip = -> Pocket015
FEATURE [PartDesign::Pocket] Pocket016
  BaseFeature = -> Pocket008
  Direction = (0,0,-1)
  Length = 5
  Length2 = 5
  Profile = -> Sketch079
  ReferenceAxis = -> Sketch079 [N_Axis]
  Type = 1
FEATURE [PartDesign::Body] Body002  label="Sensor Stack Layer 1"
  Group = -> [Sketch019,Pad009,Sketch040,Pocket007,Sketch046,Pocket008,Sketch079,Pocket016]
  Origin = -> Origin002
  Placement = pos=(0,0,41) rot=(0,0,1;0rad)
  Tip = -> Pocket016
FEATURE [App::DocumentObjectGroup] Group016  label="Sensor Layer 1"
  Group = -> [Body002,Compound016,Compound017,Compound018,Body025]
FEATURE [App::DocumentObjectGroup] Group  label="Stack Layers"
  Group = -> [Group013,Group016]
FEATURE [Part::Box] Box003  label="Cube003"
  AttacherType = Attacher::AttachEngine3D
  Height = 5
  Length = 11
  Placement = pos=(144.5,2,0) rot=(0,0,1;0rad)
  Width = 66
FEATURE [Sketcher::SketchObject] Sketch083
  FullyConstrained = true
  MapMode = 5
  Support = -> [XY_Plane026]
  sketch-geometry (8):
    g0: LineSegment StartX=-4.5 StartY=32 StartZ=0 EndX=4.5 EndY=32 EndZ=0
    g1: LineSegment StartX=4.5 StartY=32 StartZ=0 EndX=4.5 EndY=-32 EndZ=0
    g2: LineSegment StartX=4.5 StartY=-32 StartZ=0 EndX=-4.5 EndY=-32 EndZ=0
    g3: LineSegment StartX=-4.5 StartY=-32 StartZ=0 EndX=-4.5 EndY=32 EndZ=0
    g4: GeomPoint X=-3.5 Y=31 Z=0
    g5: GeomPoint X=3.5 Y=31 Z=0
    g6: GeomPoint X=3.5 Y=-31 Z=0
    g7: GeomPoint X=-3.5 Y=-31 Z=0
  constraints (18):
    c: Coincident(g0,g1)
    c: Coincident(g1,g2)
    c: Coincident(g2,g3)
    c: Coincident(g3,g0)
    c: Horizontal(g0)
    c: Horizontal(g2)
    c: Vertical(g1)
    c: Vertical(g3)
    c: Symmetric(g0,g1,g-1)
    c: Horizontal(g7,g6)
    c: Horizontal(g5,g4)
    c: Vertical(g4,g7)
    c: Vertical(g6,g5)
    c: DistanceX(g4,g5) = 7
    c: DistanceY(g7,g4) = 62
    c: Symmetric(g4,g6,g-1)
    c: DistanceX(g0,g4) = 1
    c: DistanceY(g4,g0) = 1
FEATURE [PartDesign::Pad] Pad058
  Direction = (0,0,1)
  Length = 1
  Length2 = 10
  Profile = -> Sketch083
  ReferenceAxis = -> Sketch083 [N_Axis]
  Type = 0
FEATURE [Sketcher::SketchObject] Sketch084
  FullyConstrained = true
  MapMode = 5
  Placement = pos=(0,0,1) rot=(0,0,1;0rad)
  Support = -> [Pad058]
  sketch-geometry (8):
    g0: LineSegment StartX=-4.5 StartY=32 StartZ=0 EndX=4.5 EndY=32 EndZ=0
    g1: LineSegment StartX=4.5 StartY=32 StartZ=0 EndX=4.5 EndY=-32 EndZ=0
    g2: LineSegment StartX=4.5 StartY=-32 StartZ=0 EndX=-4.5 EndY=-32 EndZ=0
    g3: LineSegment StartX=-4.5 StartY=-32 StartZ=0 EndX=-4.5 EndY=32 EndZ=0
    g4: LineSegment StartX=-3.5 StartY=31 StartZ=0 EndX=3.5 EndY=31 EndZ=0
    g5: LineSegment StartX=3.5 StartY=31 StartZ=0 EndX=3.5 EndY=-31 EndZ=0
    g6: LineSegment StartX=3.5 StartY=-31 StartZ=0 EndX=-3.5 EndY=-31 EndZ=0
    g7: LineSegment StartX=-3.5 StartY=-31 StartZ=0 EndX=-3.5 EndY=31 EndZ=0
  constraints (22):
    c: Coincident(g0,g1)
    c: Coincident(g1,g2)
    c: Coincident(g2,g3)
    c: Coincident(g3,g0)
    c: Horizontal(g0)
    c: Horizontal(g2)
    c: Vertical(g1)
    c: Vertical(g3)
    c: Symmetric(g0,g1,g-1)
    c: Coincident(g4,g5)
    c: Coincident(g5,g6)
    c: Coincident(g6,g7)
    c: Coincident(g7,g4)
    c: Horizontal(g4)
    c: Horizontal(g6)
    c: Vertical(g5)
    c: Vertical(g7)
    c: DistanceX(g0,g4) = 1
    c: DistanceY(g4,g0) = 1
    c: Symmetric(g4,g5,g-1)
    c: DistanceX(g4,g4) = 7
    c: DistanceY(g7,g7) = 62
FEATURE [PartDesign::Pad] Pad059
  BaseFeature = -> Pad058
  Direction = (0,0,1)
  Length = 3
  Length2 = 10
  Profile = -> Sketch084
  ReferenceAxis = -> Sketch084 [N_Axis]
  Type = 0
FEATURE [PartDesign::Body] Body026  label="SideMold001"
  Group = -> [Sketch083,Pad058,Sketch084,Pad059]
  Origin = -> Origin026
  Placement = pos=(150,35,0) rot=(0,0,1;0rad)
  Tip = -> Pad059
FEATURE [Part::Cut] Cut003  label="Long Side Mold"
  Base = -> Box003
  Placement = pos=(0,-19,0) rot=(0,0,1;0rad)
  Tool = -> Body026
FEATURE [App::DocumentObjectGroup] Group022  label="Sides"
  Group = -> [Cut002,Cut003]
FEATURE [App::DocumentObjectGroup] Group019  label="Silicone Molds"
  Group = -> [Group020,Group021,Group022]
FEATURE [App::DocumentObjectGroup] Group018  label="Geiger Cover"
  Group = -> [Body003,Body004,Group019,Spreadsheet,Spreadsheet001]
FEATURE [App::DocumentObjectGroup] Group017  label="Misc"
  Group = -> [Group018]
FEATURE [TechDraw::DrawViewPart] View
  CoarseView = true
  Direction = (0.577,-0.577,0.577)
  Focus = 100
  HardHidden = true
  IsoCount = 0
  IsoHidden = false
  IsoVisible = false
  LockPosition = false
  Perspective = false
  Rotation = 0
  ScaleType = 0
  SeamHidden = false
  SeamVisible = true
  SmoothHidden = false
  SmoothVisible = true
  Source = -> [Template,Cut,Cut001,Cut002,Cut003]
  X = 72.1452
  XDirection = (0.707,0.707,0)
  Y = 138.622
FEATURE [TechDraw::DrawLeaderLine] LeaderLine
  AutoHorizontal = false
  EndSymbol = 7
  LeaderParent = -> View
  LockPosition = true
  Rotation = 0
  Scalable = false
  ScaleType = 0
  StartSymbol = 0
  WayPoints = (2) [(0,0,0),(-236.522,-270.263,0)]
  X = 14.0514
  Y = 13.7009
FEATURE [TechDraw::DrawLeaderLine] LeaderLine001
  AutoHorizontal = false
  EndSymbol = 7
  LeaderParent = -> View
  LockPosition = true
  Rotation = 0
  Scalable = false
  ScaleType = 0
  StartSymbol = 0
  WayPoints = (2) [(0,0,0),(-322.9,-282.689,0)]
  X = -19.1451
  Y = -2.45296
FEATURE [TechDraw::DrawLeaderLine] LeaderLine002
  AutoHorizontal = false
  EndSymbol = 7
  LeaderParent = -> View
  LockPosition = true
  Rotation = 0
  Scalable = false
  ScaleType = 0
  StartSymbol = 0
  WayPoints = (2) [(0,0,0),(90.7563,88.1572,0)]
  X = 46.8473
  Y = -5.90178
FEATURE [TechDraw::DrawViewAnnotation] Annotation005
  Font = osifont
  LineSpace = 80
  LockPosition = false
  MaxWidth = -1
  Rotation = 0
  ScaleType = 0
  Text = Long Side Mold
  TextSize = 5
  TextStyle = 0
  X = 92.5801
  Y = 85.3316
FEATURE [TechDraw::DrawLeaderLine] LeaderLine003
  AutoHorizontal = false
  EndSymbol = 7
  LeaderParent = -> View
  LockPosition = true
  Rotation = 0
  Scalable = false
  ScaleType = 0
  StartSymbol = 0
  WayPoints = (2) [(0,0,0),(65.5613,134.979,0)]
  X = 7.31606
  Y = -31.6499
FEATURE [TechDraw::DrawPage] Page  label="Geiger Cover Technical Design"
  KeepUpdated = true
  NextBalloonIndex = 1
  ProjectionType = 0
  Template = -> Template
  Views = -> [View,Annotation,Annotation001,Annotation002,LeaderLine,LeaderLine001,LeaderLine002,Annotation003,Annotation004,Annotation005,LeaderLine003]
FEATURE [App::DocumentObjectGroup] Group024  label="Tech Draws"
  Group = -> [Page]
FEATURE [Part::Feature] Solid054  label="M2.5x08HexButttonHead010"
  Placement = pos=(-21.5,34.8125,45.0625) rot=(0,0,1;0rad)
  shape: bbox 4.6 x 4.6 x 9.5 mm, 13 faces (baked)
FEATURE [Part::Feature] Solid055  label="M2.5x08HexButttonHead011"
  Placement = pos=(-21.5,-34.6875,45.0625) rot=(0,0,1;0rad)
  shape: bbox 4.6 x 4.6 x 9.5 mm, 13 faces (baked)
FEATURE [Part::Compound] Compound019
  Links = -> [Solid054,Solid055]
  Placement = pos=(13,0,0) rot=(0,0,1;0rad)
FEATURE [Part::Feature] Solid053  label="M2.5x08HexButttonHead009"
  Placement = pos=(-21.5,34.8125,45.0625) rot=(0,0,1;0rad)
  shape: bbox 4.6 x 4.6 x 9.5 mm, 13 faces (baked)
FEATURE [Part::Feature] Solid052  label="M2.5x08HexButttonHead008"
  Placement = pos=(-21.5,-34.6875,45.0625) rot=(0,0,1;0rad)
  shape: bbox 4.6 x 4.6 x 9.5 mm, 13 faces (baked)
FEATURE [Part::Compound] Compound020  label="Double Geiger Mount Screws"
  Links = -> [Solid052,Solid053,Compound019]
  Placement = pos=(-30,0,86) rot=(0,1,0;3.14159rad)
FEATURE [App::DocumentObjectGroup] Group008  label="Screws"
  Group = -> [Compound,Compound005,Compound006,Compound009,Compound020]
FEATURE [App::DocumentObjectGroup] Group006  label="Metal Parts"
  Group = -> [Group007,Group008,Group012,Group015]
FEATURE [Part::Feature] Adafruit_Micro_Lipo_wMicroUSB_Jack___USB_LiIonLiPoly_charger002
  Placement = pos=(-10.8045,0.225608,2.8275) rot=(0.57735,-0.57735,-0.57735;2.0944rad)
  shape: bbox 6.104 x 8.8 x 3.007 mm, 277 faces, 0 solids (baked)
FEATURE [Part::Compound] Compound004  label="Adafruit Lipo Charger"
  Links = -> [Adafruit_Micro_Lipo_wMicroUSB_Jack___USB_LiIonLiPoly_charger,Adafruit_Micro_Lipo_wMicroUSB_Jack___USB_LiIonLiPoly_charger002,Adafruit_Micro_Lipo_wMicroUSB_Jack___USB_LiIonLiPoly_charger003]
  Placement = pos=(-25,0,23.5) rot=(0,0,1;0rad)
FEATURE [App::DocumentObjectGroup] Group014  label="Electronics"
  Group = -> [Compound004,Feature,Compound007]
FEATURE [Sketcher::SketchObject] Sketch085
  FullyConstrained = true
  MapMode = 5
  Support = -> [XY_Plane027]
  sketch-geometry (19):
    g0: LineSegment StartX=-8 StartY=36.5 StartZ=0 EndX=8 EndY=36.5 EndZ=0
    g1: LineSegment StartX=8 StartY=-36.5 StartZ=0 EndX=-8 EndY=-36.5 EndZ=0
    g2: GeomPoint X=-8e-16 Y=36.5 Z=0
    g3: LineSegment StartX=8 StartY=-36.5 StartZ=0 EndX=8 EndY=-33 EndZ=0
    g4: LineSegment StartX=8 StartY=36.5 StartZ=0 EndX=8 EndY=33 EndZ=0
    g5: LineSegment StartX=-8 StartY=-36.5 StartZ=0 EndX=-8 EndY=-33 EndZ=0
    g6: LineSegment StartX=-8 StartY=33 StartZ=0 EndX=-8 EndY=36.5 EndZ=0
    g7: Circle CenterX=-6.5 CenterY=34.75 CenterZ=0 NormalX=0 NormalY=0 NormalZ=1 AngleXU=0 Radius=1.25
    g8: Circle CenterX=6.5 CenterY=34.75 CenterZ=0 NormalX=0 NormalY=0 NormalZ=1 AngleXU=0 Radius=1.25
    g9: Circle CenterX=-6.5 CenterY=-34.75 CenterZ=0 NormalX=0 NormalY=0 NormalZ=1 AngleXU=0 Radius=1.25
    g10: Circle CenterX=6.5 CenterY=-34.75 CenterZ=0 NormalX=0 NormalY=0 NormalZ=1 AngleXU=0 Radius=1.25
    g11: LineSegment StartX=8 StartY=33 StartZ=0 EndX=8 EndY=-33 EndZ=0
    g12: LineSegment StartX=-8 StartY=-33 StartZ=0 EndX=-8 EndY=33 EndZ=0
    g13: GeomPoint X=-5 Y=33 Z=0
    g14: GeomPoint X=5 Y=33 Z=0
    g15: GeomPoint X=0 Y=33 Z=0
    g16: GeomPoint X=-5 Y=-33 Z=0
    g17: GeomPoint X=5 Y=-33 Z=0
    g18: GeomPoint X=0 Y=-33 Z=0
  constraints (42):
    c: Horizontal(g0)
    c: Horizontal(g1)
    c: DistanceY(g1,g0) = 73
    c: DistanceX(g0,g0) = 16
    c: Symmetric(g0,g0,g2)
    c: Symmetric(g0,g1,g-1)
    c: Coincident(g1,g3)
    c: Vertical(g3)
    c: Coincident(g0,g4)
    c: Vertical(g4)
    c: Coincident(g1,g5)
    c: Vertical(g5)
    c: Coincident(g6,g0)
    c: Vertical(g6)
    c: Vertical(g4,g3)
    c: Vertical(g6,g5)
    c: DistanceY(g4,g4) = 3.5
    c: Diameter(g7) = 2.5
    c: Diameter(g8) = 2.5
    c: Diameter(g9) = 2.5
    c: Diameter(g10) = 2.5
    c: Coincident(g11,g4)
    c: Coincident(g11,g3)
    c: Coincident(g12,g5)
    c: Coincident(g12,g6)
    c: Horizontal(g4,g6)
    c: Horizontal(g5,g3)
    c: DistanceY(g1,g3) = 3.5
    c: Horizontal(g14,g13)
    c: Horizontal(g13,g6)
    c: Symmetric(g13,g0,g7)
    c: Symmetric(g0,g14,g8)
    c: DistanceX(g13,g14) = 10
    c: PointOnObject(g15,g-2)
    c: Symmetric(g14,g13,g15)
    c: PointOnObject(g18,g-2)
    c: Symmetric(g17,g16,g18)
    c: DistanceX(g16,g17) = 10
    c: Horizontal(g17,g3)
    c: Horizontal(g17,g16)
    c: Symmetric(g16,g1,g9)
    c: Symmetric(g17,g1,g10)
FEATURE [PartDesign::Pad] Pad060
  Direction = (0,0,1)
  Length = 3
  Length2 = 10
  Profile = -> Sketch085
  ReferenceAxis = -> Sketch085 [N_Axis]
  Type = 0
FEATURE [PartDesign::Body] Body027  label="Double Geiger Spacer"
  Group = -> [Sketch085,Pad060]
  Origin = -> Origin027
  Placement = pos=(-15,0,44) rot=(0,0,1;0rad)
  Tip = -> Pad060
